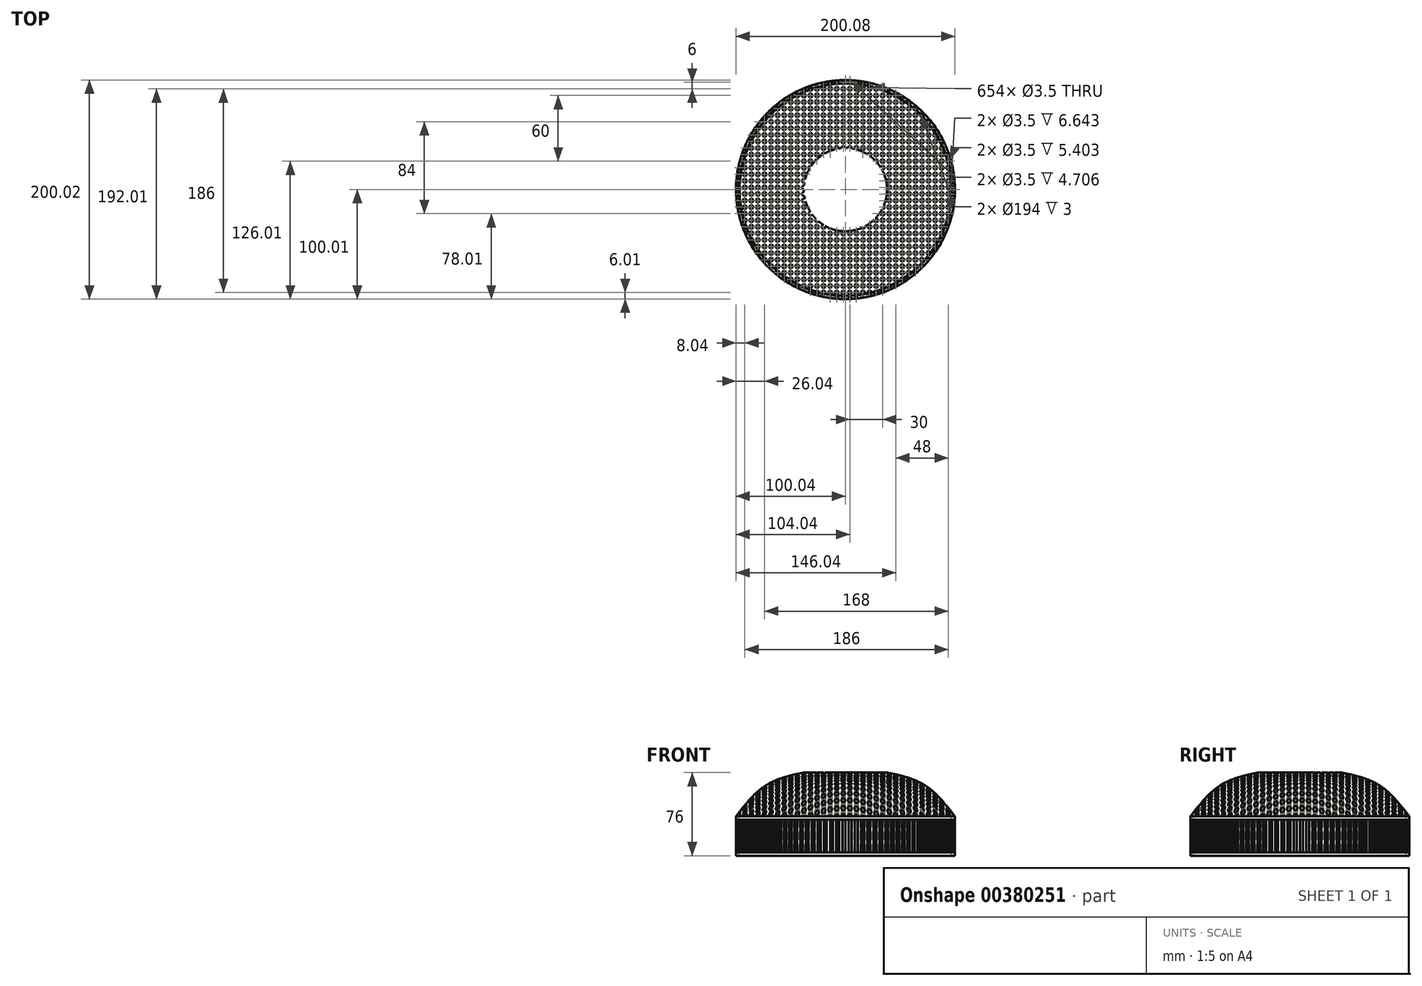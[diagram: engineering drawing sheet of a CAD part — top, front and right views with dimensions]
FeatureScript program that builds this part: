
annotation { "Feature Type Name" : "Feature", "Feature Type Description" : "" }
export const myFeature = defineFeature(function(context is Context, id is Id, definition is map)
    precondition{}
    {
        {
            var Q0;
            Q0=qCreatedBy(makeId("Top.planeOp"),FACE);
            var sketch = newSketch(context, id + "F0", { "sketchPlane" : qUnion([Q0])});
            skCircle(sketch, "E0", {"center": v(0, 0) * mm, "radius": 100 * mm});
            skSolve(sketch);
        }
        {
            var Q0;
            Q0=qCreatedBy(makeId("Top.planeOp"),FACE);
            cPlane(context, id + "F1", {"entities" : qUnion([Q0]), "cplaneType" : CPlaneType.OFFSET, "offset" : 30 * mm, "width" : 150 * mm, "height" : 150 * mm});
        }
        {
            var Q0;
            Q0=qCreatedBy(id+"F1.planeOp",FACE);
            var sketch = newSketch(context, id + "F2", { "sketchPlane" : qUnion([Q0])});
            skCircle(sketch, "E1", {"center": v(0, 0) * mm, "radius": 70 * mm});
            skSolve(sketch);
        }
        {
            var Q0;
            Q0=qCreatedBy(makeId("Top.planeOp"),FACE);
            cPlane(context, id + "F3", {"entities" : qUnion([Q0]), "cplaneType" : CPlaneType.OFFSET, "offset" : 40 * mm, "width" : 150 * mm, "height" : 150 * mm});
        }
        {
            var Q0;
            Q0=qCreatedBy(id+"F3.planeOp",FACE);
            var sketch = newSketch(context, id + "F4", { "sketchPlane" : qUnion([Q0])});
            skCircle(sketch, "E2", {"center": v(0, 0) * mm, "radius": 38 * mm});
            skSolve(sketch);
        }
        {
            var Q0;
            Q0 = qSketchRegion(id + "F0", true);
            var Q1;
            Q1 = qSketchRegion(id + "F2", true);
            var Q2;
            Q2 = qSketchRegion(id + "F4", true);
            loft(context, id + "F5", {"sheetProfilesArray" : [{ "sheetProfileEntities" : qUnion([Q0]) }, { "sheetProfileEntities" : qUnion([Q1]) }, { "sheetProfileEntities" : qUnion([Q2]) }]});
        }
        {
            var Q0;
            Q0=makeQuery(id+"F5.opLoft","CAP_FACE",FACE,{"disambiguationData":[OSD([makeQuery(id+"F0.imprint","IMPRINT",FACE,{"disambiguationData":[TD([[makeQuery(id+"F0.imprint","IMPRINT",EDGE,{"derivedFrom":sQuery(id+"F0.wireOp",EDGE,"E0")}),1.0]])]})])],"isStart":true});
            shell(context, id + "F6", {"entities" : qUnion([Q0]), "thickness" : 3 * mm});
        }
        {
            var Q0;
            Q0=makeQuery(id+"F5.opLoft","CAP_FACE",FACE,{"disambiguationData":[OSD([makeQuery(id+"F4.imprint","IMPRINT",FACE,{"disambiguationData":[TD([[makeQuery(id+"F4.imprint","IMPRINT",EDGE,{"derivedFrom":sQuery(id+"F4.wireOp",EDGE,"E2")}),1.0]])]})])],"isStart":true});
            extrude(context, id + "F7", {"entities" : qUnion([Q0]), "operationType" : NewBodyOperationType.REMOVE, "oppositeDirection" : true, "depth" : 25 * mm});
        }
        {
            var Q0;
            Q0=qCreatedBy(makeId("Top.planeOp"),FACE);
            var sketch = newSketch(context, id + "F8", { "sketchPlane" : qUnion([Q0])});
            skLineSegment(sketch, "E3", {"start": v(0, 0) * mm, "end": v(0, -100) * mm, "construction": true});
            skCircle(sketch, "E4", {"center": v(100, -100) * mm, "radius": 1.75 * mm});
            skLineSegment(sketch, "E5", {"start": v(0, 0) * mm, "end": v(100, 0) * mm, "construction": true});
            skLineSegment(sketch, "E6", {"start": v(100, 0) * mm, "end": v(100, -100) * mm, "construction": true});
            skCircle(sketch, "E7.0.1.0", {"center": v(100, -94) * mm, "radius": 1.75 * mm});
            skCircle(sketch, "E7.0.2.0", {"center": v(100, -88) * mm, "radius": 1.75 * mm});
            skCircle(sketch, "E7.0.3.0", {"center": v(100, -82) * mm, "radius": 1.75 * mm});
            skCircle(sketch, "E7.0.4.0", {"center": v(100, -76) * mm, "radius": 1.75 * mm});
            skCircle(sketch, "E7.0.5.0", {"center": v(100, -70) * mm, "radius": 1.75 * mm});
            skCircle(sketch, "E7.0.6.0", {"center": v(100, -64) * mm, "radius": 1.75 * mm});
            skCircle(sketch, "E7.0.7.0", {"center": v(100, -58) * mm, "radius": 1.75 * mm});
            skCircle(sketch, "E7.0.8.0", {"center": v(100, -52) * mm, "radius": 1.75 * mm});
            skCircle(sketch, "E7.0.9.0", {"center": v(100, -46) * mm, "radius": 1.75 * mm});
            skCircle(sketch, "E7.0.10.0", {"center": v(100, -40) * mm, "radius": 1.75 * mm});
            skCircle(sketch, "E7.0.11.0", {"center": v(100, -34) * mm, "radius": 1.75 * mm});
            skCircle(sketch, "E7.0.12.0", {"center": v(100, -28) * mm, "radius": 1.75 * mm});
            skCircle(sketch, "E7.0.13.0", {"center": v(100, -22) * mm, "radius": 1.75 * mm});
            skCircle(sketch, "E7.0.14.0", {"center": v(100, -16) * mm, "radius": 1.75 * mm});
            skCircle(sketch, "E7.0.15.0", {"center": v(100, -10) * mm, "radius": 1.75 * mm});
            skCircle(sketch, "E7.0.16.0", {"center": v(100, -4) * mm, "radius": 1.75 * mm});
            skCircle(sketch, "E7.0.17.0", {"center": v(100, 2) * mm, "radius": 1.75 * mm});
            skCircle(sketch, "E7.0.18.0", {"center": v(100, 8) * mm, "radius": 1.75 * mm});
            skCircle(sketch, "E7.1.0.0", {"center": v(94, -100) * mm, "radius": 1.75 * mm});
            skCircle(sketch, "E7.1.1.0", {"center": v(94, -94) * mm, "radius": 1.75 * mm});
            skCircle(sketch, "E7.1.2.0", {"center": v(94, -88) * mm, "radius": 1.75 * mm});
            skCircle(sketch, "E7.1.3.0", {"center": v(94, -82) * mm, "radius": 1.75 * mm});
            skCircle(sketch, "E7.1.4.0", {"center": v(94, -76) * mm, "radius": 1.75 * mm});
            skCircle(sketch, "E7.1.5.0", {"center": v(94, -70) * mm, "radius": 1.75 * mm});
            skCircle(sketch, "E7.1.6.0", {"center": v(94, -64) * mm, "radius": 1.75 * mm});
            skCircle(sketch, "E7.1.7.0", {"center": v(94, -58) * mm, "radius": 1.75 * mm});
            skCircle(sketch, "E7.1.8.0", {"center": v(94, -52) * mm, "radius": 1.75 * mm});
            skCircle(sketch, "E7.1.9.0", {"center": v(94, -46) * mm, "radius": 1.75 * mm});
            skCircle(sketch, "E7.1.10.0", {"center": v(94, -40) * mm, "radius": 1.75 * mm});
            skCircle(sketch, "E7.1.11.0", {"center": v(94, -34) * mm, "radius": 1.75 * mm});
            skCircle(sketch, "E7.1.12.0", {"center": v(94, -28) * mm, "radius": 1.75 * mm});
            skCircle(sketch, "E7.1.13.0", {"center": v(94, -22) * mm, "radius": 1.75 * mm});
            skCircle(sketch, "E7.1.14.0", {"center": v(94, -16) * mm, "radius": 1.75 * mm});
            skCircle(sketch, "E7.1.15.0", {"center": v(94, -10) * mm, "radius": 1.75 * mm});
            skCircle(sketch, "E7.1.16.0", {"center": v(94, -4) * mm, "radius": 1.75 * mm});
            skCircle(sketch, "E7.1.17.0", {"center": v(94, 2) * mm, "radius": 1.75 * mm});
            skCircle(sketch, "E7.1.18.0", {"center": v(94, 8) * mm, "radius": 1.75 * mm});
            skCircle(sketch, "E7.2.0.0", {"center": v(88, -100) * mm, "radius": 1.75 * mm});
            skCircle(sketch, "E7.2.1.0", {"center": v(88, -94) * mm, "radius": 1.75 * mm});
            skCircle(sketch, "E7.2.2.0", {"center": v(88, -88) * mm, "radius": 1.75 * mm});
            skCircle(sketch, "E7.2.3.0", {"center": v(88, -82) * mm, "radius": 1.75 * mm});
            skCircle(sketch, "E7.2.4.0", {"center": v(88, -76) * mm, "radius": 1.75 * mm});
            skCircle(sketch, "E7.2.5.0", {"center": v(88, -70) * mm, "radius": 1.75 * mm});
            skCircle(sketch, "E7.2.6.0", {"center": v(88, -64) * mm, "radius": 1.75 * mm});
            skCircle(sketch, "E7.2.7.0", {"center": v(88, -58) * mm, "radius": 1.75 * mm});
            skCircle(sketch, "E7.2.8.0", {"center": v(88, -52) * mm, "radius": 1.75 * mm});
            skCircle(sketch, "E7.2.9.0", {"center": v(88, -46) * mm, "radius": 1.75 * mm});
            skCircle(sketch, "E7.2.10.0", {"center": v(88, -40) * mm, "radius": 1.75 * mm});
            skCircle(sketch, "E7.2.11.0", {"center": v(88, -34) * mm, "radius": 1.75 * mm});
            skCircle(sketch, "E7.2.12.0", {"center": v(88, -28) * mm, "radius": 1.75 * mm});
            skCircle(sketch, "E7.2.13.0", {"center": v(88, -22) * mm, "radius": 1.75 * mm});
            skCircle(sketch, "E7.2.14.0", {"center": v(88, -16) * mm, "radius": 1.75 * mm});
            skCircle(sketch, "E7.2.15.0", {"center": v(88, -10) * mm, "radius": 1.75 * mm});
            skCircle(sketch, "E7.2.16.0", {"center": v(88, -4) * mm, "radius": 1.75 * mm});
            skCircle(sketch, "E7.2.17.0", {"center": v(88, 2) * mm, "radius": 1.75 * mm});
            skCircle(sketch, "E7.2.18.0", {"center": v(88, 8) * mm, "radius": 1.75 * mm});
            skCircle(sketch, "E7.3.0.0", {"center": v(82, -100) * mm, "radius": 1.75 * mm});
            skCircle(sketch, "E7.3.1.0", {"center": v(82, -94) * mm, "radius": 1.75 * mm});
            skCircle(sketch, "E7.3.2.0", {"center": v(82, -88) * mm, "radius": 1.75 * mm});
            skCircle(sketch, "E7.3.3.0", {"center": v(82, -82) * mm, "radius": 1.75 * mm});
            skCircle(sketch, "E7.3.4.0", {"center": v(82, -76) * mm, "radius": 1.75 * mm});
            skCircle(sketch, "E7.3.5.0", {"center": v(82, -70) * mm, "radius": 1.75 * mm});
            skCircle(sketch, "E7.3.6.0", {"center": v(82, -64) * mm, "radius": 1.75 * mm});
            skCircle(sketch, "E7.3.7.0", {"center": v(82, -58) * mm, "radius": 1.75 * mm});
            skCircle(sketch, "E7.3.8.0", {"center": v(82, -52) * mm, "radius": 1.75 * mm});
            skCircle(sketch, "E7.3.9.0", {"center": v(82, -46) * mm, "radius": 1.75 * mm});
            skCircle(sketch, "E7.3.10.0", {"center": v(82, -40) * mm, "radius": 1.75 * mm});
            skCircle(sketch, "E7.3.11.0", {"center": v(82, -34) * mm, "radius": 1.75 * mm});
            skCircle(sketch, "E7.3.12.0", {"center": v(82, -28) * mm, "radius": 1.75 * mm});
            skCircle(sketch, "E7.3.13.0", {"center": v(82, -22) * mm, "radius": 1.75 * mm});
            skCircle(sketch, "E7.3.14.0", {"center": v(82, -16) * mm, "radius": 1.75 * mm});
            skCircle(sketch, "E7.3.15.0", {"center": v(82, -10) * mm, "radius": 1.75 * mm});
            skCircle(sketch, "E7.3.16.0", {"center": v(82, -4) * mm, "radius": 1.75 * mm});
            skCircle(sketch, "E7.3.17.0", {"center": v(82, 2) * mm, "radius": 1.75 * mm});
            skCircle(sketch, "E7.3.18.0", {"center": v(82, 8) * mm, "radius": 1.75 * mm});
            skCircle(sketch, "E7.4.0.0", {"center": v(76, -100) * mm, "radius": 1.75 * mm});
            skCircle(sketch, "E7.4.1.0", {"center": v(76, -94) * mm, "radius": 1.75 * mm});
            skCircle(sketch, "E7.4.2.0", {"center": v(76, -88) * mm, "radius": 1.75 * mm});
            skCircle(sketch, "E7.4.3.0", {"center": v(76, -82) * mm, "radius": 1.75 * mm});
            skCircle(sketch, "E7.4.4.0", {"center": v(76, -76) * mm, "radius": 1.75 * mm});
            skCircle(sketch, "E7.4.5.0", {"center": v(76, -70) * mm, "radius": 1.75 * mm});
            skCircle(sketch, "E7.4.6.0", {"center": v(76, -64) * mm, "radius": 1.75 * mm});
            skCircle(sketch, "E7.4.7.0", {"center": v(76, -58) * mm, "radius": 1.75 * mm});
            skCircle(sketch, "E7.4.8.0", {"center": v(76, -52) * mm, "radius": 1.75 * mm});
            skCircle(sketch, "E7.4.9.0", {"center": v(76, -46) * mm, "radius": 1.75 * mm});
            skCircle(sketch, "E7.4.10.0", {"center": v(76, -40) * mm, "radius": 1.75 * mm});
            skCircle(sketch, "E7.4.11.0", {"center": v(76, -34) * mm, "radius": 1.75 * mm});
            skCircle(sketch, "E7.4.12.0", {"center": v(76, -28) * mm, "radius": 1.75 * mm});
            skCircle(sketch, "E7.4.13.0", {"center": v(76, -22) * mm, "radius": 1.75 * mm});
            skCircle(sketch, "E7.4.14.0", {"center": v(76, -16) * mm, "radius": 1.75 * mm});
            skCircle(sketch, "E7.4.15.0", {"center": v(76, -10) * mm, "radius": 1.75 * mm});
            skCircle(sketch, "E7.4.16.0", {"center": v(76, -4) * mm, "radius": 1.75 * mm});
            skCircle(sketch, "E7.4.17.0", {"center": v(76, 2) * mm, "radius": 1.75 * mm});
            skCircle(sketch, "E7.4.18.0", {"center": v(76, 8) * mm, "radius": 1.75 * mm});
            skCircle(sketch, "E7.5.0.0", {"center": v(70, -100) * mm, "radius": 1.75 * mm});
            skCircle(sketch, "E7.5.1.0", {"center": v(70, -94) * mm, "radius": 1.75 * mm});
            skCircle(sketch, "E7.5.2.0", {"center": v(70, -88) * mm, "radius": 1.75 * mm});
            skCircle(sketch, "E7.5.3.0", {"center": v(70, -82) * mm, "radius": 1.75 * mm});
            skCircle(sketch, "E7.5.4.0", {"center": v(70, -76) * mm, "radius": 1.75 * mm});
            skCircle(sketch, "E7.5.5.0", {"center": v(70, -70) * mm, "radius": 1.75 * mm});
            skCircle(sketch, "E7.5.6.0", {"center": v(70, -64) * mm, "radius": 1.75 * mm});
            skCircle(sketch, "E7.5.7.0", {"center": v(70, -58) * mm, "radius": 1.75 * mm});
            skCircle(sketch, "E7.5.8.0", {"center": v(70, -52) * mm, "radius": 1.75 * mm});
            skCircle(sketch, "E7.5.9.0", {"center": v(70, -46) * mm, "radius": 1.75 * mm});
            skCircle(sketch, "E7.5.10.0", {"center": v(70, -40) * mm, "radius": 1.75 * mm});
            skCircle(sketch, "E7.5.11.0", {"center": v(70, -34) * mm, "radius": 1.75 * mm});
            skCircle(sketch, "E7.5.12.0", {"center": v(70, -28) * mm, "radius": 1.75 * mm});
            skCircle(sketch, "E7.5.13.0", {"center": v(70, -22) * mm, "radius": 1.75 * mm});
            skCircle(sketch, "E7.5.14.0", {"center": v(70, -16) * mm, "radius": 1.75 * mm});
            skCircle(sketch, "E7.5.15.0", {"center": v(70, -10) * mm, "radius": 1.75 * mm});
            skCircle(sketch, "E7.5.16.0", {"center": v(70, -4) * mm, "radius": 1.75 * mm});
            skCircle(sketch, "E7.5.17.0", {"center": v(70, 2) * mm, "radius": 1.75 * mm});
            skCircle(sketch, "E7.5.18.0", {"center": v(70, 8) * mm, "radius": 1.75 * mm});
            skCircle(sketch, "E7.6.0.0", {"center": v(64, -100) * mm, "radius": 1.75 * mm});
            skCircle(sketch, "E7.6.1.0", {"center": v(64, -94) * mm, "radius": 1.75 * mm});
            skCircle(sketch, "E7.6.2.0", {"center": v(64, -88) * mm, "radius": 1.75 * mm});
            skCircle(sketch, "E7.6.3.0", {"center": v(64, -82) * mm, "radius": 1.75 * mm});
            skCircle(sketch, "E7.6.4.0", {"center": v(64, -76) * mm, "radius": 1.75 * mm});
            skCircle(sketch, "E7.6.5.0", {"center": v(64, -70) * mm, "radius": 1.75 * mm});
            skCircle(sketch, "E7.6.6.0", {"center": v(64, -64) * mm, "radius": 1.75 * mm});
            skCircle(sketch, "E7.6.7.0", {"center": v(64, -58) * mm, "radius": 1.75 * mm});
            skCircle(sketch, "E7.6.8.0", {"center": v(64, -52) * mm, "radius": 1.75 * mm});
            skCircle(sketch, "E7.6.9.0", {"center": v(64, -46) * mm, "radius": 1.75 * mm});
            skCircle(sketch, "E7.6.10.0", {"center": v(64, -40) * mm, "radius": 1.75 * mm});
            skCircle(sketch, "E7.6.11.0", {"center": v(64, -34) * mm, "radius": 1.75 * mm});
            skCircle(sketch, "E7.6.12.0", {"center": v(64, -28) * mm, "radius": 1.75 * mm});
            skCircle(sketch, "E7.6.13.0", {"center": v(64, -22) * mm, "radius": 1.75 * mm});
            skCircle(sketch, "E7.6.14.0", {"center": v(64, -16) * mm, "radius": 1.75 * mm});
            skCircle(sketch, "E7.6.15.0", {"center": v(64, -10) * mm, "radius": 1.75 * mm});
            skCircle(sketch, "E7.6.16.0", {"center": v(64, -4) * mm, "radius": 1.75 * mm});
            skCircle(sketch, "E7.6.17.0", {"center": v(64, 2) * mm, "radius": 1.75 * mm});
            skCircle(sketch, "E7.6.18.0", {"center": v(64, 8) * mm, "radius": 1.75 * mm});
            skCircle(sketch, "E7.7.0.0", {"center": v(58, -100) * mm, "radius": 1.75 * mm});
            skCircle(sketch, "E7.7.1.0", {"center": v(58, -94) * mm, "radius": 1.75 * mm});
            skCircle(sketch, "E7.7.2.0", {"center": v(58, -88) * mm, "radius": 1.75 * mm});
            skCircle(sketch, "E7.7.3.0", {"center": v(58, -82) * mm, "radius": 1.75 * mm});
            skCircle(sketch, "E7.7.4.0", {"center": v(58, -76) * mm, "radius": 1.75 * mm});
            skCircle(sketch, "E7.7.5.0", {"center": v(58, -70) * mm, "radius": 1.75 * mm});
            skCircle(sketch, "E7.7.6.0", {"center": v(58, -64) * mm, "radius": 1.75 * mm});
            skCircle(sketch, "E7.7.7.0", {"center": v(58, -58) * mm, "radius": 1.75 * mm});
            skCircle(sketch, "E7.7.8.0", {"center": v(58, -52) * mm, "radius": 1.75 * mm});
            skCircle(sketch, "E7.7.9.0", {"center": v(58, -46) * mm, "radius": 1.75 * mm});
            skCircle(sketch, "E7.7.10.0", {"center": v(58, -40) * mm, "radius": 1.75 * mm});
            skCircle(sketch, "E7.7.11.0", {"center": v(58, -34) * mm, "radius": 1.75 * mm});
            skCircle(sketch, "E7.7.12.0", {"center": v(58, -28) * mm, "radius": 1.75 * mm});
            skCircle(sketch, "E7.7.13.0", {"center": v(58, -22) * mm, "radius": 1.75 * mm});
            skCircle(sketch, "E7.7.14.0", {"center": v(58, -16) * mm, "radius": 1.75 * mm});
            skCircle(sketch, "E7.7.15.0", {"center": v(58, -10) * mm, "radius": 1.75 * mm});
            skCircle(sketch, "E7.7.16.0", {"center": v(58, -4) * mm, "radius": 1.75 * mm});
            skCircle(sketch, "E7.7.17.0", {"center": v(58, 2) * mm, "radius": 1.75 * mm});
            skCircle(sketch, "E7.7.18.0", {"center": v(58, 8) * mm, "radius": 1.75 * mm});
            skCircle(sketch, "E7.8.0.0", {"center": v(52, -100) * mm, "radius": 1.75 * mm});
            skCircle(sketch, "E7.8.1.0", {"center": v(52, -94) * mm, "radius": 1.75 * mm});
            skCircle(sketch, "E7.8.2.0", {"center": v(52, -88) * mm, "radius": 1.75 * mm});
            skCircle(sketch, "E7.8.3.0", {"center": v(52, -82) * mm, "radius": 1.75 * mm});
            skCircle(sketch, "E7.8.4.0", {"center": v(52, -76) * mm, "radius": 1.75 * mm});
            skCircle(sketch, "E7.8.5.0", {"center": v(52, -70) * mm, "radius": 1.75 * mm});
            skCircle(sketch, "E7.8.6.0", {"center": v(52, -64) * mm, "radius": 1.75 * mm});
            skCircle(sketch, "E7.8.7.0", {"center": v(52, -58) * mm, "radius": 1.75 * mm});
            skCircle(sketch, "E7.8.8.0", {"center": v(52, -52) * mm, "radius": 1.75 * mm});
            skCircle(sketch, "E7.8.9.0", {"center": v(52, -46) * mm, "radius": 1.75 * mm});
            skCircle(sketch, "E7.8.10.0", {"center": v(52, -40) * mm, "radius": 1.75 * mm});
            skCircle(sketch, "E7.8.11.0", {"center": v(52, -34) * mm, "radius": 1.75 * mm});
            skCircle(sketch, "E7.8.12.0", {"center": v(52, -28) * mm, "radius": 1.75 * mm});
            skCircle(sketch, "E7.8.13.0", {"center": v(52, -22) * mm, "radius": 1.75 * mm});
            skCircle(sketch, "E7.8.14.0", {"center": v(52, -16) * mm, "radius": 1.75 * mm});
            skCircle(sketch, "E7.8.15.0", {"center": v(52, -10) * mm, "radius": 1.75 * mm});
            skCircle(sketch, "E7.8.16.0", {"center": v(52, -4) * mm, "radius": 1.75 * mm});
            skCircle(sketch, "E7.8.17.0", {"center": v(52, 2) * mm, "radius": 1.75 * mm});
            skCircle(sketch, "E7.8.18.0", {"center": v(52, 8) * mm, "radius": 1.75 * mm});
            skCircle(sketch, "E7.9.0.0", {"center": v(46, -100) * mm, "radius": 1.75 * mm});
            skCircle(sketch, "E7.9.1.0", {"center": v(46, -94) * mm, "radius": 1.75 * mm});
            skCircle(sketch, "E7.9.2.0", {"center": v(46, -88) * mm, "radius": 1.75 * mm});
            skCircle(sketch, "E7.9.3.0", {"center": v(46, -82) * mm, "radius": 1.75 * mm});
            skCircle(sketch, "E7.9.4.0", {"center": v(46, -76) * mm, "radius": 1.75 * mm});
            skCircle(sketch, "E7.9.5.0", {"center": v(46, -70) * mm, "radius": 1.75 * mm});
            skCircle(sketch, "E7.9.6.0", {"center": v(46, -64) * mm, "radius": 1.75 * mm});
            skCircle(sketch, "E7.9.7.0", {"center": v(46, -58) * mm, "radius": 1.75 * mm});
            skCircle(sketch, "E7.9.8.0", {"center": v(46, -52) * mm, "radius": 1.75 * mm});
            skCircle(sketch, "E7.9.9.0", {"center": v(46, -46) * mm, "radius": 1.75 * mm});
            skCircle(sketch, "E7.9.10.0", {"center": v(46, -40) * mm, "radius": 1.75 * mm});
            skCircle(sketch, "E7.9.11.0", {"center": v(46, -34) * mm, "radius": 1.75 * mm});
            skCircle(sketch, "E7.9.12.0", {"center": v(46, -28) * mm, "radius": 1.75 * mm});
            skCircle(sketch, "E7.9.13.0", {"center": v(46, -22) * mm, "radius": 1.75 * mm});
            skCircle(sketch, "E7.9.14.0", {"center": v(46, -16) * mm, "radius": 1.75 * mm});
            skCircle(sketch, "E7.9.15.0", {"center": v(46, -10) * mm, "radius": 1.75 * mm});
            skCircle(sketch, "E7.9.16.0", {"center": v(46, -4) * mm, "radius": 1.75 * mm});
            skCircle(sketch, "E7.9.17.0", {"center": v(46, 2) * mm, "radius": 1.75 * mm});
            skCircle(sketch, "E7.9.18.0", {"center": v(46, 8) * mm, "radius": 1.75 * mm});
            skCircle(sketch, "E7.10.0.0", {"center": v(40, -100) * mm, "radius": 1.75 * mm});
            skCircle(sketch, "E7.10.1.0", {"center": v(40, -94) * mm, "radius": 1.75 * mm});
            skCircle(sketch, "E7.10.2.0", {"center": v(40, -88) * mm, "radius": 1.75 * mm});
            skCircle(sketch, "E7.10.3.0", {"center": v(40, -82) * mm, "radius": 1.75 * mm});
            skCircle(sketch, "E7.10.4.0", {"center": v(40, -76) * mm, "radius": 1.75 * mm});
            skCircle(sketch, "E7.10.5.0", {"center": v(40, -70) * mm, "radius": 1.75 * mm});
            skCircle(sketch, "E7.10.6.0", {"center": v(40, -64) * mm, "radius": 1.75 * mm});
            skCircle(sketch, "E7.10.7.0", {"center": v(40, -58) * mm, "radius": 1.75 * mm});
            skCircle(sketch, "E7.10.8.0", {"center": v(40, -52) * mm, "radius": 1.75 * mm});
            skCircle(sketch, "E7.10.9.0", {"center": v(40, -46) * mm, "radius": 1.75 * mm});
            skCircle(sketch, "E7.10.10.0", {"center": v(40, -40) * mm, "radius": 1.75 * mm});
            skCircle(sketch, "E7.10.11.0", {"center": v(40, -34) * mm, "radius": 1.75 * mm});
            skCircle(sketch, "E7.10.12.0", {"center": v(40, -28) * mm, "radius": 1.75 * mm});
            skCircle(sketch, "E7.10.13.0", {"center": v(40, -22) * mm, "radius": 1.75 * mm});
            skCircle(sketch, "E7.10.14.0", {"center": v(40, -16) * mm, "radius": 1.75 * mm});
            skCircle(sketch, "E7.10.15.0", {"center": v(40, -10) * mm, "radius": 1.75 * mm});
            skCircle(sketch, "E7.10.16.0", {"center": v(40, -4) * mm, "radius": 1.75 * mm});
            skCircle(sketch, "E7.10.17.0", {"center": v(40, 2) * mm, "radius": 1.75 * mm});
            skCircle(sketch, "E7.10.18.0", {"center": v(40, 8) * mm, "radius": 1.75 * mm});
            skCircle(sketch, "E7.11.0.0", {"center": v(34, -100) * mm, "radius": 1.75 * mm});
            skCircle(sketch, "E7.11.1.0", {"center": v(34, -94) * mm, "radius": 1.75 * mm});
            skCircle(sketch, "E7.11.2.0", {"center": v(34, -88) * mm, "radius": 1.75 * mm});
            skCircle(sketch, "E7.11.3.0", {"center": v(34, -82) * mm, "radius": 1.75 * mm});
            skCircle(sketch, "E7.11.4.0", {"center": v(34, -76) * mm, "radius": 1.75 * mm});
            skCircle(sketch, "E7.11.5.0", {"center": v(34, -70) * mm, "radius": 1.75 * mm});
            skCircle(sketch, "E7.11.6.0", {"center": v(34, -64) * mm, "radius": 1.75 * mm});
            skCircle(sketch, "E7.11.7.0", {"center": v(34, -58) * mm, "radius": 1.75 * mm});
            skCircle(sketch, "E7.11.8.0", {"center": v(34, -52) * mm, "radius": 1.75 * mm});
            skCircle(sketch, "E7.11.9.0", {"center": v(34, -46) * mm, "radius": 1.75 * mm});
            skCircle(sketch, "E7.11.10.0", {"center": v(34, -40) * mm, "radius": 1.75 * mm});
            skCircle(sketch, "E7.11.11.0", {"center": v(34, -34) * mm, "radius": 1.75 * mm});
            skCircle(sketch, "E7.11.12.0", {"center": v(34, -28) * mm, "radius": 1.75 * mm});
            skCircle(sketch, "E7.11.13.0", {"center": v(34, -22) * mm, "radius": 1.75 * mm});
            skCircle(sketch, "E7.11.14.0", {"center": v(34, -16) * mm, "radius": 1.75 * mm});
            skCircle(sketch, "E7.11.15.0", {"center": v(34, -10) * mm, "radius": 1.75 * mm});
            skCircle(sketch, "E7.11.16.0", {"center": v(34, -4) * mm, "radius": 1.75 * mm});
            skCircle(sketch, "E7.11.17.0", {"center": v(34, 2) * mm, "radius": 1.75 * mm});
            skCircle(sketch, "E7.11.18.0", {"center": v(34, 8) * mm, "radius": 1.75 * mm});
            skCircle(sketch, "E7.12.0.0", {"center": v(28, -100) * mm, "radius": 1.75 * mm});
            skCircle(sketch, "E7.12.1.0", {"center": v(28, -94) * mm, "radius": 1.75 * mm});
            skCircle(sketch, "E7.12.2.0", {"center": v(28, -88) * mm, "radius": 1.75 * mm});
            skCircle(sketch, "E7.12.3.0", {"center": v(28, -82) * mm, "radius": 1.75 * mm});
            skCircle(sketch, "E7.12.4.0", {"center": v(28, -76) * mm, "radius": 1.75 * mm});
            skCircle(sketch, "E7.12.5.0", {"center": v(28, -70) * mm, "radius": 1.75 * mm});
            skCircle(sketch, "E7.12.6.0", {"center": v(28, -64) * mm, "radius": 1.75 * mm});
            skCircle(sketch, "E7.12.7.0", {"center": v(28, -58) * mm, "radius": 1.75 * mm});
            skCircle(sketch, "E7.12.8.0", {"center": v(28, -52) * mm, "radius": 1.75 * mm});
            skCircle(sketch, "E7.12.9.0", {"center": v(28, -46) * mm, "radius": 1.75 * mm});
            skCircle(sketch, "E7.12.10.0", {"center": v(28, -40) * mm, "radius": 1.75 * mm});
            skCircle(sketch, "E7.12.11.0", {"center": v(28, -34) * mm, "radius": 1.75 * mm});
            skCircle(sketch, "E7.12.12.0", {"center": v(28, -28) * mm, "radius": 1.75 * mm});
            skCircle(sketch, "E7.12.13.0", {"center": v(28, -22) * mm, "radius": 1.75 * mm});
            skCircle(sketch, "E7.12.14.0", {"center": v(28, -16) * mm, "radius": 1.75 * mm});
            skCircle(sketch, "E7.12.15.0", {"center": v(28, -10) * mm, "radius": 1.75 * mm});
            skCircle(sketch, "E7.12.16.0", {"center": v(28, -4) * mm, "radius": 1.75 * mm});
            skCircle(sketch, "E7.12.17.0", {"center": v(28, 2) * mm, "radius": 1.75 * mm});
            skCircle(sketch, "E7.12.18.0", {"center": v(28, 8) * mm, "radius": 1.75 * mm});
            skCircle(sketch, "E7.13.0.0", {"center": v(22, -100) * mm, "radius": 1.75 * mm});
            skCircle(sketch, "E7.13.1.0", {"center": v(22, -94) * mm, "radius": 1.75 * mm});
            skCircle(sketch, "E7.13.2.0", {"center": v(22, -88) * mm, "radius": 1.75 * mm});
            skCircle(sketch, "E7.13.3.0", {"center": v(22, -82) * mm, "radius": 1.75 * mm});
            skCircle(sketch, "E7.13.4.0", {"center": v(22, -76) * mm, "radius": 1.75 * mm});
            skCircle(sketch, "E7.13.5.0", {"center": v(22, -70) * mm, "radius": 1.75 * mm});
            skCircle(sketch, "E7.13.6.0", {"center": v(22, -64) * mm, "radius": 1.75 * mm});
            skCircle(sketch, "E7.13.7.0", {"center": v(22, -58) * mm, "radius": 1.75 * mm});
            skCircle(sketch, "E7.13.8.0", {"center": v(22, -52) * mm, "radius": 1.75 * mm});
            skCircle(sketch, "E7.13.9.0", {"center": v(22, -46) * mm, "radius": 1.75 * mm});
            skCircle(sketch, "E7.13.10.0", {"center": v(22, -40) * mm, "radius": 1.75 * mm});
            skCircle(sketch, "E7.13.11.0", {"center": v(22, -34) * mm, "radius": 1.75 * mm});
            skCircle(sketch, "E7.13.12.0", {"center": v(22, -28) * mm, "radius": 1.75 * mm});
            skCircle(sketch, "E7.13.13.0", {"center": v(22, -22) * mm, "radius": 1.75 * mm});
            skCircle(sketch, "E7.13.14.0", {"center": v(22, -16) * mm, "radius": 1.75 * mm});
            skCircle(sketch, "E7.13.15.0", {"center": v(22, -10) * mm, "radius": 1.75 * mm});
            skCircle(sketch, "E7.13.16.0", {"center": v(22, -4) * mm, "radius": 1.75 * mm});
            skCircle(sketch, "E7.13.17.0", {"center": v(22, 2) * mm, "radius": 1.75 * mm});
            skCircle(sketch, "E7.13.18.0", {"center": v(22, 8) * mm, "radius": 1.75 * mm});
            skCircle(sketch, "E7.14.0.0", {"center": v(16, -100) * mm, "radius": 1.75 * mm});
            skCircle(sketch, "E7.14.1.0", {"center": v(16, -94) * mm, "radius": 1.75 * mm});
            skCircle(sketch, "E7.14.2.0", {"center": v(16, -88) * mm, "radius": 1.75 * mm});
            skCircle(sketch, "E7.14.3.0", {"center": v(16, -82) * mm, "radius": 1.75 * mm});
            skCircle(sketch, "E7.14.4.0", {"center": v(16, -76) * mm, "radius": 1.75 * mm});
            skCircle(sketch, "E7.14.5.0", {"center": v(16, -70) * mm, "radius": 1.75 * mm});
            skCircle(sketch, "E7.14.6.0", {"center": v(16, -64) * mm, "radius": 1.75 * mm});
            skCircle(sketch, "E7.14.7.0", {"center": v(16, -58) * mm, "radius": 1.75 * mm});
            skCircle(sketch, "E7.14.8.0", {"center": v(16, -52) * mm, "radius": 1.75 * mm});
            skCircle(sketch, "E7.14.9.0", {"center": v(16, -46) * mm, "radius": 1.75 * mm});
            skCircle(sketch, "E7.14.10.0", {"center": v(16, -40) * mm, "radius": 1.75 * mm});
            skCircle(sketch, "E7.14.11.0", {"center": v(16, -34) * mm, "radius": 1.75 * mm});
            skCircle(sketch, "E7.14.12.0", {"center": v(16, -28) * mm, "radius": 1.75 * mm});
            skCircle(sketch, "E7.14.13.0", {"center": v(16, -22) * mm, "radius": 1.75 * mm});
            skCircle(sketch, "E7.14.14.0", {"center": v(16, -16) * mm, "radius": 1.75 * mm});
            skCircle(sketch, "E7.14.15.0", {"center": v(16, -10) * mm, "radius": 1.75 * mm});
            skCircle(sketch, "E7.14.16.0", {"center": v(16, -4) * mm, "radius": 1.75 * mm});
            skCircle(sketch, "E7.14.17.0", {"center": v(16, 2) * mm, "radius": 1.75 * mm});
            skCircle(sketch, "E7.14.18.0", {"center": v(16, 8) * mm, "radius": 1.75 * mm});
            skCircle(sketch, "E7.15.0.0", {"center": v(10, -100) * mm, "radius": 1.75 * mm});
            skCircle(sketch, "E7.15.1.0", {"center": v(10, -94) * mm, "radius": 1.75 * mm});
            skCircle(sketch, "E7.15.2.0", {"center": v(10, -88) * mm, "radius": 1.75 * mm});
            skCircle(sketch, "E7.15.3.0", {"center": v(10, -82) * mm, "radius": 1.75 * mm});
            skCircle(sketch, "E7.15.4.0", {"center": v(10, -76) * mm, "radius": 1.75 * mm});
            skCircle(sketch, "E7.15.5.0", {"center": v(10, -70) * mm, "radius": 1.75 * mm});
            skCircle(sketch, "E7.15.6.0", {"center": v(10, -64) * mm, "radius": 1.75 * mm});
            skCircle(sketch, "E7.15.7.0", {"center": v(10, -58) * mm, "radius": 1.75 * mm});
            skCircle(sketch, "E7.15.8.0", {"center": v(10, -52) * mm, "radius": 1.75 * mm});
            skCircle(sketch, "E7.15.9.0", {"center": v(10, -46) * mm, "radius": 1.75 * mm});
            skCircle(sketch, "E7.15.10.0", {"center": v(10, -40) * mm, "radius": 1.75 * mm});
            skCircle(sketch, "E7.15.11.0", {"center": v(10, -34) * mm, "radius": 1.75 * mm});
            skCircle(sketch, "E7.15.12.0", {"center": v(10, -28) * mm, "radius": 1.75 * mm});
            skCircle(sketch, "E7.15.13.0", {"center": v(10, -22) * mm, "radius": 1.75 * mm});
            skCircle(sketch, "E7.15.14.0", {"center": v(10, -16) * mm, "radius": 1.75 * mm});
            skCircle(sketch, "E7.15.15.0", {"center": v(10, -10) * mm, "radius": 1.75 * mm});
            skCircle(sketch, "E7.15.16.0", {"center": v(10, -4) * mm, "radius": 1.75 * mm});
            skCircle(sketch, "E7.15.17.0", {"center": v(10, 2) * mm, "radius": 1.75 * mm});
            skCircle(sketch, "E7.15.18.0", {"center": v(10, 8) * mm, "radius": 1.75 * mm});
            skCircle(sketch, "E7.16.0.0", {"center": v(4, -100) * mm, "radius": 1.75 * mm});
            skCircle(sketch, "E7.16.1.0", {"center": v(4, -94) * mm, "radius": 1.75 * mm});
            skCircle(sketch, "E7.16.2.0", {"center": v(4, -88) * mm, "radius": 1.75 * mm});
            skCircle(sketch, "E7.16.3.0", {"center": v(4, -82) * mm, "radius": 1.75 * mm});
            skCircle(sketch, "E7.16.4.0", {"center": v(4, -76) * mm, "radius": 1.75 * mm});
            skCircle(sketch, "E7.16.5.0", {"center": v(4, -70) * mm, "radius": 1.75 * mm});
            skCircle(sketch, "E7.16.6.0", {"center": v(4, -64) * mm, "radius": 1.75 * mm});
            skCircle(sketch, "E7.16.7.0", {"center": v(4, -58) * mm, "radius": 1.75 * mm});
            skCircle(sketch, "E7.16.8.0", {"center": v(4, -52) * mm, "radius": 1.75 * mm});
            skCircle(sketch, "E7.16.9.0", {"center": v(4, -46) * mm, "radius": 1.75 * mm});
            skCircle(sketch, "E7.16.10.0", {"center": v(4, -40) * mm, "radius": 1.75 * mm});
            skCircle(sketch, "E7.16.11.0", {"center": v(4, -34) * mm, "radius": 1.75 * mm});
            skCircle(sketch, "E7.16.12.0", {"center": v(4, -28) * mm, "radius": 1.75 * mm});
            skCircle(sketch, "E7.16.13.0", {"center": v(4, -22) * mm, "radius": 1.75 * mm});
            skCircle(sketch, "E7.16.14.0", {"center": v(4, -16) * mm, "radius": 1.75 * mm});
            skCircle(sketch, "E7.16.15.0", {"center": v(4, -10) * mm, "radius": 1.75 * mm});
            skCircle(sketch, "E7.16.16.0", {"center": v(4, -4) * mm, "radius": 1.75 * mm});
            skCircle(sketch, "E7.16.17.0", {"center": v(4, 2) * mm, "radius": 1.75 * mm});
            skCircle(sketch, "E7.16.18.0", {"center": v(4, 8) * mm, "radius": 1.75 * mm});
            skCircle(sketch, "E7.17.0.0", {"center": v(-2, -100) * mm, "radius": 1.75 * mm});
            skCircle(sketch, "E7.17.1.0", {"center": v(-2, -94) * mm, "radius": 1.75 * mm});
            skCircle(sketch, "E7.17.2.0", {"center": v(-2, -88) * mm, "radius": 1.75 * mm});
            skCircle(sketch, "E7.17.3.0", {"center": v(-2, -82) * mm, "radius": 1.75 * mm});
            skCircle(sketch, "E7.17.4.0", {"center": v(-2, -76) * mm, "radius": 1.75 * mm});
            skCircle(sketch, "E7.17.5.0", {"center": v(-2, -70) * mm, "radius": 1.75 * mm});
            skCircle(sketch, "E7.17.6.0", {"center": v(-2, -64) * mm, "radius": 1.75 * mm});
            skCircle(sketch, "E7.17.7.0", {"center": v(-2, -58) * mm, "radius": 1.75 * mm});
            skCircle(sketch, "E7.17.8.0", {"center": v(-2, -52) * mm, "radius": 1.75 * mm});
            skCircle(sketch, "E7.17.9.0", {"center": v(-2, -46) * mm, "radius": 1.75 * mm});
            skCircle(sketch, "E7.17.10.0", {"center": v(-2, -40) * mm, "radius": 1.75 * mm});
            skCircle(sketch, "E7.17.11.0", {"center": v(-2, -34) * mm, "radius": 1.75 * mm});
            skCircle(sketch, "E7.17.12.0", {"center": v(-2, -28) * mm, "radius": 1.75 * mm});
            skCircle(sketch, "E7.17.13.0", {"center": v(-2, -22) * mm, "radius": 1.75 * mm});
            skCircle(sketch, "E7.17.14.0", {"center": v(-2, -16) * mm, "radius": 1.75 * mm});
            skCircle(sketch, "E7.17.15.0", {"center": v(-2, -10) * mm, "radius": 1.75 * mm});
            skCircle(sketch, "E7.17.16.0", {"center": v(-2, -4) * mm, "radius": 1.75 * mm});
            skCircle(sketch, "E7.17.17.0", {"center": v(-2, 2) * mm, "radius": 1.75 * mm});
            skCircle(sketch, "E7.17.18.0", {"center": v(-2, 8) * mm, "radius": 1.75 * mm});
            skCircle(sketch, "E7.18.0.0", {"center": v(-8, -100) * mm, "radius": 1.75 * mm});
            skCircle(sketch, "E7.18.1.0", {"center": v(-8, -94) * mm, "radius": 1.75 * mm});
            skCircle(sketch, "E7.18.2.0", {"center": v(-8, -88) * mm, "radius": 1.75 * mm});
            skCircle(sketch, "E7.18.3.0", {"center": v(-8, -82) * mm, "radius": 1.75 * mm});
            skCircle(sketch, "E7.18.4.0", {"center": v(-8, -76) * mm, "radius": 1.75 * mm});
            skCircle(sketch, "E7.18.5.0", {"center": v(-8, -70) * mm, "radius": 1.75 * mm});
            skCircle(sketch, "E7.18.6.0", {"center": v(-8, -64) * mm, "radius": 1.75 * mm});
            skCircle(sketch, "E7.18.7.0", {"center": v(-8, -58) * mm, "radius": 1.75 * mm});
            skCircle(sketch, "E7.18.8.0", {"center": v(-8, -52) * mm, "radius": 1.75 * mm});
            skCircle(sketch, "E7.18.9.0", {"center": v(-8, -46) * mm, "radius": 1.75 * mm});
            skCircle(sketch, "E7.18.10.0", {"center": v(-8, -40) * mm, "radius": 1.75 * mm});
            skCircle(sketch, "E7.18.11.0", {"center": v(-8, -34) * mm, "radius": 1.75 * mm});
            skCircle(sketch, "E7.18.12.0", {"center": v(-8, -28) * mm, "radius": 1.75 * mm});
            skCircle(sketch, "E7.18.13.0", {"center": v(-8, -22) * mm, "radius": 1.75 * mm});
            skCircle(sketch, "E7.18.14.0", {"center": v(-8, -16) * mm, "radius": 1.75 * mm});
            skCircle(sketch, "E7.18.15.0", {"center": v(-8, -10) * mm, "radius": 1.75 * mm});
            skCircle(sketch, "E7.18.16.0", {"center": v(-8, -4) * mm, "radius": 1.75 * mm});
            skCircle(sketch, "E7.18.17.0", {"center": v(-8, 2) * mm, "radius": 1.75 * mm});
            skCircle(sketch, "E7.18.18.0", {"center": v(-8, 8) * mm, "radius": 1.75 * mm});
            skLineSegment(sketch, "E7.direction1", {"start": v(100, -100) * mm, "end": v(94, -100) * mm, "construction": true});
            skLineSegment(sketch, "E7.direction2", {"start": v(100, -100) * mm, "end": v(100, -94) * mm, "construction": true});
            skCircle(sketch, "E8.0.19.0", {"center": v(-14, -100) * mm, "radius": 1.75 * mm});
            skCircle(sketch, "E8.0.19.1", {"center": v(-14, -94) * mm, "radius": 1.75 * mm});
            skCircle(sketch, "E8.0.19.2", {"center": v(-14, -88) * mm, "radius": 1.75 * mm});
            skCircle(sketch, "E8.0.19.3", {"center": v(-14, -82) * mm, "radius": 1.75 * mm});
            skCircle(sketch, "E8.0.19.4", {"center": v(-14, -76) * mm, "radius": 1.75 * mm});
            skCircle(sketch, "E8.0.19.5", {"center": v(-14, -70) * mm, "radius": 1.75 * mm});
            skCircle(sketch, "E8.0.19.6", {"center": v(-14, -64) * mm, "radius": 1.75 * mm});
            skCircle(sketch, "E8.0.19.7", {"center": v(-14, -58) * mm, "radius": 1.75 * mm});
            skCircle(sketch, "E8.0.19.8", {"center": v(-14, -52) * mm, "radius": 1.75 * mm});
            skCircle(sketch, "E8.0.19.9", {"center": v(-14, -46) * mm, "radius": 1.75 * mm});
            skCircle(sketch, "E8.0.19.10", {"center": v(-14, -40) * mm, "radius": 1.75 * mm});
            skCircle(sketch, "E8.0.19.11", {"center": v(-14, -34) * mm, "radius": 1.75 * mm});
            skCircle(sketch, "E8.0.19.12", {"center": v(-14, -28) * mm, "radius": 1.75 * mm});
            skCircle(sketch, "E8.0.19.13", {"center": v(-14, -22) * mm, "radius": 1.75 * mm});
            skCircle(sketch, "E8.0.19.14", {"center": v(-14, -16) * mm, "radius": 1.75 * mm});
            skCircle(sketch, "E8.0.19.15", {"center": v(-14, -10) * mm, "radius": 1.75 * mm});
            skCircle(sketch, "E8.0.19.16", {"center": v(-14, -4) * mm, "radius": 1.75 * mm});
            skCircle(sketch, "E8.0.19.17", {"center": v(-14, 2) * mm, "radius": 1.75 * mm});
            skCircle(sketch, "E8.0.19.18", {"center": v(-14, 8) * mm, "radius": 1.75 * mm});
            skCircle(sketch, "E8.0.20.0", {"center": v(-20, -100) * mm, "radius": 1.75 * mm});
            skCircle(sketch, "E8.0.20.1", {"center": v(-20, -94) * mm, "radius": 1.75 * mm});
            skCircle(sketch, "E8.0.20.2", {"center": v(-20, -88) * mm, "radius": 1.75 * mm});
            skCircle(sketch, "E8.0.20.3", {"center": v(-20, -82) * mm, "radius": 1.75 * mm});
            skCircle(sketch, "E8.0.20.4", {"center": v(-20, -76) * mm, "radius": 1.75 * mm});
            skCircle(sketch, "E8.0.20.5", {"center": v(-20, -70) * mm, "radius": 1.75 * mm});
            skCircle(sketch, "E8.0.20.6", {"center": v(-20, -64) * mm, "radius": 1.75 * mm});
            skCircle(sketch, "E8.0.20.7", {"center": v(-20, -58) * mm, "radius": 1.75 * mm});
            skCircle(sketch, "E8.0.20.8", {"center": v(-20, -52) * mm, "radius": 1.75 * mm});
            skCircle(sketch, "E8.0.20.9", {"center": v(-20, -46) * mm, "radius": 1.75 * mm});
            skCircle(sketch, "E8.0.20.10", {"center": v(-20, -40) * mm, "radius": 1.75 * mm});
            skCircle(sketch, "E8.0.20.11", {"center": v(-20, -34) * mm, "radius": 1.75 * mm});
            skCircle(sketch, "E8.0.20.12", {"center": v(-20, -28) * mm, "radius": 1.75 * mm});
            skCircle(sketch, "E8.0.20.13", {"center": v(-20, -22) * mm, "radius": 1.75 * mm});
            skCircle(sketch, "E8.0.20.14", {"center": v(-20, -16) * mm, "radius": 1.75 * mm});
            skCircle(sketch, "E8.0.20.15", {"center": v(-20, -10) * mm, "radius": 1.75 * mm});
            skCircle(sketch, "E8.0.20.16", {"center": v(-20, -4) * mm, "radius": 1.75 * mm});
            skCircle(sketch, "E8.0.20.17", {"center": v(-20, 2) * mm, "radius": 1.75 * mm});
            skCircle(sketch, "E8.0.20.18", {"center": v(-20, 8) * mm, "radius": 1.75 * mm});
            skCircle(sketch, "E8.0.21.0", {"center": v(-26, -100) * mm, "radius": 1.75 * mm});
            skCircle(sketch, "E8.0.21.1", {"center": v(-26, -94) * mm, "radius": 1.75 * mm});
            skCircle(sketch, "E8.0.21.2", {"center": v(-26, -88) * mm, "radius": 1.75 * mm});
            skCircle(sketch, "E8.0.21.3", {"center": v(-26, -82) * mm, "radius": 1.75 * mm});
            skCircle(sketch, "E8.0.21.4", {"center": v(-26, -76) * mm, "radius": 1.75 * mm});
            skCircle(sketch, "E8.0.21.5", {"center": v(-26, -70) * mm, "radius": 1.75 * mm});
            skCircle(sketch, "E8.0.21.6", {"center": v(-26, -64) * mm, "radius": 1.75 * mm});
            skCircle(sketch, "E8.0.21.7", {"center": v(-26, -58) * mm, "radius": 1.75 * mm});
            skCircle(sketch, "E8.0.21.8", {"center": v(-26, -52) * mm, "radius": 1.75 * mm});
            skCircle(sketch, "E8.0.21.9", {"center": v(-26, -46) * mm, "radius": 1.75 * mm});
            skCircle(sketch, "E8.0.21.10", {"center": v(-26, -40) * mm, "radius": 1.75 * mm});
            skCircle(sketch, "E8.0.21.11", {"center": v(-26, -34) * mm, "radius": 1.75 * mm});
            skCircle(sketch, "E8.0.21.12", {"center": v(-26, -28) * mm, "radius": 1.75 * mm});
            skCircle(sketch, "E8.0.21.13", {"center": v(-26, -22) * mm, "radius": 1.75 * mm});
            skCircle(sketch, "E8.0.21.14", {"center": v(-26, -16) * mm, "radius": 1.75 * mm});
            skCircle(sketch, "E8.0.21.15", {"center": v(-26, -10) * mm, "radius": 1.75 * mm});
            skCircle(sketch, "E8.0.21.16", {"center": v(-26, -4) * mm, "radius": 1.75 * mm});
            skCircle(sketch, "E8.0.21.17", {"center": v(-26, 2) * mm, "radius": 1.75 * mm});
            skCircle(sketch, "E8.0.21.18", {"center": v(-26, 8) * mm, "radius": 1.75 * mm});
            skCircle(sketch, "E8.0.22.0", {"center": v(-32, -100) * mm, "radius": 1.75 * mm});
            skCircle(sketch, "E8.0.22.1", {"center": v(-32, -94) * mm, "radius": 1.75 * mm});
            skCircle(sketch, "E8.0.22.2", {"center": v(-32, -88) * mm, "radius": 1.75 * mm});
            skCircle(sketch, "E8.0.22.3", {"center": v(-32, -82) * mm, "radius": 1.75 * mm});
            skCircle(sketch, "E8.0.22.4", {"center": v(-32, -76) * mm, "radius": 1.75 * mm});
            skCircle(sketch, "E8.0.22.5", {"center": v(-32, -70) * mm, "radius": 1.75 * mm});
            skCircle(sketch, "E8.0.22.6", {"center": v(-32, -64) * mm, "radius": 1.75 * mm});
            skCircle(sketch, "E8.0.22.7", {"center": v(-32, -58) * mm, "radius": 1.75 * mm});
            skCircle(sketch, "E8.0.22.8", {"center": v(-32, -52) * mm, "radius": 1.75 * mm});
            skCircle(sketch, "E8.0.22.9", {"center": v(-32, -46) * mm, "radius": 1.75 * mm});
            skCircle(sketch, "E8.0.22.10", {"center": v(-32, -40) * mm, "radius": 1.75 * mm});
            skCircle(sketch, "E8.0.22.11", {"center": v(-32, -34) * mm, "radius": 1.75 * mm});
            skCircle(sketch, "E8.0.22.12", {"center": v(-32, -28) * mm, "radius": 1.75 * mm});
            skCircle(sketch, "E8.0.22.13", {"center": v(-32, -22) * mm, "radius": 1.75 * mm});
            skCircle(sketch, "E8.0.22.14", {"center": v(-32, -16) * mm, "radius": 1.75 * mm});
            skCircle(sketch, "E8.0.22.15", {"center": v(-32, -10) * mm, "radius": 1.75 * mm});
            skCircle(sketch, "E8.0.22.16", {"center": v(-32, -4) * mm, "radius": 1.75 * mm});
            skCircle(sketch, "E8.0.22.17", {"center": v(-32, 2) * mm, "radius": 1.75 * mm});
            skCircle(sketch, "E8.0.22.18", {"center": v(-32, 8) * mm, "radius": 1.75 * mm});
            skCircle(sketch, "E9.0.0.19", {"center": v(100, 14) * mm, "radius": 1.75 * mm});
            skCircle(sketch, "E9.0.0.20", {"center": v(100, 20) * mm, "radius": 1.75 * mm});
            skCircle(sketch, "E9.0.0.21", {"center": v(100, 26) * mm, "radius": 1.75 * mm});
            skCircle(sketch, "E9.0.0.22", {"center": v(100, 32) * mm, "radius": 1.75 * mm});
            skCircle(sketch, "E9.0.1.19", {"center": v(94, 14) * mm, "radius": 1.75 * mm});
            skCircle(sketch, "E9.0.1.20", {"center": v(94, 20) * mm, "radius": 1.75 * mm});
            skCircle(sketch, "E9.0.1.21", {"center": v(94, 26) * mm, "radius": 1.75 * mm});
            skCircle(sketch, "E9.0.1.22", {"center": v(94, 32) * mm, "radius": 1.75 * mm});
            skCircle(sketch, "E9.0.2.19", {"center": v(88, 14) * mm, "radius": 1.75 * mm});
            skCircle(sketch, "E9.0.2.20", {"center": v(88, 20) * mm, "radius": 1.75 * mm});
            skCircle(sketch, "E9.0.2.21", {"center": v(88, 26) * mm, "radius": 1.75 * mm});
            skCircle(sketch, "E9.0.2.22", {"center": v(88, 32) * mm, "radius": 1.75 * mm});
            skCircle(sketch, "E9.0.3.19", {"center": v(82, 14) * mm, "radius": 1.75 * mm});
            skCircle(sketch, "E9.0.3.20", {"center": v(82, 20) * mm, "radius": 1.75 * mm});
            skCircle(sketch, "E9.0.3.21", {"center": v(82, 26) * mm, "radius": 1.75 * mm});
            skCircle(sketch, "E9.0.3.22", {"center": v(82, 32) * mm, "radius": 1.75 * mm});
            skCircle(sketch, "E9.0.4.19", {"center": v(76, 14) * mm, "radius": 1.75 * mm});
            skCircle(sketch, "E9.0.4.20", {"center": v(76, 20) * mm, "radius": 1.75 * mm});
            skCircle(sketch, "E9.0.4.21", {"center": v(76, 26) * mm, "radius": 1.75 * mm});
            skCircle(sketch, "E9.0.4.22", {"center": v(76, 32) * mm, "radius": 1.75 * mm});
            skCircle(sketch, "E9.0.5.19", {"center": v(70, 14) * mm, "radius": 1.75 * mm});
            skCircle(sketch, "E9.0.5.20", {"center": v(70, 20) * mm, "radius": 1.75 * mm});
            skCircle(sketch, "E9.0.5.21", {"center": v(70, 26) * mm, "radius": 1.75 * mm});
            skCircle(sketch, "E9.0.5.22", {"center": v(70, 32) * mm, "radius": 1.75 * mm});
            skCircle(sketch, "E9.0.6.19", {"center": v(64, 14) * mm, "radius": 1.75 * mm});
            skCircle(sketch, "E9.0.6.20", {"center": v(64, 20) * mm, "radius": 1.75 * mm});
            skCircle(sketch, "E9.0.6.21", {"center": v(64, 26) * mm, "radius": 1.75 * mm});
            skCircle(sketch, "E9.0.6.22", {"center": v(64, 32) * mm, "radius": 1.75 * mm});
            skCircle(sketch, "E9.0.7.19", {"center": v(58, 14) * mm, "radius": 1.75 * mm});
            skCircle(sketch, "E9.0.7.20", {"center": v(58, 20) * mm, "radius": 1.75 * mm});
            skCircle(sketch, "E9.0.7.21", {"center": v(58, 26) * mm, "radius": 1.75 * mm});
            skCircle(sketch, "E9.0.7.22", {"center": v(58, 32) * mm, "radius": 1.75 * mm});
            skCircle(sketch, "E9.0.8.19", {"center": v(52, 14) * mm, "radius": 1.75 * mm});
            skCircle(sketch, "E9.0.8.20", {"center": v(52, 20) * mm, "radius": 1.75 * mm});
            skCircle(sketch, "E9.0.8.21", {"center": v(52, 26) * mm, "radius": 1.75 * mm});
            skCircle(sketch, "E9.0.8.22", {"center": v(52, 32) * mm, "radius": 1.75 * mm});
            skCircle(sketch, "E9.0.9.19", {"center": v(46, 14) * mm, "radius": 1.75 * mm});
            skCircle(sketch, "E9.0.9.20", {"center": v(46, 20) * mm, "radius": 1.75 * mm});
            skCircle(sketch, "E9.0.9.21", {"center": v(46, 26) * mm, "radius": 1.75 * mm});
            skCircle(sketch, "E9.0.9.22", {"center": v(46, 32) * mm, "radius": 1.75 * mm});
            skCircle(sketch, "E9.0.10.19", {"center": v(40, 14) * mm, "radius": 1.75 * mm});
            skCircle(sketch, "E9.0.10.20", {"center": v(40, 20) * mm, "radius": 1.75 * mm});
            skCircle(sketch, "E9.0.10.21", {"center": v(40, 26) * mm, "radius": 1.75 * mm});
            skCircle(sketch, "E9.0.10.22", {"center": v(40, 32) * mm, "radius": 1.75 * mm});
            skCircle(sketch, "E9.0.11.19", {"center": v(34, 14) * mm, "radius": 1.75 * mm});
            skCircle(sketch, "E9.0.11.20", {"center": v(34, 20) * mm, "radius": 1.75 * mm});
            skCircle(sketch, "E9.0.11.21", {"center": v(34, 26) * mm, "radius": 1.75 * mm});
            skCircle(sketch, "E9.0.11.22", {"center": v(34, 32) * mm, "radius": 1.75 * mm});
            skCircle(sketch, "E9.0.12.19", {"center": v(28, 14) * mm, "radius": 1.75 * mm});
            skCircle(sketch, "E9.0.12.20", {"center": v(28, 20) * mm, "radius": 1.75 * mm});
            skCircle(sketch, "E9.0.12.21", {"center": v(28, 26) * mm, "radius": 1.75 * mm});
            skCircle(sketch, "E9.0.12.22", {"center": v(28, 32) * mm, "radius": 1.75 * mm});
            skCircle(sketch, "E9.0.13.19", {"center": v(22, 14) * mm, "radius": 1.75 * mm});
            skCircle(sketch, "E9.0.13.20", {"center": v(22, 20) * mm, "radius": 1.75 * mm});
            skCircle(sketch, "E9.0.13.21", {"center": v(22, 26) * mm, "radius": 1.75 * mm});
            skCircle(sketch, "E9.0.13.22", {"center": v(22, 32) * mm, "radius": 1.75 * mm});
            skCircle(sketch, "E9.0.14.19", {"center": v(16, 14) * mm, "radius": 1.75 * mm});
            skCircle(sketch, "E9.0.14.20", {"center": v(16, 20) * mm, "radius": 1.75 * mm});
            skCircle(sketch, "E9.0.14.21", {"center": v(16, 26) * mm, "radius": 1.75 * mm});
            skCircle(sketch, "E9.0.14.22", {"center": v(16, 32) * mm, "radius": 1.75 * mm});
            skCircle(sketch, "E9.0.15.19", {"center": v(10, 14) * mm, "radius": 1.75 * mm});
            skCircle(sketch, "E9.0.15.20", {"center": v(10, 20) * mm, "radius": 1.75 * mm});
            skCircle(sketch, "E9.0.15.21", {"center": v(10, 26) * mm, "radius": 1.75 * mm});
            skCircle(sketch, "E9.0.15.22", {"center": v(10, 32) * mm, "radius": 1.75 * mm});
            skCircle(sketch, "E9.0.16.19", {"center": v(4, 14) * mm, "radius": 1.75 * mm});
            skCircle(sketch, "E9.0.16.20", {"center": v(4, 20) * mm, "radius": 1.75 * mm});
            skCircle(sketch, "E9.0.16.21", {"center": v(4, 26) * mm, "radius": 1.75 * mm});
            skCircle(sketch, "E9.0.16.22", {"center": v(4, 32) * mm, "radius": 1.75 * mm});
            skCircle(sketch, "E9.0.17.19", {"center": v(-2, 14) * mm, "radius": 1.75 * mm});
            skCircle(sketch, "E9.0.17.20", {"center": v(-2, 20) * mm, "radius": 1.75 * mm});
            skCircle(sketch, "E9.0.17.21", {"center": v(-2, 26) * mm, "radius": 1.75 * mm});
            skCircle(sketch, "E9.0.17.22", {"center": v(-2, 32) * mm, "radius": 1.75 * mm});
            skCircle(sketch, "E9.0.18.19", {"center": v(-8, 14) * mm, "radius": 1.75 * mm});
            skCircle(sketch, "E9.0.18.20", {"center": v(-8, 20) * mm, "radius": 1.75 * mm});
            skCircle(sketch, "E9.0.18.21", {"center": v(-8, 26) * mm, "radius": 1.75 * mm});
            skCircle(sketch, "E9.0.18.22", {"center": v(-8, 32) * mm, "radius": 1.75 * mm});
            skCircle(sketch, "E9.0.19.19", {"center": v(-14, 14) * mm, "radius": 1.75 * mm});
            skCircle(sketch, "E9.0.19.20", {"center": v(-14, 20) * mm, "radius": 1.75 * mm});
            skCircle(sketch, "E9.0.19.21", {"center": v(-14, 26) * mm, "radius": 1.75 * mm});
            skCircle(sketch, "E9.0.19.22", {"center": v(-14, 32) * mm, "radius": 1.75 * mm});
            skCircle(sketch, "E9.0.20.19", {"center": v(-20, 14) * mm, "radius": 1.75 * mm});
            skCircle(sketch, "E9.0.20.20", {"center": v(-20, 20) * mm, "radius": 1.75 * mm});
            skCircle(sketch, "E9.0.20.21", {"center": v(-20, 26) * mm, "radius": 1.75 * mm});
            skCircle(sketch, "E9.0.20.22", {"center": v(-20, 32) * mm, "radius": 1.75 * mm});
            skCircle(sketch, "E9.0.21.19", {"center": v(-26, 14) * mm, "radius": 1.75 * mm});
            skCircle(sketch, "E9.0.21.20", {"center": v(-26, 20) * mm, "radius": 1.75 * mm});
            skCircle(sketch, "E9.0.21.21", {"center": v(-26, 26) * mm, "radius": 1.75 * mm});
            skCircle(sketch, "E9.0.21.22", {"center": v(-26, 32) * mm, "radius": 1.75 * mm});
            skCircle(sketch, "E9.0.22.19", {"center": v(-32, 14) * mm, "radius": 1.75 * mm});
            skCircle(sketch, "E9.0.22.20", {"center": v(-32, 20) * mm, "radius": 1.75 * mm});
            skCircle(sketch, "E9.0.22.21", {"center": v(-32, 26) * mm, "radius": 1.75 * mm});
            skCircle(sketch, "E9.0.22.22", {"center": v(-32, 32) * mm, "radius": 1.75 * mm});
            skCircle(sketch, "E10.0.0.23", {"center": v(100, 38) * mm, "radius": 1.75 * mm});
            skCircle(sketch, "E10.0.0.24", {"center": v(100, 44) * mm, "radius": 1.75 * mm});
            skCircle(sketch, "E10.0.0.25", {"center": v(100, 50) * mm, "radius": 1.75 * mm});
            skCircle(sketch, "E10.0.0.26", {"center": v(100, 56) * mm, "radius": 1.75 * mm});
            skCircle(sketch, "E10.0.0.27", {"center": v(100, 62) * mm, "radius": 1.75 * mm});
            skCircle(sketch, "E10.0.0.28", {"center": v(100, 68) * mm, "radius": 1.75 * mm});
            skCircle(sketch, "E10.0.0.29", {"center": v(100, 74) * mm, "radius": 1.75 * mm});
            skCircle(sketch, "E10.0.1.23", {"center": v(94, 38) * mm, "radius": 1.75 * mm});
            skCircle(sketch, "E10.0.1.24", {"center": v(94, 44) * mm, "radius": 1.75 * mm});
            skCircle(sketch, "E10.0.1.25", {"center": v(94, 50) * mm, "radius": 1.75 * mm});
            skCircle(sketch, "E10.0.1.26", {"center": v(94, 56) * mm, "radius": 1.75 * mm});
            skCircle(sketch, "E10.0.1.27", {"center": v(94, 62) * mm, "radius": 1.75 * mm});
            skCircle(sketch, "E10.0.1.28", {"center": v(94, 68) * mm, "radius": 1.75 * mm});
            skCircle(sketch, "E10.0.1.29", {"center": v(94, 74) * mm, "radius": 1.75 * mm});
            skCircle(sketch, "E10.0.2.23", {"center": v(88, 38) * mm, "radius": 1.75 * mm});
            skCircle(sketch, "E10.0.2.24", {"center": v(88, 44) * mm, "radius": 1.75 * mm});
            skCircle(sketch, "E10.0.2.25", {"center": v(88, 50) * mm, "radius": 1.75 * mm});
            skCircle(sketch, "E10.0.2.26", {"center": v(88, 56) * mm, "radius": 1.75 * mm});
            skCircle(sketch, "E10.0.2.27", {"center": v(88, 62) * mm, "radius": 1.75 * mm});
            skCircle(sketch, "E10.0.2.28", {"center": v(88, 68) * mm, "radius": 1.75 * mm});
            skCircle(sketch, "E10.0.2.29", {"center": v(88, 74) * mm, "radius": 1.75 * mm});
            skCircle(sketch, "E10.0.3.23", {"center": v(82, 38) * mm, "radius": 1.75 * mm});
            skCircle(sketch, "E10.0.3.24", {"center": v(82, 44) * mm, "radius": 1.75 * mm});
            skCircle(sketch, "E10.0.3.25", {"center": v(82, 50) * mm, "radius": 1.75 * mm});
            skCircle(sketch, "E10.0.3.26", {"center": v(82, 56) * mm, "radius": 1.75 * mm});
            skCircle(sketch, "E10.0.3.27", {"center": v(82, 62) * mm, "radius": 1.75 * mm});
            skCircle(sketch, "E10.0.3.28", {"center": v(82, 68) * mm, "radius": 1.75 * mm});
            skCircle(sketch, "E10.0.3.29", {"center": v(82, 74) * mm, "radius": 1.75 * mm});
            skCircle(sketch, "E10.0.4.23", {"center": v(76, 38) * mm, "radius": 1.75 * mm});
            skCircle(sketch, "E10.0.4.24", {"center": v(76, 44) * mm, "radius": 1.75 * mm});
            skCircle(sketch, "E10.0.4.25", {"center": v(76, 50) * mm, "radius": 1.75 * mm});
            skCircle(sketch, "E10.0.4.26", {"center": v(76, 56) * mm, "radius": 1.75 * mm});
            skCircle(sketch, "E10.0.4.27", {"center": v(76, 62) * mm, "radius": 1.75 * mm});
            skCircle(sketch, "E10.0.4.28", {"center": v(76, 68) * mm, "radius": 1.75 * mm});
            skCircle(sketch, "E10.0.4.29", {"center": v(76, 74) * mm, "radius": 1.75 * mm});
            skCircle(sketch, "E10.0.5.23", {"center": v(70, 38) * mm, "radius": 1.75 * mm});
            skCircle(sketch, "E10.0.5.24", {"center": v(70, 44) * mm, "radius": 1.75 * mm});
            skCircle(sketch, "E10.0.5.25", {"center": v(70, 50) * mm, "radius": 1.75 * mm});
            skCircle(sketch, "E10.0.5.26", {"center": v(70, 56) * mm, "radius": 1.75 * mm});
            skCircle(sketch, "E10.0.5.27", {"center": v(70, 62) * mm, "radius": 1.75 * mm});
            skCircle(sketch, "E10.0.5.28", {"center": v(70, 68) * mm, "radius": 1.75 * mm});
            skCircle(sketch, "E10.0.5.29", {"center": v(70, 74) * mm, "radius": 1.75 * mm});
            skCircle(sketch, "E10.0.6.23", {"center": v(64, 38) * mm, "radius": 1.75 * mm});
            skCircle(sketch, "E10.0.6.24", {"center": v(64, 44) * mm, "radius": 1.75 * mm});
            skCircle(sketch, "E10.0.6.25", {"center": v(64, 50) * mm, "radius": 1.75 * mm});
            skCircle(sketch, "E10.0.6.26", {"center": v(64, 56) * mm, "radius": 1.75 * mm});
            skCircle(sketch, "E10.0.6.27", {"center": v(64, 62) * mm, "radius": 1.75 * mm});
            skCircle(sketch, "E10.0.6.28", {"center": v(64, 68) * mm, "radius": 1.75 * mm});
            skCircle(sketch, "E10.0.6.29", {"center": v(64, 74) * mm, "radius": 1.75 * mm});
            skCircle(sketch, "E10.0.7.23", {"center": v(58, 38) * mm, "radius": 1.75 * mm});
            skCircle(sketch, "E10.0.7.24", {"center": v(58, 44) * mm, "radius": 1.75 * mm});
            skCircle(sketch, "E10.0.7.25", {"center": v(58, 50) * mm, "radius": 1.75 * mm});
            skCircle(sketch, "E10.0.7.26", {"center": v(58, 56) * mm, "radius": 1.75 * mm});
            skCircle(sketch, "E10.0.7.27", {"center": v(58, 62) * mm, "radius": 1.75 * mm});
            skCircle(sketch, "E10.0.7.28", {"center": v(58, 68) * mm, "radius": 1.75 * mm});
            skCircle(sketch, "E10.0.7.29", {"center": v(58, 74) * mm, "radius": 1.75 * mm});
            skCircle(sketch, "E10.0.8.23", {"center": v(52, 38) * mm, "radius": 1.75 * mm});
            skCircle(sketch, "E10.0.8.24", {"center": v(52, 44) * mm, "radius": 1.75 * mm});
            skCircle(sketch, "E10.0.8.25", {"center": v(52, 50) * mm, "radius": 1.75 * mm});
            skCircle(sketch, "E10.0.8.26", {"center": v(52, 56) * mm, "radius": 1.75 * mm});
            skCircle(sketch, "E10.0.8.27", {"center": v(52, 62) * mm, "radius": 1.75 * mm});
            skCircle(sketch, "E10.0.8.28", {"center": v(52, 68) * mm, "radius": 1.75 * mm});
            skCircle(sketch, "E10.0.8.29", {"center": v(52, 74) * mm, "radius": 1.75 * mm});
            skCircle(sketch, "E10.0.9.23", {"center": v(46, 38) * mm, "radius": 1.75 * mm});
            skCircle(sketch, "E10.0.9.24", {"center": v(46, 44) * mm, "radius": 1.75 * mm});
            skCircle(sketch, "E10.0.9.25", {"center": v(46, 50) * mm, "radius": 1.75 * mm});
            skCircle(sketch, "E10.0.9.26", {"center": v(46, 56) * mm, "radius": 1.75 * mm});
            skCircle(sketch, "E10.0.9.27", {"center": v(46, 62) * mm, "radius": 1.75 * mm});
            skCircle(sketch, "E10.0.9.28", {"center": v(46, 68) * mm, "radius": 1.75 * mm});
            skCircle(sketch, "E10.0.9.29", {"center": v(46, 74) * mm, "radius": 1.75 * mm});
            skCircle(sketch, "E10.0.10.23", {"center": v(40, 38) * mm, "radius": 1.75 * mm});
            skCircle(sketch, "E10.0.10.24", {"center": v(40, 44) * mm, "radius": 1.75 * mm});
            skCircle(sketch, "E10.0.10.25", {"center": v(40, 50) * mm, "radius": 1.75 * mm});
            skCircle(sketch, "E10.0.10.26", {"center": v(40, 56) * mm, "radius": 1.75 * mm});
            skCircle(sketch, "E10.0.10.27", {"center": v(40, 62) * mm, "radius": 1.75 * mm});
            skCircle(sketch, "E10.0.10.28", {"center": v(40, 68) * mm, "radius": 1.75 * mm});
            skCircle(sketch, "E10.0.10.29", {"center": v(40, 74) * mm, "radius": 1.75 * mm});
            skCircle(sketch, "E10.0.11.23", {"center": v(34, 38) * mm, "radius": 1.75 * mm});
            skCircle(sketch, "E10.0.11.24", {"center": v(34, 44) * mm, "radius": 1.75 * mm});
            skCircle(sketch, "E10.0.11.25", {"center": v(34, 50) * mm, "radius": 1.75 * mm});
            skCircle(sketch, "E10.0.11.26", {"center": v(34, 56) * mm, "radius": 1.75 * mm});
            skCircle(sketch, "E10.0.11.27", {"center": v(34, 62) * mm, "radius": 1.75 * mm});
            skCircle(sketch, "E10.0.11.28", {"center": v(34, 68) * mm, "radius": 1.75 * mm});
            skCircle(sketch, "E10.0.11.29", {"center": v(34, 74) * mm, "radius": 1.75 * mm});
            skCircle(sketch, "E10.0.12.23", {"center": v(28, 38) * mm, "radius": 1.75 * mm});
            skCircle(sketch, "E10.0.12.24", {"center": v(28, 44) * mm, "radius": 1.75 * mm});
            skCircle(sketch, "E10.0.12.25", {"center": v(28, 50) * mm, "radius": 1.75 * mm});
            skCircle(sketch, "E10.0.12.26", {"center": v(28, 56) * mm, "radius": 1.75 * mm});
            skCircle(sketch, "E10.0.12.27", {"center": v(28, 62) * mm, "radius": 1.75 * mm});
            skCircle(sketch, "E10.0.12.28", {"center": v(28, 68) * mm, "radius": 1.75 * mm});
            skCircle(sketch, "E10.0.12.29", {"center": v(28, 74) * mm, "radius": 1.75 * mm});
            skCircle(sketch, "E10.0.13.23", {"center": v(22, 38) * mm, "radius": 1.75 * mm});
            skCircle(sketch, "E10.0.13.24", {"center": v(22, 44) * mm, "radius": 1.75 * mm});
            skCircle(sketch, "E10.0.13.25", {"center": v(22, 50) * mm, "radius": 1.75 * mm});
            skCircle(sketch, "E10.0.13.26", {"center": v(22, 56) * mm, "radius": 1.75 * mm});
            skCircle(sketch, "E10.0.13.27", {"center": v(22, 62) * mm, "radius": 1.75 * mm});
            skCircle(sketch, "E10.0.13.28", {"center": v(22, 68) * mm, "radius": 1.75 * mm});
            skCircle(sketch, "E10.0.13.29", {"center": v(22, 74) * mm, "radius": 1.75 * mm});
            skCircle(sketch, "E10.0.14.23", {"center": v(16, 38) * mm, "radius": 1.75 * mm});
            skCircle(sketch, "E10.0.14.24", {"center": v(16, 44) * mm, "radius": 1.75 * mm});
            skCircle(sketch, "E10.0.14.25", {"center": v(16, 50) * mm, "radius": 1.75 * mm});
            skCircle(sketch, "E10.0.14.26", {"center": v(16, 56) * mm, "radius": 1.75 * mm});
            skCircle(sketch, "E10.0.14.27", {"center": v(16, 62) * mm, "radius": 1.75 * mm});
            skCircle(sketch, "E10.0.14.28", {"center": v(16, 68) * mm, "radius": 1.75 * mm});
            skCircle(sketch, "E10.0.14.29", {"center": v(16, 74) * mm, "radius": 1.75 * mm});
            skCircle(sketch, "E10.0.15.23", {"center": v(10, 38) * mm, "radius": 1.75 * mm});
            skCircle(sketch, "E10.0.15.24", {"center": v(10, 44) * mm, "radius": 1.75 * mm});
            skCircle(sketch, "E10.0.15.25", {"center": v(10, 50) * mm, "radius": 1.75 * mm});
            skCircle(sketch, "E10.0.15.26", {"center": v(10, 56) * mm, "radius": 1.75 * mm});
            skCircle(sketch, "E10.0.15.27", {"center": v(10, 62) * mm, "radius": 1.75 * mm});
            skCircle(sketch, "E10.0.15.28", {"center": v(10, 68) * mm, "radius": 1.75 * mm});
            skCircle(sketch, "E10.0.15.29", {"center": v(10, 74) * mm, "radius": 1.75 * mm});
            skCircle(sketch, "E10.0.16.23", {"center": v(4, 38) * mm, "radius": 1.75 * mm});
            skCircle(sketch, "E10.0.16.24", {"center": v(4, 44) * mm, "radius": 1.75 * mm});
            skCircle(sketch, "E10.0.16.25", {"center": v(4, 50) * mm, "radius": 1.75 * mm});
            skCircle(sketch, "E10.0.16.26", {"center": v(4, 56) * mm, "radius": 1.75 * mm});
            skCircle(sketch, "E10.0.16.27", {"center": v(4, 62) * mm, "radius": 1.75 * mm});
            skCircle(sketch, "E10.0.16.28", {"center": v(4, 68) * mm, "radius": 1.75 * mm});
            skCircle(sketch, "E10.0.16.29", {"center": v(4, 74) * mm, "radius": 1.75 * mm});
            skCircle(sketch, "E10.0.17.23", {"center": v(-2, 38) * mm, "radius": 1.75 * mm});
            skCircle(sketch, "E10.0.17.24", {"center": v(-2, 44) * mm, "radius": 1.75 * mm});
            skCircle(sketch, "E10.0.17.25", {"center": v(-2, 50) * mm, "radius": 1.75 * mm});
            skCircle(sketch, "E10.0.17.26", {"center": v(-2, 56) * mm, "radius": 1.75 * mm});
            skCircle(sketch, "E10.0.17.27", {"center": v(-2, 62) * mm, "radius": 1.75 * mm});
            skCircle(sketch, "E10.0.17.28", {"center": v(-2, 68) * mm, "radius": 1.75 * mm});
            skCircle(sketch, "E10.0.17.29", {"center": v(-2, 74) * mm, "radius": 1.75 * mm});
            skCircle(sketch, "E10.0.18.23", {"center": v(-8, 38) * mm, "radius": 1.75 * mm});
            skCircle(sketch, "E10.0.18.24", {"center": v(-8, 44) * mm, "radius": 1.75 * mm});
            skCircle(sketch, "E10.0.18.25", {"center": v(-8, 50) * mm, "radius": 1.75 * mm});
            skCircle(sketch, "E10.0.18.26", {"center": v(-8, 56) * mm, "radius": 1.75 * mm});
            skCircle(sketch, "E10.0.18.27", {"center": v(-8, 62) * mm, "radius": 1.75 * mm});
            skCircle(sketch, "E10.0.18.28", {"center": v(-8, 68) * mm, "radius": 1.75 * mm});
            skCircle(sketch, "E10.0.18.29", {"center": v(-8, 74) * mm, "radius": 1.75 * mm});
            skCircle(sketch, "E10.0.19.23", {"center": v(-14, 38) * mm, "radius": 1.75 * mm});
            skCircle(sketch, "E10.0.19.24", {"center": v(-14, 44) * mm, "radius": 1.75 * mm});
            skCircle(sketch, "E10.0.19.25", {"center": v(-14, 50) * mm, "radius": 1.75 * mm});
            skCircle(sketch, "E10.0.19.26", {"center": v(-14, 56) * mm, "radius": 1.75 * mm});
            skCircle(sketch, "E10.0.19.27", {"center": v(-14, 62) * mm, "radius": 1.75 * mm});
            skCircle(sketch, "E10.0.19.28", {"center": v(-14, 68) * mm, "radius": 1.75 * mm});
            skCircle(sketch, "E10.0.19.29", {"center": v(-14, 74) * mm, "radius": 1.75 * mm});
            skCircle(sketch, "E10.0.20.23", {"center": v(-20, 38) * mm, "radius": 1.75 * mm});
            skCircle(sketch, "E10.0.20.24", {"center": v(-20, 44) * mm, "radius": 1.75 * mm});
            skCircle(sketch, "E10.0.20.25", {"center": v(-20, 50) * mm, "radius": 1.75 * mm});
            skCircle(sketch, "E10.0.20.26", {"center": v(-20, 56) * mm, "radius": 1.75 * mm});
            skCircle(sketch, "E10.0.20.27", {"center": v(-20, 62) * mm, "radius": 1.75 * mm});
            skCircle(sketch, "E10.0.20.28", {"center": v(-20, 68) * mm, "radius": 1.75 * mm});
            skCircle(sketch, "E10.0.20.29", {"center": v(-20, 74) * mm, "radius": 1.75 * mm});
            skCircle(sketch, "E10.0.21.23", {"center": v(-26, 38) * mm, "radius": 1.75 * mm});
            skCircle(sketch, "E10.0.21.24", {"center": v(-26, 44) * mm, "radius": 1.75 * mm});
            skCircle(sketch, "E10.0.21.25", {"center": v(-26, 50) * mm, "radius": 1.75 * mm});
            skCircle(sketch, "E10.0.21.26", {"center": v(-26, 56) * mm, "radius": 1.75 * mm});
            skCircle(sketch, "E10.0.21.27", {"center": v(-26, 62) * mm, "radius": 1.75 * mm});
            skCircle(sketch, "E10.0.21.28", {"center": v(-26, 68) * mm, "radius": 1.75 * mm});
            skCircle(sketch, "E10.0.21.29", {"center": v(-26, 74) * mm, "radius": 1.75 * mm});
            skCircle(sketch, "E10.0.22.23", {"center": v(-32, 38) * mm, "radius": 1.75 * mm});
            skCircle(sketch, "E10.0.22.24", {"center": v(-32, 44) * mm, "radius": 1.75 * mm});
            skCircle(sketch, "E10.0.22.25", {"center": v(-32, 50) * mm, "radius": 1.75 * mm});
            skCircle(sketch, "E10.0.22.26", {"center": v(-32, 56) * mm, "radius": 1.75 * mm});
            skCircle(sketch, "E10.0.22.27", {"center": v(-32, 62) * mm, "radius": 1.75 * mm});
            skCircle(sketch, "E10.0.22.28", {"center": v(-32, 68) * mm, "radius": 1.75 * mm});
            skCircle(sketch, "E10.0.22.29", {"center": v(-32, 74) * mm, "radius": 1.75 * mm});
            skCircle(sketch, "E11.0.23.0", {"center": v(-38, -100) * mm, "radius": 1.75 * mm});
            skCircle(sketch, "E11.0.23.1", {"center": v(-38, -94) * mm, "radius": 1.75 * mm});
            skCircle(sketch, "E11.0.23.2", {"center": v(-38, -88) * mm, "radius": 1.75 * mm});
            skCircle(sketch, "E11.0.23.3", {"center": v(-38, -82) * mm, "radius": 1.75 * mm});
            skCircle(sketch, "E11.0.23.4", {"center": v(-38, -76) * mm, "radius": 1.75 * mm});
            skCircle(sketch, "E11.0.23.5", {"center": v(-38, -70) * mm, "radius": 1.75 * mm});
            skCircle(sketch, "E11.0.23.6", {"center": v(-38, -64) * mm, "radius": 1.75 * mm});
            skCircle(sketch, "E11.0.23.7", {"center": v(-38, -58) * mm, "radius": 1.75 * mm});
            skCircle(sketch, "E11.0.23.8", {"center": v(-38, -52) * mm, "radius": 1.75 * mm});
            skCircle(sketch, "E11.0.23.9", {"center": v(-38, -46) * mm, "radius": 1.75 * mm});
            skCircle(sketch, "E11.0.23.10", {"center": v(-38, -40) * mm, "radius": 1.75 * mm});
            skCircle(sketch, "E11.0.23.11", {"center": v(-38, -34) * mm, "radius": 1.75 * mm});
            skCircle(sketch, "E11.0.23.12", {"center": v(-38, -28) * mm, "radius": 1.75 * mm});
            skCircle(sketch, "E11.0.23.13", {"center": v(-38, -22) * mm, "radius": 1.75 * mm});
            skCircle(sketch, "E11.0.23.14", {"center": v(-38, -16) * mm, "radius": 1.75 * mm});
            skCircle(sketch, "E11.0.23.15", {"center": v(-38, -10) * mm, "radius": 1.75 * mm});
            skCircle(sketch, "E11.0.23.16", {"center": v(-38, -4) * mm, "radius": 1.75 * mm});
            skCircle(sketch, "E11.0.23.17", {"center": v(-38, 2) * mm, "radius": 1.75 * mm});
            skCircle(sketch, "E11.0.23.18", {"center": v(-38, 8) * mm, "radius": 1.75 * mm});
            skCircle(sketch, "E11.0.23.19", {"center": v(-38, 14) * mm, "radius": 1.75 * mm});
            skCircle(sketch, "E11.0.23.20", {"center": v(-38, 20) * mm, "radius": 1.75 * mm});
            skCircle(sketch, "E11.0.23.21", {"center": v(-38, 26) * mm, "radius": 1.75 * mm});
            skCircle(sketch, "E11.0.23.22", {"center": v(-38, 32) * mm, "radius": 1.75 * mm});
            skCircle(sketch, "E11.0.23.23", {"center": v(-38, 38) * mm, "radius": 1.75 * mm});
            skCircle(sketch, "E11.0.23.24", {"center": v(-38, 44) * mm, "radius": 1.75 * mm});
            skCircle(sketch, "E11.0.23.25", {"center": v(-38, 50) * mm, "radius": 1.75 * mm});
            skCircle(sketch, "E11.0.23.26", {"center": v(-38, 56) * mm, "radius": 1.75 * mm});
            skCircle(sketch, "E11.0.23.27", {"center": v(-38, 62) * mm, "radius": 1.75 * mm});
            skCircle(sketch, "E11.0.23.28", {"center": v(-38, 68) * mm, "radius": 1.75 * mm});
            skCircle(sketch, "E11.0.23.29", {"center": v(-38, 74) * mm, "radius": 1.75 * mm});
            skCircle(sketch, "E11.0.24.0", {"center": v(-44, -100) * mm, "radius": 1.75 * mm});
            skCircle(sketch, "E11.0.24.1", {"center": v(-44, -94) * mm, "radius": 1.75 * mm});
            skCircle(sketch, "E11.0.24.2", {"center": v(-44, -88) * mm, "radius": 1.75 * mm});
            skCircle(sketch, "E11.0.24.3", {"center": v(-44, -82) * mm, "radius": 1.75 * mm});
            skCircle(sketch, "E11.0.24.4", {"center": v(-44, -76) * mm, "radius": 1.75 * mm});
            skCircle(sketch, "E11.0.24.5", {"center": v(-44, -70) * mm, "radius": 1.75 * mm});
            skCircle(sketch, "E11.0.24.6", {"center": v(-44, -64) * mm, "radius": 1.75 * mm});
            skCircle(sketch, "E11.0.24.7", {"center": v(-44, -58) * mm, "radius": 1.75 * mm});
            skCircle(sketch, "E11.0.24.8", {"center": v(-44, -52) * mm, "radius": 1.75 * mm});
            skCircle(sketch, "E11.0.24.9", {"center": v(-44, -46) * mm, "radius": 1.75 * mm});
            skCircle(sketch, "E11.0.24.10", {"center": v(-44, -40) * mm, "radius": 1.75 * mm});
            skCircle(sketch, "E11.0.24.11", {"center": v(-44, -34) * mm, "radius": 1.75 * mm});
            skCircle(sketch, "E11.0.24.12", {"center": v(-44, -28) * mm, "radius": 1.75 * mm});
            skCircle(sketch, "E11.0.24.13", {"center": v(-44, -22) * mm, "radius": 1.75 * mm});
            skCircle(sketch, "E11.0.24.14", {"center": v(-44, -16) * mm, "radius": 1.75 * mm});
            skCircle(sketch, "E11.0.24.15", {"center": v(-44, -10) * mm, "radius": 1.75 * mm});
            skCircle(sketch, "E11.0.24.16", {"center": v(-44, -4) * mm, "radius": 1.75 * mm});
            skCircle(sketch, "E11.0.24.17", {"center": v(-44, 2) * mm, "radius": 1.75 * mm});
            skCircle(sketch, "E11.0.24.18", {"center": v(-44, 8) * mm, "radius": 1.75 * mm});
            skCircle(sketch, "E11.0.24.19", {"center": v(-44, 14) * mm, "radius": 1.75 * mm});
            skCircle(sketch, "E11.0.24.20", {"center": v(-44, 20) * mm, "radius": 1.75 * mm});
            skCircle(sketch, "E11.0.24.21", {"center": v(-44, 26) * mm, "radius": 1.75 * mm});
            skCircle(sketch, "E11.0.24.22", {"center": v(-44, 32) * mm, "radius": 1.75 * mm});
            skCircle(sketch, "E11.0.24.23", {"center": v(-44, 38) * mm, "radius": 1.75 * mm});
            skCircle(sketch, "E11.0.24.24", {"center": v(-44, 44) * mm, "radius": 1.75 * mm});
            skCircle(sketch, "E11.0.24.25", {"center": v(-44, 50) * mm, "radius": 1.75 * mm});
            skCircle(sketch, "E11.0.24.26", {"center": v(-44, 56) * mm, "radius": 1.75 * mm});
            skCircle(sketch, "E11.0.24.27", {"center": v(-44, 62) * mm, "radius": 1.75 * mm});
            skCircle(sketch, "E11.0.24.28", {"center": v(-44, 68) * mm, "radius": 1.75 * mm});
            skCircle(sketch, "E11.0.24.29", {"center": v(-44, 74) * mm, "radius": 1.75 * mm});
            skCircle(sketch, "E11.0.25.0", {"center": v(-50, -100) * mm, "radius": 1.75 * mm});
            skCircle(sketch, "E11.0.25.1", {"center": v(-50, -94) * mm, "radius": 1.75 * mm});
            skCircle(sketch, "E11.0.25.2", {"center": v(-50, -88) * mm, "radius": 1.75 * mm});
            skCircle(sketch, "E11.0.25.3", {"center": v(-50, -82) * mm, "radius": 1.75 * mm});
            skCircle(sketch, "E11.0.25.4", {"center": v(-50, -76) * mm, "radius": 1.75 * mm});
            skCircle(sketch, "E11.0.25.5", {"center": v(-50, -70) * mm, "radius": 1.75 * mm});
            skCircle(sketch, "E11.0.25.6", {"center": v(-50, -64) * mm, "radius": 1.75 * mm});
            skCircle(sketch, "E11.0.25.7", {"center": v(-50, -58) * mm, "radius": 1.75 * mm});
            skCircle(sketch, "E11.0.25.8", {"center": v(-50, -52) * mm, "radius": 1.75 * mm});
            skCircle(sketch, "E11.0.25.9", {"center": v(-50, -46) * mm, "radius": 1.75 * mm});
            skCircle(sketch, "E11.0.25.10", {"center": v(-50, -40) * mm, "radius": 1.75 * mm});
            skCircle(sketch, "E11.0.25.11", {"center": v(-50, -34) * mm, "radius": 1.75 * mm});
            skCircle(sketch, "E11.0.25.12", {"center": v(-50, -28) * mm, "radius": 1.75 * mm});
            skCircle(sketch, "E11.0.25.13", {"center": v(-50, -22) * mm, "radius": 1.75 * mm});
            skCircle(sketch, "E11.0.25.14", {"center": v(-50, -16) * mm, "radius": 1.75 * mm});
            skCircle(sketch, "E11.0.25.15", {"center": v(-50, -10) * mm, "radius": 1.75 * mm});
            skCircle(sketch, "E11.0.25.16", {"center": v(-50, -4) * mm, "radius": 1.75 * mm});
            skCircle(sketch, "E11.0.25.17", {"center": v(-50, 2) * mm, "radius": 1.75 * mm});
            skCircle(sketch, "E11.0.25.18", {"center": v(-50, 8) * mm, "radius": 1.75 * mm});
            skCircle(sketch, "E11.0.25.19", {"center": v(-50, 14) * mm, "radius": 1.75 * mm});
            skCircle(sketch, "E11.0.25.20", {"center": v(-50, 20) * mm, "radius": 1.75 * mm});
            skCircle(sketch, "E11.0.25.21", {"center": v(-50, 26) * mm, "radius": 1.75 * mm});
            skCircle(sketch, "E11.0.25.22", {"center": v(-50, 32) * mm, "radius": 1.75 * mm});
            skCircle(sketch, "E11.0.25.23", {"center": v(-50, 38) * mm, "radius": 1.75 * mm});
            skCircle(sketch, "E11.0.25.24", {"center": v(-50, 44) * mm, "radius": 1.75 * mm});
            skCircle(sketch, "E11.0.25.25", {"center": v(-50, 50) * mm, "radius": 1.75 * mm});
            skCircle(sketch, "E11.0.25.26", {"center": v(-50, 56) * mm, "radius": 1.75 * mm});
            skCircle(sketch, "E11.0.25.27", {"center": v(-50, 62) * mm, "radius": 1.75 * mm});
            skCircle(sketch, "E11.0.25.28", {"center": v(-50, 68) * mm, "radius": 1.75 * mm});
            skCircle(sketch, "E11.0.25.29", {"center": v(-50, 74) * mm, "radius": 1.75 * mm});
            skCircle(sketch, "E11.0.26.0", {"center": v(-56, -100) * mm, "radius": 1.75 * mm});
            skCircle(sketch, "E11.0.26.1", {"center": v(-56, -94) * mm, "radius": 1.75 * mm});
            skCircle(sketch, "E11.0.26.2", {"center": v(-56, -88) * mm, "radius": 1.75 * mm});
            skCircle(sketch, "E11.0.26.3", {"center": v(-56, -82) * mm, "radius": 1.75 * mm});
            skCircle(sketch, "E11.0.26.4", {"center": v(-56, -76) * mm, "radius": 1.75 * mm});
            skCircle(sketch, "E11.0.26.5", {"center": v(-56, -70) * mm, "radius": 1.75 * mm});
            skCircle(sketch, "E11.0.26.6", {"center": v(-56, -64) * mm, "radius": 1.75 * mm});
            skCircle(sketch, "E11.0.26.7", {"center": v(-56, -58) * mm, "radius": 1.75 * mm});
            skCircle(sketch, "E11.0.26.8", {"center": v(-56, -52) * mm, "radius": 1.75 * mm});
            skCircle(sketch, "E11.0.26.9", {"center": v(-56, -46) * mm, "radius": 1.75 * mm});
            skCircle(sketch, "E11.0.26.10", {"center": v(-56, -40) * mm, "radius": 1.75 * mm});
            skCircle(sketch, "E11.0.26.11", {"center": v(-56, -34) * mm, "radius": 1.75 * mm});
            skCircle(sketch, "E11.0.26.12", {"center": v(-56, -28) * mm, "radius": 1.75 * mm});
            skCircle(sketch, "E11.0.26.13", {"center": v(-56, -22) * mm, "radius": 1.75 * mm});
            skCircle(sketch, "E11.0.26.14", {"center": v(-56, -16) * mm, "radius": 1.75 * mm});
            skCircle(sketch, "E11.0.26.15", {"center": v(-56, -10) * mm, "radius": 1.75 * mm});
            skCircle(sketch, "E11.0.26.16", {"center": v(-56, -4) * mm, "radius": 1.75 * mm});
            skCircle(sketch, "E11.0.26.17", {"center": v(-56, 2) * mm, "radius": 1.75 * mm});
            skCircle(sketch, "E11.0.26.18", {"center": v(-56, 8) * mm, "radius": 1.75 * mm});
            skCircle(sketch, "E11.0.26.19", {"center": v(-56, 14) * mm, "radius": 1.75 * mm});
            skCircle(sketch, "E11.0.26.20", {"center": v(-56, 20) * mm, "radius": 1.75 * mm});
            skCircle(sketch, "E11.0.26.21", {"center": v(-56, 26) * mm, "radius": 1.75 * mm});
            skCircle(sketch, "E11.0.26.22", {"center": v(-56, 32) * mm, "radius": 1.75 * mm});
            skCircle(sketch, "E11.0.26.23", {"center": v(-56, 38) * mm, "radius": 1.75 * mm});
            skCircle(sketch, "E11.0.26.24", {"center": v(-56, 44) * mm, "radius": 1.75 * mm});
            skCircle(sketch, "E11.0.26.25", {"center": v(-56, 50) * mm, "radius": 1.75 * mm});
            skCircle(sketch, "E11.0.26.26", {"center": v(-56, 56) * mm, "radius": 1.75 * mm});
            skCircle(sketch, "E11.0.26.27", {"center": v(-56, 62) * mm, "radius": 1.75 * mm});
            skCircle(sketch, "E11.0.26.28", {"center": v(-56, 68) * mm, "radius": 1.75 * mm});
            skCircle(sketch, "E11.0.26.29", {"center": v(-56, 74) * mm, "radius": 1.75 * mm});
            skCircle(sketch, "E11.0.27.0", {"center": v(-62, -100) * mm, "radius": 1.75 * mm});
            skCircle(sketch, "E11.0.27.1", {"center": v(-62, -94) * mm, "radius": 1.75 * mm});
            skCircle(sketch, "E11.0.27.2", {"center": v(-62, -88) * mm, "radius": 1.75 * mm});
            skCircle(sketch, "E11.0.27.3", {"center": v(-62, -82) * mm, "radius": 1.75 * mm});
            skCircle(sketch, "E11.0.27.4", {"center": v(-62, -76) * mm, "radius": 1.75 * mm});
            skCircle(sketch, "E11.0.27.5", {"center": v(-62, -70) * mm, "radius": 1.75 * mm});
            skCircle(sketch, "E11.0.27.6", {"center": v(-62, -64) * mm, "radius": 1.75 * mm});
            skCircle(sketch, "E11.0.27.7", {"center": v(-62, -58) * mm, "radius": 1.75 * mm});
            skCircle(sketch, "E11.0.27.8", {"center": v(-62, -52) * mm, "radius": 1.75 * mm});
            skCircle(sketch, "E11.0.27.9", {"center": v(-62, -46) * mm, "radius": 1.75 * mm});
            skCircle(sketch, "E11.0.27.10", {"center": v(-62, -40) * mm, "radius": 1.75 * mm});
            skCircle(sketch, "E11.0.27.11", {"center": v(-62, -34) * mm, "radius": 1.75 * mm});
            skCircle(sketch, "E11.0.27.12", {"center": v(-62, -28) * mm, "radius": 1.75 * mm});
            skCircle(sketch, "E11.0.27.13", {"center": v(-62, -22) * mm, "radius": 1.75 * mm});
            skCircle(sketch, "E11.0.27.14", {"center": v(-62, -16) * mm, "radius": 1.75 * mm});
            skCircle(sketch, "E11.0.27.15", {"center": v(-62, -10) * mm, "radius": 1.75 * mm});
            skCircle(sketch, "E11.0.27.16", {"center": v(-62, -4) * mm, "radius": 1.75 * mm});
            skCircle(sketch, "E11.0.27.17", {"center": v(-62, 2) * mm, "radius": 1.75 * mm});
            skCircle(sketch, "E11.0.27.18", {"center": v(-62, 8) * mm, "radius": 1.75 * mm});
            skCircle(sketch, "E11.0.27.19", {"center": v(-62, 14) * mm, "radius": 1.75 * mm});
            skCircle(sketch, "E11.0.27.20", {"center": v(-62, 20) * mm, "radius": 1.75 * mm});
            skCircle(sketch, "E11.0.27.21", {"center": v(-62, 26) * mm, "radius": 1.75 * mm});
            skCircle(sketch, "E11.0.27.22", {"center": v(-62, 32) * mm, "radius": 1.75 * mm});
            skCircle(sketch, "E11.0.27.23", {"center": v(-62, 38) * mm, "radius": 1.75 * mm});
            skCircle(sketch, "E11.0.27.24", {"center": v(-62, 44) * mm, "radius": 1.75 * mm});
            skCircle(sketch, "E11.0.27.25", {"center": v(-62, 50) * mm, "radius": 1.75 * mm});
            skCircle(sketch, "E11.0.27.26", {"center": v(-62, 56) * mm, "radius": 1.75 * mm});
            skCircle(sketch, "E11.0.27.27", {"center": v(-62, 62) * mm, "radius": 1.75 * mm});
            skCircle(sketch, "E11.0.27.28", {"center": v(-62, 68) * mm, "radius": 1.75 * mm});
            skCircle(sketch, "E11.0.27.29", {"center": v(-62, 74) * mm, "radius": 1.75 * mm});
            skCircle(sketch, "E11.0.28.0", {"center": v(-68, -100) * mm, "radius": 1.75 * mm});
            skCircle(sketch, "E11.0.28.1", {"center": v(-68, -94) * mm, "radius": 1.75 * mm});
            skCircle(sketch, "E11.0.28.2", {"center": v(-68, -88) * mm, "radius": 1.75 * mm});
            skCircle(sketch, "E11.0.28.3", {"center": v(-68, -82) * mm, "radius": 1.75 * mm});
            skCircle(sketch, "E11.0.28.4", {"center": v(-68, -76) * mm, "radius": 1.75 * mm});
            skCircle(sketch, "E11.0.28.5", {"center": v(-68, -70) * mm, "radius": 1.75 * mm});
            skCircle(sketch, "E11.0.28.6", {"center": v(-68, -64) * mm, "radius": 1.75 * mm});
            skCircle(sketch, "E11.0.28.7", {"center": v(-68, -58) * mm, "radius": 1.75 * mm});
            skCircle(sketch, "E11.0.28.8", {"center": v(-68, -52) * mm, "radius": 1.75 * mm});
            skCircle(sketch, "E11.0.28.9", {"center": v(-68, -46) * mm, "radius": 1.75 * mm});
            skCircle(sketch, "E11.0.28.10", {"center": v(-68, -40) * mm, "radius": 1.75 * mm});
            skCircle(sketch, "E11.0.28.11", {"center": v(-68, -34) * mm, "radius": 1.75 * mm});
            skCircle(sketch, "E11.0.28.12", {"center": v(-68, -28) * mm, "radius": 1.75 * mm});
            skCircle(sketch, "E11.0.28.13", {"center": v(-68, -22) * mm, "radius": 1.75 * mm});
            skCircle(sketch, "E11.0.28.14", {"center": v(-68, -16) * mm, "radius": 1.75 * mm});
            skCircle(sketch, "E11.0.28.15", {"center": v(-68, -10) * mm, "radius": 1.75 * mm});
            skCircle(sketch, "E11.0.28.16", {"center": v(-68, -4) * mm, "radius": 1.75 * mm});
            skCircle(sketch, "E11.0.28.17", {"center": v(-68, 2) * mm, "radius": 1.75 * mm});
            skCircle(sketch, "E11.0.28.18", {"center": v(-68, 8) * mm, "radius": 1.75 * mm});
            skCircle(sketch, "E11.0.28.19", {"center": v(-68, 14) * mm, "radius": 1.75 * mm});
            skCircle(sketch, "E11.0.28.20", {"center": v(-68, 20) * mm, "radius": 1.75 * mm});
            skCircle(sketch, "E11.0.28.21", {"center": v(-68, 26) * mm, "radius": 1.75 * mm});
            skCircle(sketch, "E11.0.28.22", {"center": v(-68, 32) * mm, "radius": 1.75 * mm});
            skCircle(sketch, "E11.0.28.23", {"center": v(-68, 38) * mm, "radius": 1.75 * mm});
            skCircle(sketch, "E11.0.28.24", {"center": v(-68, 44) * mm, "radius": 1.75 * mm});
            skCircle(sketch, "E11.0.28.25", {"center": v(-68, 50) * mm, "radius": 1.75 * mm});
            skCircle(sketch, "E11.0.28.26", {"center": v(-68, 56) * mm, "radius": 1.75 * mm});
            skCircle(sketch, "E11.0.28.27", {"center": v(-68, 62) * mm, "radius": 1.75 * mm});
            skCircle(sketch, "E11.0.28.28", {"center": v(-68, 68) * mm, "radius": 1.75 * mm});
            skCircle(sketch, "E11.0.28.29", {"center": v(-68, 74) * mm, "radius": 1.75 * mm});
            skCircle(sketch, "E11.0.29.0", {"center": v(-74, -100) * mm, "radius": 1.75 * mm});
            skCircle(sketch, "E11.0.29.1", {"center": v(-74, -94) * mm, "radius": 1.75 * mm});
            skCircle(sketch, "E11.0.29.2", {"center": v(-74, -88) * mm, "radius": 1.75 * mm});
            skCircle(sketch, "E11.0.29.3", {"center": v(-74, -82) * mm, "radius": 1.75 * mm});
            skCircle(sketch, "E11.0.29.4", {"center": v(-74, -76) * mm, "radius": 1.75 * mm});
            skCircle(sketch, "E11.0.29.5", {"center": v(-74, -70) * mm, "radius": 1.75 * mm});
            skCircle(sketch, "E11.0.29.6", {"center": v(-74, -64) * mm, "radius": 1.75 * mm});
            skCircle(sketch, "E11.0.29.7", {"center": v(-74, -58) * mm, "radius": 1.75 * mm});
            skCircle(sketch, "E11.0.29.8", {"center": v(-74, -52) * mm, "radius": 1.75 * mm});
            skCircle(sketch, "E11.0.29.9", {"center": v(-74, -46) * mm, "radius": 1.75 * mm});
            skCircle(sketch, "E11.0.29.10", {"center": v(-74, -40) * mm, "radius": 1.75 * mm});
            skCircle(sketch, "E11.0.29.11", {"center": v(-74, -34) * mm, "radius": 1.75 * mm});
            skCircle(sketch, "E11.0.29.12", {"center": v(-74, -28) * mm, "radius": 1.75 * mm});
            skCircle(sketch, "E11.0.29.13", {"center": v(-74, -22) * mm, "radius": 1.75 * mm});
            skCircle(sketch, "E11.0.29.14", {"center": v(-74, -16) * mm, "radius": 1.75 * mm});
            skCircle(sketch, "E11.0.29.15", {"center": v(-74, -10) * mm, "radius": 1.75 * mm});
            skCircle(sketch, "E11.0.29.16", {"center": v(-74, -4) * mm, "radius": 1.75 * mm});
            skCircle(sketch, "E11.0.29.17", {"center": v(-74, 2) * mm, "radius": 1.75 * mm});
            skCircle(sketch, "E11.0.29.18", {"center": v(-74, 8) * mm, "radius": 1.75 * mm});
            skCircle(sketch, "E11.0.29.19", {"center": v(-74, 14) * mm, "radius": 1.75 * mm});
            skCircle(sketch, "E11.0.29.20", {"center": v(-74, 20) * mm, "radius": 1.75 * mm});
            skCircle(sketch, "E11.0.29.21", {"center": v(-74, 26) * mm, "radius": 1.75 * mm});
            skCircle(sketch, "E11.0.29.22", {"center": v(-74, 32) * mm, "radius": 1.75 * mm});
            skCircle(sketch, "E11.0.29.23", {"center": v(-74, 38) * mm, "radius": 1.75 * mm});
            skCircle(sketch, "E11.0.29.24", {"center": v(-74, 44) * mm, "radius": 1.75 * mm});
            skCircle(sketch, "E11.0.29.25", {"center": v(-74, 50) * mm, "radius": 1.75 * mm});
            skCircle(sketch, "E11.0.29.26", {"center": v(-74, 56) * mm, "radius": 1.75 * mm});
            skCircle(sketch, "E11.0.29.27", {"center": v(-74, 62) * mm, "radius": 1.75 * mm});
            skCircle(sketch, "E11.0.29.28", {"center": v(-74, 68) * mm, "radius": 1.75 * mm});
            skCircle(sketch, "E11.0.29.29", {"center": v(-74, 74) * mm, "radius": 1.75 * mm});
            skCircle(sketch, "E12.0.30.0", {"center": v(-80, -100) * mm, "radius": 1.75 * mm});
            skCircle(sketch, "E12.0.30.1", {"center": v(-80, -94) * mm, "radius": 1.75 * mm});
            skCircle(sketch, "E12.0.30.2", {"center": v(-80, -88) * mm, "radius": 1.75 * mm});
            skCircle(sketch, "E12.0.30.3", {"center": v(-80, -82) * mm, "radius": 1.75 * mm});
            skCircle(sketch, "E12.0.30.4", {"center": v(-80, -76) * mm, "radius": 1.75 * mm});
            skCircle(sketch, "E12.0.30.5", {"center": v(-80, -70) * mm, "radius": 1.75 * mm});
            skCircle(sketch, "E12.0.30.6", {"center": v(-80, -64) * mm, "radius": 1.75 * mm});
            skCircle(sketch, "E12.0.30.7", {"center": v(-80, -58) * mm, "radius": 1.75 * mm});
            skCircle(sketch, "E12.0.30.8", {"center": v(-80, -52) * mm, "radius": 1.75 * mm});
            skCircle(sketch, "E12.0.30.9", {"center": v(-80, -46) * mm, "radius": 1.75 * mm});
            skCircle(sketch, "E12.0.30.10", {"center": v(-80, -40) * mm, "radius": 1.75 * mm});
            skCircle(sketch, "E12.0.30.11", {"center": v(-80, -34) * mm, "radius": 1.75 * mm});
            skCircle(sketch, "E12.0.30.12", {"center": v(-80, -28) * mm, "radius": 1.75 * mm});
            skCircle(sketch, "E12.0.30.13", {"center": v(-80, -22) * mm, "radius": 1.75 * mm});
            skCircle(sketch, "E12.0.30.14", {"center": v(-80, -16) * mm, "radius": 1.75 * mm});
            skCircle(sketch, "E12.0.30.15", {"center": v(-80, -10) * mm, "radius": 1.75 * mm});
            skCircle(sketch, "E12.0.30.16", {"center": v(-80, -4) * mm, "radius": 1.75 * mm});
            skCircle(sketch, "E12.0.30.17", {"center": v(-80, 2) * mm, "radius": 1.75 * mm});
            skCircle(sketch, "E12.0.30.18", {"center": v(-80, 8) * mm, "radius": 1.75 * mm});
            skCircle(sketch, "E12.0.30.19", {"center": v(-80, 14) * mm, "radius": 1.75 * mm});
            skCircle(sketch, "E12.0.30.20", {"center": v(-80, 20) * mm, "radius": 1.75 * mm});
            skCircle(sketch, "E12.0.30.21", {"center": v(-80, 26) * mm, "radius": 1.75 * mm});
            skCircle(sketch, "E12.0.30.22", {"center": v(-80, 32) * mm, "radius": 1.75 * mm});
            skCircle(sketch, "E12.0.30.23", {"center": v(-80, 38) * mm, "radius": 1.75 * mm});
            skCircle(sketch, "E12.0.30.24", {"center": v(-80, 44) * mm, "radius": 1.75 * mm});
            skCircle(sketch, "E12.0.30.25", {"center": v(-80, 50) * mm, "radius": 1.75 * mm});
            skCircle(sketch, "E12.0.30.26", {"center": v(-80, 56) * mm, "radius": 1.75 * mm});
            skCircle(sketch, "E12.0.30.27", {"center": v(-80, 62) * mm, "radius": 1.75 * mm});
            skCircle(sketch, "E12.0.30.28", {"center": v(-80, 68) * mm, "radius": 1.75 * mm});
            skCircle(sketch, "E12.0.30.29", {"center": v(-80, 74) * mm, "radius": 1.75 * mm});
            skCircle(sketch, "E12.0.31.0", {"center": v(-86, -100) * mm, "radius": 1.75 * mm});
            skCircle(sketch, "E12.0.31.1", {"center": v(-86, -94) * mm, "radius": 1.75 * mm});
            skCircle(sketch, "E12.0.31.2", {"center": v(-86, -88) * mm, "radius": 1.75 * mm});
            skCircle(sketch, "E12.0.31.3", {"center": v(-86, -82) * mm, "radius": 1.75 * mm});
            skCircle(sketch, "E12.0.31.4", {"center": v(-86, -76) * mm, "radius": 1.75 * mm});
            skCircle(sketch, "E12.0.31.5", {"center": v(-86, -70) * mm, "radius": 1.75 * mm});
            skCircle(sketch, "E12.0.31.6", {"center": v(-86, -64) * mm, "radius": 1.75 * mm});
            skCircle(sketch, "E12.0.31.7", {"center": v(-86, -58) * mm, "radius": 1.75 * mm});
            skCircle(sketch, "E12.0.31.8", {"center": v(-86, -52) * mm, "radius": 1.75 * mm});
            skCircle(sketch, "E12.0.31.9", {"center": v(-86, -46) * mm, "radius": 1.75 * mm});
            skCircle(sketch, "E12.0.31.10", {"center": v(-86, -40) * mm, "radius": 1.75 * mm});
            skCircle(sketch, "E12.0.31.11", {"center": v(-86, -34) * mm, "radius": 1.75 * mm});
            skCircle(sketch, "E12.0.31.12", {"center": v(-86, -28) * mm, "radius": 1.75 * mm});
            skCircle(sketch, "E12.0.31.13", {"center": v(-86, -22) * mm, "radius": 1.75 * mm});
            skCircle(sketch, "E12.0.31.14", {"center": v(-86, -16) * mm, "radius": 1.75 * mm});
            skCircle(sketch, "E12.0.31.15", {"center": v(-86, -10) * mm, "radius": 1.75 * mm});
            skCircle(sketch, "E12.0.31.16", {"center": v(-86, -4) * mm, "radius": 1.75 * mm});
            skCircle(sketch, "E12.0.31.17", {"center": v(-86, 2) * mm, "radius": 1.75 * mm});
            skCircle(sketch, "E12.0.31.18", {"center": v(-86, 8) * mm, "radius": 1.75 * mm});
            skCircle(sketch, "E12.0.31.19", {"center": v(-86, 14) * mm, "radius": 1.75 * mm});
            skCircle(sketch, "E12.0.31.20", {"center": v(-86, 20) * mm, "radius": 1.75 * mm});
            skCircle(sketch, "E12.0.31.21", {"center": v(-86, 26) * mm, "radius": 1.75 * mm});
            skCircle(sketch, "E12.0.31.22", {"center": v(-86, 32) * mm, "radius": 1.75 * mm});
            skCircle(sketch, "E12.0.31.23", {"center": v(-86, 38) * mm, "radius": 1.75 * mm});
            skCircle(sketch, "E12.0.31.24", {"center": v(-86, 44) * mm, "radius": 1.75 * mm});
            skCircle(sketch, "E12.0.31.25", {"center": v(-86, 50) * mm, "radius": 1.75 * mm});
            skCircle(sketch, "E12.0.31.26", {"center": v(-86, 56) * mm, "radius": 1.75 * mm});
            skCircle(sketch, "E12.0.31.27", {"center": v(-86, 62) * mm, "radius": 1.75 * mm});
            skCircle(sketch, "E12.0.31.28", {"center": v(-86, 68) * mm, "radius": 1.75 * mm});
            skCircle(sketch, "E12.0.31.29", {"center": v(-86, 74) * mm, "radius": 1.75 * mm});
            skCircle(sketch, "E12.0.32.0", {"center": v(-92, -100) * mm, "radius": 1.75 * mm});
            skCircle(sketch, "E12.0.32.1", {"center": v(-92, -94) * mm, "radius": 1.75 * mm});
            skCircle(sketch, "E12.0.32.2", {"center": v(-92, -88) * mm, "radius": 1.75 * mm});
            skCircle(sketch, "E12.0.32.3", {"center": v(-92, -82) * mm, "radius": 1.75 * mm});
            skCircle(sketch, "E12.0.32.4", {"center": v(-92, -76) * mm, "radius": 1.75 * mm});
            skCircle(sketch, "E12.0.32.5", {"center": v(-92, -70) * mm, "radius": 1.75 * mm});
            skCircle(sketch, "E12.0.32.6", {"center": v(-92, -64) * mm, "radius": 1.75 * mm});
            skCircle(sketch, "E12.0.32.7", {"center": v(-92, -58) * mm, "radius": 1.75 * mm});
            skCircle(sketch, "E12.0.32.8", {"center": v(-92, -52) * mm, "radius": 1.75 * mm});
            skCircle(sketch, "E12.0.32.9", {"center": v(-92, -46) * mm, "radius": 1.75 * mm});
            skCircle(sketch, "E12.0.32.10", {"center": v(-92, -40) * mm, "radius": 1.75 * mm});
            skCircle(sketch, "E12.0.32.11", {"center": v(-92, -34) * mm, "radius": 1.75 * mm});
            skCircle(sketch, "E12.0.32.12", {"center": v(-92, -28) * mm, "radius": 1.75 * mm});
            skCircle(sketch, "E12.0.32.13", {"center": v(-92, -22) * mm, "radius": 1.75 * mm});
            skCircle(sketch, "E12.0.32.14", {"center": v(-92, -16) * mm, "radius": 1.75 * mm});
            skCircle(sketch, "E12.0.32.15", {"center": v(-92, -10) * mm, "radius": 1.75 * mm});
            skCircle(sketch, "E12.0.32.16", {"center": v(-92, -4) * mm, "radius": 1.75 * mm});
            skCircle(sketch, "E12.0.32.17", {"center": v(-92, 2) * mm, "radius": 1.75 * mm});
            skCircle(sketch, "E12.0.32.18", {"center": v(-92, 8) * mm, "radius": 1.75 * mm});
            skCircle(sketch, "E12.0.32.19", {"center": v(-92, 14) * mm, "radius": 1.75 * mm});
            skCircle(sketch, "E12.0.32.20", {"center": v(-92, 20) * mm, "radius": 1.75 * mm});
            skCircle(sketch, "E12.0.32.21", {"center": v(-92, 26) * mm, "radius": 1.75 * mm});
            skCircle(sketch, "E12.0.32.22", {"center": v(-92, 32) * mm, "radius": 1.75 * mm});
            skCircle(sketch, "E12.0.32.23", {"center": v(-92, 38) * mm, "radius": 1.75 * mm});
            skCircle(sketch, "E12.0.32.24", {"center": v(-92, 44) * mm, "radius": 1.75 * mm});
            skCircle(sketch, "E12.0.32.25", {"center": v(-92, 50) * mm, "radius": 1.75 * mm});
            skCircle(sketch, "E12.0.32.26", {"center": v(-92, 56) * mm, "radius": 1.75 * mm});
            skCircle(sketch, "E12.0.32.27", {"center": v(-92, 62) * mm, "radius": 1.75 * mm});
            skCircle(sketch, "E12.0.32.28", {"center": v(-92, 68) * mm, "radius": 1.75 * mm});
            skCircle(sketch, "E12.0.32.29", {"center": v(-92, 74) * mm, "radius": 1.75 * mm});
            skCircle(sketch, "E12.0.33.0", {"center": v(-98, -100) * mm, "radius": 1.75 * mm});
            skCircle(sketch, "E12.0.33.1", {"center": v(-98, -94) * mm, "radius": 1.75 * mm});
            skCircle(sketch, "E12.0.33.2", {"center": v(-98, -88) * mm, "radius": 1.75 * mm});
            skCircle(sketch, "E12.0.33.3", {"center": v(-98, -82) * mm, "radius": 1.75 * mm});
            skCircle(sketch, "E12.0.33.4", {"center": v(-98, -76) * mm, "radius": 1.75 * mm});
            skCircle(sketch, "E12.0.33.5", {"center": v(-98, -70) * mm, "radius": 1.75 * mm});
            skCircle(sketch, "E12.0.33.6", {"center": v(-98, -64) * mm, "radius": 1.75 * mm});
            skCircle(sketch, "E12.0.33.7", {"center": v(-98, -58) * mm, "radius": 1.75 * mm});
            skCircle(sketch, "E12.0.33.8", {"center": v(-98, -52) * mm, "radius": 1.75 * mm});
            skCircle(sketch, "E12.0.33.9", {"center": v(-98, -46) * mm, "radius": 1.75 * mm});
            skCircle(sketch, "E12.0.33.10", {"center": v(-98, -40) * mm, "radius": 1.75 * mm});
            skCircle(sketch, "E12.0.33.11", {"center": v(-98, -34) * mm, "radius": 1.75 * mm});
            skCircle(sketch, "E12.0.33.12", {"center": v(-98, -28) * mm, "radius": 1.75 * mm});
            skCircle(sketch, "E12.0.33.13", {"center": v(-98, -22) * mm, "radius": 1.75 * mm});
            skCircle(sketch, "E12.0.33.14", {"center": v(-98, -16) * mm, "radius": 1.75 * mm});
            skCircle(sketch, "E12.0.33.15", {"center": v(-98, -10) * mm, "radius": 1.75 * mm});
            skCircle(sketch, "E12.0.33.16", {"center": v(-98, -4) * mm, "radius": 1.75 * mm});
            skCircle(sketch, "E12.0.33.17", {"center": v(-98, 2) * mm, "radius": 1.75 * mm});
            skCircle(sketch, "E12.0.33.18", {"center": v(-98, 8) * mm, "radius": 1.75 * mm});
            skCircle(sketch, "E12.0.33.19", {"center": v(-98, 14) * mm, "radius": 1.75 * mm});
            skCircle(sketch, "E12.0.33.20", {"center": v(-98, 20) * mm, "radius": 1.75 * mm});
            skCircle(sketch, "E12.0.33.21", {"center": v(-98, 26) * mm, "radius": 1.75 * mm});
            skCircle(sketch, "E12.0.33.22", {"center": v(-98, 32) * mm, "radius": 1.75 * mm});
            skCircle(sketch, "E12.0.33.23", {"center": v(-98, 38) * mm, "radius": 1.75 * mm});
            skCircle(sketch, "E12.0.33.24", {"center": v(-98, 44) * mm, "radius": 1.75 * mm});
            skCircle(sketch, "E12.0.33.25", {"center": v(-98, 50) * mm, "radius": 1.75 * mm});
            skCircle(sketch, "E12.0.33.26", {"center": v(-98, 56) * mm, "radius": 1.75 * mm});
            skCircle(sketch, "E12.0.33.27", {"center": v(-98, 62) * mm, "radius": 1.75 * mm});
            skCircle(sketch, "E12.0.33.28", {"center": v(-98, 68) * mm, "radius": 1.75 * mm});
            skCircle(sketch, "E12.0.33.29", {"center": v(-98, 74) * mm, "radius": 1.75 * mm});
            skCircle(sketch, "E13.0.0.30", {"center": v(100, 80) * mm, "radius": 1.75 * mm});
            skCircle(sketch, "E13.0.0.31", {"center": v(100, 86) * mm, "radius": 1.75 * mm});
            skCircle(sketch, "E13.0.0.32", {"center": v(100, 92) * mm, "radius": 1.75 * mm});
            skCircle(sketch, "E13.0.0.33", {"center": v(100, 98) * mm, "radius": 1.75 * mm});
            skCircle(sketch, "E13.0.1.30", {"center": v(94, 80) * mm, "radius": 1.75 * mm});
            skCircle(sketch, "E13.0.1.31", {"center": v(94, 86) * mm, "radius": 1.75 * mm});
            skCircle(sketch, "E13.0.1.32", {"center": v(94, 92) * mm, "radius": 1.75 * mm});
            skCircle(sketch, "E13.0.1.33", {"center": v(94, 98) * mm, "radius": 1.75 * mm});
            skCircle(sketch, "E13.0.2.30", {"center": v(88, 80) * mm, "radius": 1.75 * mm});
            skCircle(sketch, "E13.0.2.31", {"center": v(88, 86) * mm, "radius": 1.75 * mm});
            skCircle(sketch, "E13.0.2.32", {"center": v(88, 92) * mm, "radius": 1.75 * mm});
            skCircle(sketch, "E13.0.2.33", {"center": v(88, 98) * mm, "radius": 1.75 * mm});
            skCircle(sketch, "E13.0.3.30", {"center": v(82, 80) * mm, "radius": 1.75 * mm});
            skCircle(sketch, "E13.0.3.31", {"center": v(82, 86) * mm, "radius": 1.75 * mm});
            skCircle(sketch, "E13.0.3.32", {"center": v(82, 92) * mm, "radius": 1.75 * mm});
            skCircle(sketch, "E13.0.3.33", {"center": v(82, 98) * mm, "radius": 1.75 * mm});
            skCircle(sketch, "E13.0.4.30", {"center": v(76, 80) * mm, "radius": 1.75 * mm});
            skCircle(sketch, "E13.0.4.31", {"center": v(76, 86) * mm, "radius": 1.75 * mm});
            skCircle(sketch, "E13.0.4.32", {"center": v(76, 92) * mm, "radius": 1.75 * mm});
            skCircle(sketch, "E13.0.4.33", {"center": v(76, 98) * mm, "radius": 1.75 * mm});
            skCircle(sketch, "E13.0.5.30", {"center": v(70, 80) * mm, "radius": 1.75 * mm});
            skCircle(sketch, "E13.0.5.31", {"center": v(70, 86) * mm, "radius": 1.75 * mm});
            skCircle(sketch, "E13.0.5.32", {"center": v(70, 92) * mm, "radius": 1.75 * mm});
            skCircle(sketch, "E13.0.5.33", {"center": v(70, 98) * mm, "radius": 1.75 * mm});
            skCircle(sketch, "E13.0.6.30", {"center": v(64, 80) * mm, "radius": 1.75 * mm});
            skCircle(sketch, "E13.0.6.31", {"center": v(64, 86) * mm, "radius": 1.75 * mm});
            skCircle(sketch, "E13.0.6.32", {"center": v(64, 92) * mm, "radius": 1.75 * mm});
            skCircle(sketch, "E13.0.6.33", {"center": v(64, 98) * mm, "radius": 1.75 * mm});
            skCircle(sketch, "E13.0.7.30", {"center": v(58, 80) * mm, "radius": 1.75 * mm});
            skCircle(sketch, "E13.0.7.31", {"center": v(58, 86) * mm, "radius": 1.75 * mm});
            skCircle(sketch, "E13.0.7.32", {"center": v(58, 92) * mm, "radius": 1.75 * mm});
            skCircle(sketch, "E13.0.7.33", {"center": v(58, 98) * mm, "radius": 1.75 * mm});
            skCircle(sketch, "E13.0.8.30", {"center": v(52, 80) * mm, "radius": 1.75 * mm});
            skCircle(sketch, "E13.0.8.31", {"center": v(52, 86) * mm, "radius": 1.75 * mm});
            skCircle(sketch, "E13.0.8.32", {"center": v(52, 92) * mm, "radius": 1.75 * mm});
            skCircle(sketch, "E13.0.8.33", {"center": v(52, 98) * mm, "radius": 1.75 * mm});
            skCircle(sketch, "E13.0.9.30", {"center": v(46, 80) * mm, "radius": 1.75 * mm});
            skCircle(sketch, "E13.0.9.31", {"center": v(46, 86) * mm, "radius": 1.75 * mm});
            skCircle(sketch, "E13.0.9.32", {"center": v(46, 92) * mm, "radius": 1.75 * mm});
            skCircle(sketch, "E13.0.9.33", {"center": v(46, 98) * mm, "radius": 1.75 * mm});
            skCircle(sketch, "E13.0.10.30", {"center": v(40, 80) * mm, "radius": 1.75 * mm});
            skCircle(sketch, "E13.0.10.31", {"center": v(40, 86) * mm, "radius": 1.75 * mm});
            skCircle(sketch, "E13.0.10.32", {"center": v(40, 92) * mm, "radius": 1.75 * mm});
            skCircle(sketch, "E13.0.10.33", {"center": v(40, 98) * mm, "radius": 1.75 * mm});
            skCircle(sketch, "E13.0.11.30", {"center": v(34, 80) * mm, "radius": 1.75 * mm});
            skCircle(sketch, "E13.0.11.31", {"center": v(34, 86) * mm, "radius": 1.75 * mm});
            skCircle(sketch, "E13.0.11.32", {"center": v(34, 92) * mm, "radius": 1.75 * mm});
            skCircle(sketch, "E13.0.11.33", {"center": v(34, 98) * mm, "radius": 1.75 * mm});
            skCircle(sketch, "E13.0.12.30", {"center": v(28, 80) * mm, "radius": 1.75 * mm});
            skCircle(sketch, "E13.0.12.31", {"center": v(28, 86) * mm, "radius": 1.75 * mm});
            skCircle(sketch, "E13.0.12.32", {"center": v(28, 92) * mm, "radius": 1.75 * mm});
            skCircle(sketch, "E13.0.12.33", {"center": v(28, 98) * mm, "radius": 1.75 * mm});
            skCircle(sketch, "E13.0.13.30", {"center": v(22, 80) * mm, "radius": 1.75 * mm});
            skCircle(sketch, "E13.0.13.31", {"center": v(22, 86) * mm, "radius": 1.75 * mm});
            skCircle(sketch, "E13.0.13.32", {"center": v(22, 92) * mm, "radius": 1.75 * mm});
            skCircle(sketch, "E13.0.13.33", {"center": v(22, 98) * mm, "radius": 1.75 * mm});
            skCircle(sketch, "E13.0.14.30", {"center": v(16, 80) * mm, "radius": 1.75 * mm});
            skCircle(sketch, "E13.0.14.31", {"center": v(16, 86) * mm, "radius": 1.75 * mm});
            skCircle(sketch, "E13.0.14.32", {"center": v(16, 92) * mm, "radius": 1.75 * mm});
            skCircle(sketch, "E13.0.14.33", {"center": v(16, 98) * mm, "radius": 1.75 * mm});
            skCircle(sketch, "E13.0.15.30", {"center": v(10, 80) * mm, "radius": 1.75 * mm});
            skCircle(sketch, "E13.0.15.31", {"center": v(10, 86) * mm, "radius": 1.75 * mm});
            skCircle(sketch, "E13.0.15.32", {"center": v(10, 92) * mm, "radius": 1.75 * mm});
            skCircle(sketch, "E13.0.15.33", {"center": v(10, 98) * mm, "radius": 1.75 * mm});
            skCircle(sketch, "E13.0.16.30", {"center": v(4, 80) * mm, "radius": 1.75 * mm});
            skCircle(sketch, "E13.0.16.31", {"center": v(4, 86) * mm, "radius": 1.75 * mm});
            skCircle(sketch, "E13.0.16.32", {"center": v(4, 92) * mm, "radius": 1.75 * mm});
            skCircle(sketch, "E13.0.16.33", {"center": v(4, 98) * mm, "radius": 1.75 * mm});
            skCircle(sketch, "E13.0.17.30", {"center": v(-2, 80) * mm, "radius": 1.75 * mm});
            skCircle(sketch, "E13.0.17.31", {"center": v(-2, 86) * mm, "radius": 1.75 * mm});
            skCircle(sketch, "E13.0.17.32", {"center": v(-2, 92) * mm, "radius": 1.75 * mm});
            skCircle(sketch, "E13.0.17.33", {"center": v(-2, 98) * mm, "radius": 1.75 * mm});
            skCircle(sketch, "E13.0.18.30", {"center": v(-8, 80) * mm, "radius": 1.75 * mm});
            skCircle(sketch, "E13.0.18.31", {"center": v(-8, 86) * mm, "radius": 1.75 * mm});
            skCircle(sketch, "E13.0.18.32", {"center": v(-8, 92) * mm, "radius": 1.75 * mm});
            skCircle(sketch, "E13.0.18.33", {"center": v(-8, 98) * mm, "radius": 1.75 * mm});
            skCircle(sketch, "E13.0.19.30", {"center": v(-14, 80) * mm, "radius": 1.75 * mm});
            skCircle(sketch, "E13.0.19.31", {"center": v(-14, 86) * mm, "radius": 1.75 * mm});
            skCircle(sketch, "E13.0.19.32", {"center": v(-14, 92) * mm, "radius": 1.75 * mm});
            skCircle(sketch, "E13.0.19.33", {"center": v(-14, 98) * mm, "radius": 1.75 * mm});
            skCircle(sketch, "E13.0.20.30", {"center": v(-20, 80) * mm, "radius": 1.75 * mm});
            skCircle(sketch, "E13.0.20.31", {"center": v(-20, 86) * mm, "radius": 1.75 * mm});
            skCircle(sketch, "E13.0.20.32", {"center": v(-20, 92) * mm, "radius": 1.75 * mm});
            skCircle(sketch, "E13.0.20.33", {"center": v(-20, 98) * mm, "radius": 1.75 * mm});
            skCircle(sketch, "E13.0.21.30", {"center": v(-26, 80) * mm, "radius": 1.75 * mm});
            skCircle(sketch, "E13.0.21.31", {"center": v(-26, 86) * mm, "radius": 1.75 * mm});
            skCircle(sketch, "E13.0.21.32", {"center": v(-26, 92) * mm, "radius": 1.75 * mm});
            skCircle(sketch, "E13.0.21.33", {"center": v(-26, 98) * mm, "radius": 1.75 * mm});
            skCircle(sketch, "E13.0.22.30", {"center": v(-32, 80) * mm, "radius": 1.75 * mm});
            skCircle(sketch, "E13.0.22.31", {"center": v(-32, 86) * mm, "radius": 1.75 * mm});
            skCircle(sketch, "E13.0.22.32", {"center": v(-32, 92) * mm, "radius": 1.75 * mm});
            skCircle(sketch, "E13.0.22.33", {"center": v(-32, 98) * mm, "radius": 1.75 * mm});
            skCircle(sketch, "E13.0.23.30", {"center": v(-38, 80) * mm, "radius": 1.75 * mm});
            skCircle(sketch, "E13.0.23.31", {"center": v(-38, 86) * mm, "radius": 1.75 * mm});
            skCircle(sketch, "E13.0.23.32", {"center": v(-38, 92) * mm, "radius": 1.75 * mm});
            skCircle(sketch, "E13.0.23.33", {"center": v(-38, 98) * mm, "radius": 1.75 * mm});
            skCircle(sketch, "E13.0.24.30", {"center": v(-44, 80) * mm, "radius": 1.75 * mm});
            skCircle(sketch, "E13.0.24.31", {"center": v(-44, 86) * mm, "radius": 1.75 * mm});
            skCircle(sketch, "E13.0.24.32", {"center": v(-44, 92) * mm, "radius": 1.75 * mm});
            skCircle(sketch, "E13.0.24.33", {"center": v(-44, 98) * mm, "radius": 1.75 * mm});
            skCircle(sketch, "E13.0.25.30", {"center": v(-50, 80) * mm, "radius": 1.75 * mm});
            skCircle(sketch, "E13.0.25.31", {"center": v(-50, 86) * mm, "radius": 1.75 * mm});
            skCircle(sketch, "E13.0.25.32", {"center": v(-50, 92) * mm, "radius": 1.75 * mm});
            skCircle(sketch, "E13.0.25.33", {"center": v(-50, 98) * mm, "radius": 1.75 * mm});
            skCircle(sketch, "E13.0.26.30", {"center": v(-56, 80) * mm, "radius": 1.75 * mm});
            skCircle(sketch, "E13.0.26.31", {"center": v(-56, 86) * mm, "radius": 1.75 * mm});
            skCircle(sketch, "E13.0.26.32", {"center": v(-56, 92) * mm, "radius": 1.75 * mm});
            skCircle(sketch, "E13.0.26.33", {"center": v(-56, 98) * mm, "radius": 1.75 * mm});
            skCircle(sketch, "E13.0.27.30", {"center": v(-62, 80) * mm, "radius": 1.75 * mm});
            skCircle(sketch, "E13.0.27.31", {"center": v(-62, 86) * mm, "radius": 1.75 * mm});
            skCircle(sketch, "E13.0.27.32", {"center": v(-62, 92) * mm, "radius": 1.75 * mm});
            skCircle(sketch, "E13.0.27.33", {"center": v(-62, 98) * mm, "radius": 1.75 * mm});
            skCircle(sketch, "E13.0.28.30", {"center": v(-68, 80) * mm, "radius": 1.75 * mm});
            skCircle(sketch, "E13.0.28.31", {"center": v(-68, 86) * mm, "radius": 1.75 * mm});
            skCircle(sketch, "E13.0.28.32", {"center": v(-68, 92) * mm, "radius": 1.75 * mm});
            skCircle(sketch, "E13.0.28.33", {"center": v(-68, 98) * mm, "radius": 1.75 * mm});
            skCircle(sketch, "E13.0.29.30", {"center": v(-74, 80) * mm, "radius": 1.75 * mm});
            skCircle(sketch, "E13.0.29.31", {"center": v(-74, 86) * mm, "radius": 1.75 * mm});
            skCircle(sketch, "E13.0.29.32", {"center": v(-74, 92) * mm, "radius": 1.75 * mm});
            skCircle(sketch, "E13.0.29.33", {"center": v(-74, 98) * mm, "radius": 1.75 * mm});
            skCircle(sketch, "E13.0.30.30", {"center": v(-80, 80) * mm, "radius": 1.75 * mm});
            skCircle(sketch, "E13.0.30.31", {"center": v(-80, 86) * mm, "radius": 1.75 * mm});
            skCircle(sketch, "E13.0.30.32", {"center": v(-80, 92) * mm, "radius": 1.75 * mm});
            skCircle(sketch, "E13.0.30.33", {"center": v(-80, 98) * mm, "radius": 1.75 * mm});
            skCircle(sketch, "E13.0.31.30", {"center": v(-86, 80) * mm, "radius": 1.75 * mm});
            skCircle(sketch, "E13.0.31.31", {"center": v(-86, 86) * mm, "radius": 1.75 * mm});
            skCircle(sketch, "E13.0.31.32", {"center": v(-86, 92) * mm, "radius": 1.75 * mm});
            skCircle(sketch, "E13.0.31.33", {"center": v(-86, 98) * mm, "radius": 1.75 * mm});
            skCircle(sketch, "E13.0.32.30", {"center": v(-92, 80) * mm, "radius": 1.75 * mm});
            skCircle(sketch, "E13.0.32.31", {"center": v(-92, 86) * mm, "radius": 1.75 * mm});
            skCircle(sketch, "E13.0.32.32", {"center": v(-92, 92) * mm, "radius": 1.75 * mm});
            skCircle(sketch, "E13.0.32.33", {"center": v(-92, 98) * mm, "radius": 1.75 * mm});
            skCircle(sketch, "E13.0.33.30", {"center": v(-98, 80) * mm, "radius": 1.75 * mm});
            skCircle(sketch, "E13.0.33.31", {"center": v(-98, 86) * mm, "radius": 1.75 * mm});
            skCircle(sketch, "E13.0.33.32", {"center": v(-98, 92) * mm, "radius": 1.75 * mm});
            skCircle(sketch, "E13.0.33.33", {"center": v(-98, 98) * mm, "radius": 1.75 * mm});
            skSolve(sketch);
        }
        {
            var Q0;
            Q0 = qSketchRegion(id + "F8", true);
            var Q1;
            Q1 = qSketchRegion(id + "F8", true);
            extrude(context, id + "F9", {"entities" : qUnion([Q0, Q1]), "operationType" : NewBodyOperationType.REMOVE, "endBound" : BoundingType.THROUGH_ALL, "depth" : 25 * mm});
        }
        {
            var Q0;
            Q0=qCreatedBy(makeId("Top.planeOp"),FACE);
            var sketch = newSketch(context, id + "F10", { "sketchPlane" : qUnion([Q0])});
            skCircle(sketch, "E14", {"center": v(0, 0) * mm, "radius": 100 * mm});
            skCircle(sketch, "E15", {"center": v(0, 0) * mm, "radius": 97 * mm});
            skSolve(sketch);
        }
        {
            var Q0;
            Q0 = qSketchRegion(id + "F10", true);
            extrude(context, id + "F11", {"entities" : qUnion([Q0]), "operationType" : NewBodyOperationType.ADD, "oppositeDirection" : true, "depth" : 3 * mm});
        }
        {
            var Q0;
            Q0=qCreatedBy(id+"F3.planeOp",FACE);
            cPlane(context, id + "F12", {"entities" : qUnion([Q0]), "cplaneType" : CPlaneType.OFFSET, "offset" : 43 * mm, "oppositeDirection" : true, "width" : 150 * mm, "height" : 150 * mm});
        }
        {
            var Q0;
            Q0=qCreatedBy(id+"F12.planeOp",FACE);
            var sketch = newSketch(context, id + "F13", { "sketchPlane" : qUnion([Q0])});
            skLineSegment(sketch, "E16", {"start": v(0, 0) * mm, "end": v(0, 100) * mm, "construction": true});
            skLineSegment(sketch, "E17.bottom", {"start": v(0, 100) * mm, "end": v(-3, 100) * mm});
            skLineSegment(sketch, "E17.top", {"start": v(0, 97) * mm, "end": v(-3, 97) * mm});
            skLineSegment(sketch, "E17.left", {"start": v(0, 100) * mm, "end": v(0, 97) * mm});
            skLineSegment(sketch, "E17.right", {"start": v(-3, 100) * mm, "end": v(-3, 97) * mm});
            skLineSegment(sketch, "E18.1.0", {"start": v(-5.7, 99.84) * mm, "end": v(-5.54, 96.84) * mm});
            skLineSegment(sketch, "E18.1.1", {"start": v(-5.7, 99.84) * mm, "end": v(-8.7, 99.67) * mm});
            skLineSegment(sketch, "E18.1.2", {"start": v(-5.54, 96.84) * mm, "end": v(-8.53, 96.67) * mm});
            skLineSegment(sketch, "E18.1.3", {"start": v(-8.7, 99.67) * mm, "end": v(-8.53, 96.67) * mm});
            skLineSegment(sketch, "E18.2.0", {"start": v(-11.4, 99.35) * mm, "end": v(-11.06, 96.37) * mm});
            skLineSegment(sketch, "E18.2.1", {"start": v(-11.4, 99.35) * mm, "end": v(-14.38, 99) * mm});
            skLineSegment(sketch, "E18.2.2", {"start": v(-11.06, 96.37) * mm, "end": v(-14.04, 96.03) * mm});
            skLineSegment(sketch, "E18.2.3", {"start": v(-14.38, 99) * mm, "end": v(-14.04, 96.03) * mm});
            skLineSegment(sketch, "E18.3.0", {"start": v(-17.05, 98.54) * mm, "end": v(-16.54, 95.58) * mm});
            skLineSegment(sketch, "E18.3.1", {"start": v(-17.05, 98.54) * mm, "end": v(-20, 98.02) * mm});
            skLineSegment(sketch, "E18.3.2", {"start": v(-16.54, 95.58) * mm, "end": v(-19.5, 95.07) * mm});
            skLineSegment(sketch, "E18.3.3", {"start": v(-20, 98.02) * mm, "end": v(-19.5, 95.07) * mm});
            skLineSegment(sketch, "E18.4.0", {"start": v(-22.65, 97.4) * mm, "end": v(-21.97, 94.48) * mm});
            skLineSegment(sketch, "E18.4.1", {"start": v(-22.65, 97.4) * mm, "end": v(-25.57, 96.72) * mm});
            skLineSegment(sketch, "E18.4.2", {"start": v(-21.97, 94.48) * mm, "end": v(-24.9, 93.8) * mm});
            skLineSegment(sketch, "E18.4.3", {"start": v(-25.57, 96.72) * mm, "end": v(-24.9, 93.8) * mm});
            skLineSegment(sketch, "E18.5.0", {"start": v(-28.17, 95.95) * mm, "end": v(-27.33, 93.07) * mm});
            skLineSegment(sketch, "E18.5.1", {"start": v(-28.17, 95.95) * mm, "end": v(-31.05, 95.1) * mm});
            skLineSegment(sketch, "E18.5.2", {"start": v(-27.33, 93.07) * mm, "end": v(-30.2, 92.23) * mm});
            skLineSegment(sketch, "E18.5.3", {"start": v(-31.05, 95.1) * mm, "end": v(-30.2, 92.23) * mm});
            skLineSegment(sketch, "E18.6.0", {"start": v(-33.6, 94.18) * mm, "end": v(-32.6, 91.36) * mm});
            skLineSegment(sketch, "E18.6.1", {"start": v(-33.6, 94.18) * mm, "end": v(-36.43, 93.18) * mm});
            skLineSegment(sketch, "E18.6.2", {"start": v(-32.6, 91.36) * mm, "end": v(-35.42, 90.35) * mm});
            skLineSegment(sketch, "E18.6.3", {"start": v(-36.43, 93.18) * mm, "end": v(-35.42, 90.35) * mm});
            skLineSegment(sketch, "E18.7.0", {"start": v(-38.93, 92.11) * mm, "end": v(-37.76, 89.35) * mm});
            skLineSegment(sketch, "E18.7.1", {"start": v(-38.93, 92.11) * mm, "end": v(-41.7, 90.94) * mm});
            skLineSegment(sketch, "E18.7.2", {"start": v(-37.76, 89.35) * mm, "end": v(-40.52, 88.18) * mm});
            skLineSegment(sketch, "E18.7.3", {"start": v(-41.7, 90.94) * mm, "end": v(-40.52, 88.18) * mm});
            skLineSegment(sketch, "E18.8.0", {"start": v(-44.12, 89.74) * mm, "end": v(-42.8, 87.05) * mm});
            skLineSegment(sketch, "E18.8.1", {"start": v(-44.12, 89.74) * mm, "end": v(-46.81, 88.42) * mm});
            skLineSegment(sketch, "E18.8.2", {"start": v(-42.8, 87.05) * mm, "end": v(-45.5, 85.72) * mm});
            skLineSegment(sketch, "E18.8.3", {"start": v(-46.81, 88.42) * mm, "end": v(-45.5, 85.72) * mm});
            skLineSegment(sketch, "E18.9.0", {"start": v(-49.17, 87.07) * mm, "end": v(-47.7, 84.46) * mm});
            skLineSegment(sketch, "E18.9.1", {"start": v(-49.17, 87.07) * mm, "end": v(-51.79, 85.6) * mm});
            skLineSegment(sketch, "E18.9.2", {"start": v(-47.7, 84.46) * mm, "end": v(-50.31, 82.99) * mm});
            skLineSegment(sketch, "E18.9.3", {"start": v(-51.79, 85.6) * mm, "end": v(-50.31, 82.99) * mm});
            skLineSegment(sketch, "E18.10.0", {"start": v(-54.06, 84.13) * mm, "end": v(-52.44, 81.6) * mm});
            skLineSegment(sketch, "E18.10.1", {"start": v(-54.06, 84.13) * mm, "end": v(-56.59, 82.5) * mm});
            skLineSegment(sketch, "E18.10.2", {"start": v(-52.44, 81.6) * mm, "end": v(-54.97, 79.98) * mm});
            skLineSegment(sketch, "E18.10.3", {"start": v(-56.59, 82.5) * mm, "end": v(-54.97, 79.98) * mm});
            skLineSegment(sketch, "E18.11.0", {"start": v(-58.78, 80.9) * mm, "end": v(-57.02, 78.47) * mm});
            skLineSegment(sketch, "E18.11.1", {"start": v(-58.78, 80.9) * mm, "end": v(-61.2, 79.14) * mm});
            skLineSegment(sketch, "E18.11.2", {"start": v(-57.02, 78.47) * mm, "end": v(-59.44, 76.71) * mm});
            skLineSegment(sketch, "E18.11.3", {"start": v(-61.2, 79.14) * mm, "end": v(-59.44, 76.71) * mm});
            skLineSegment(sketch, "E18.12.0", {"start": v(-63.3, 77.41) * mm, "end": v(-61.4, 75.1) * mm});
            skLineSegment(sketch, "E18.12.1", {"start": v(-63.3, 77.41) * mm, "end": v(-65.62, 75.52) * mm});
            skLineSegment(sketch, "E18.12.2", {"start": v(-61.4, 75.1) * mm, "end": v(-63.72, 73.2) * mm});
            skLineSegment(sketch, "E18.12.3", {"start": v(-65.62, 75.52) * mm, "end": v(-63.72, 73.2) * mm});
            skLineSegment(sketch, "E18.13.0", {"start": v(-67.62, 73.67) * mm, "end": v(-65.59, 71.46) * mm});
            skLineSegment(sketch, "E18.13.1", {"start": v(-67.62, 73.67) * mm, "end": v(-69.83, 71.65) * mm});
            skLineSegment(sketch, "E18.13.2", {"start": v(-65.59, 71.46) * mm, "end": v(-67.8, 69.44) * mm});
            skLineSegment(sketch, "E18.13.3", {"start": v(-69.83, 71.65) * mm, "end": v(-67.8, 69.44) * mm});
            skLineSegment(sketch, "E18.14.0", {"start": v(-71.71, 69.7) * mm, "end": v(-69.56, 67.6) * mm});
            skLineSegment(sketch, "E18.14.1", {"start": v(-71.71, 69.7) * mm, "end": v(-73.8, 67.54) * mm});
            skLineSegment(sketch, "E18.14.2", {"start": v(-69.56, 67.6) * mm, "end": v(-71.65, 65.45) * mm});
            skLineSegment(sketch, "E18.14.3", {"start": v(-73.8, 67.54) * mm, "end": v(-71.65, 65.45) * mm});
            skLineSegment(sketch, "E18.15.0", {"start": v(-75.57, 65.49) * mm, "end": v(-73.3, 63.52) * mm});
            skLineSegment(sketch, "E18.15.1", {"start": v(-75.57, 65.49) * mm, "end": v(-77.54, 63.22) * mm});
            skLineSegment(sketch, "E18.15.2", {"start": v(-73.3, 63.52) * mm, "end": v(-75.27, 61.25) * mm});
            skLineSegment(sketch, "E18.15.3", {"start": v(-77.54, 63.22) * mm, "end": v(-75.27, 61.25) * mm});
            skLineSegment(sketch, "E18.16.0", {"start": v(-79.2, 61.06) * mm, "end": v(-76.81, 59.23) * mm});
            skLineSegment(sketch, "E18.16.1", {"start": v(-79.2, 61.06) * mm, "end": v(-81.02, 58.69) * mm});
            skLineSegment(sketch, "E18.16.2", {"start": v(-76.81, 59.23) * mm, "end": v(-78.65, 56.86) * mm});
            skLineSegment(sketch, "E18.16.3", {"start": v(-81.02, 58.69) * mm, "end": v(-78.65, 56.86) * mm});
            skLineSegment(sketch, "E18.17.0", {"start": v(-82.55, 56.44) * mm, "end": v(-80.07, 54.75) * mm});
            skLineSegment(sketch, "E18.17.1", {"start": v(-82.55, 56.44) * mm, "end": v(-84.24, 53.97) * mm});
            skLineSegment(sketch, "E18.17.2", {"start": v(-80.07, 54.75) * mm, "end": v(-81.76, 52.27) * mm});
            skLineSegment(sketch, "E18.17.3", {"start": v(-84.24, 53.97) * mm, "end": v(-81.76, 52.27) * mm});
            skLineSegment(sketch, "E18.18.0", {"start": v(-85.63, 51.64) * mm, "end": v(-83.07, 50.1) * mm});
            skLineSegment(sketch, "E18.18.1", {"start": v(-85.63, 51.64) * mm, "end": v(-87.18, 49.07) * mm});
            skLineSegment(sketch, "E18.18.2", {"start": v(-83.07, 50.1) * mm, "end": v(-84.62, 47.52) * mm});
            skLineSegment(sketch, "E18.18.3", {"start": v(-87.18, 49.07) * mm, "end": v(-84.62, 47.52) * mm});
            skLineSegment(sketch, "E18.19.0", {"start": v(-88.44, 46.67) * mm, "end": v(-85.79, 45.27) * mm});
            skLineSegment(sketch, "E18.19.1", {"start": v(-88.44, 46.67) * mm, "end": v(-89.84, 44.01) * mm});
            skLineSegment(sketch, "E18.19.2", {"start": v(-85.79, 45.27) * mm, "end": v(-87.19, 42.61) * mm});
            skLineSegment(sketch, "E18.19.3", {"start": v(-89.84, 44.01) * mm, "end": v(-87.19, 42.61) * mm});
            skLineSegment(sketch, "E18.20.0", {"start": v(-90.96, 41.54) * mm, "end": v(-88.23, 40.3) * mm});
            skLineSegment(sketch, "E18.20.1", {"start": v(-90.96, 41.54) * mm, "end": v(-92.2, 38.81) * mm});
            skLineSegment(sketch, "E18.20.2", {"start": v(-88.23, 40.3) * mm, "end": v(-89.48, 37.57) * mm});
            skLineSegment(sketch, "E18.20.3", {"start": v(-92.2, 38.81) * mm, "end": v(-89.48, 37.57) * mm});
            skLineSegment(sketch, "E18.21.0", {"start": v(-93.19, 36.28) * mm, "end": v(-90.4, 35.2) * mm});
            skLineSegment(sketch, "E18.21.1", {"start": v(-93.19, 36.28) * mm, "end": v(-94.27, 33.49) * mm});
            skLineSegment(sketch, "E18.21.2", {"start": v(-90.4, 35.2) * mm, "end": v(-91.48, 32.4) * mm});
            skLineSegment(sketch, "E18.21.3", {"start": v(-94.27, 33.49) * mm, "end": v(-91.48, 32.4) * mm});
            skLineSegment(sketch, "E18.22.0", {"start": v(-95.1, 30.9) * mm, "end": v(-92.25, 29.97) * mm});
            skLineSegment(sketch, "E18.22.1", {"start": v(-95.1, 30.9) * mm, "end": v(-96.03, 28.05) * mm});
            skLineSegment(sketch, "E18.22.2", {"start": v(-92.25, 29.97) * mm, "end": v(-93.18, 27.12) * mm});
            skLineSegment(sketch, "E18.22.3", {"start": v(-96.03, 28.05) * mm, "end": v(-93.18, 27.12) * mm});
            skLineSegment(sketch, "E18.23.0", {"start": v(-96.71, 25.42) * mm, "end": v(-93.81, 24.66) * mm});
            skLineSegment(sketch, "E18.23.1", {"start": v(-96.71, 25.42) * mm, "end": v(-97.48, 22.52) * mm});
            skLineSegment(sketch, "E18.23.2", {"start": v(-93.81, 24.66) * mm, "end": v(-94.58, 21.76) * mm});
            skLineSegment(sketch, "E18.23.3", {"start": v(-97.48, 22.52) * mm, "end": v(-94.58, 21.76) * mm});
            skLineSegment(sketch, "E18.24.0", {"start": v(-98, 19.86) * mm, "end": v(-95.07, 19.26) * mm});
            skLineSegment(sketch, "E18.24.1", {"start": v(-98, 19.86) * mm, "end": v(-98.6, 16.92) * mm});
            skLineSegment(sketch, "E18.24.2", {"start": v(-95.07, 19.26) * mm, "end": v(-95.66, 16.32) * mm});
            skLineSegment(sketch, "E18.24.3", {"start": v(-98.6, 16.92) * mm, "end": v(-95.66, 16.32) * mm});
            skLineSegment(sketch, "E18.25.0", {"start": v(-98.98, 14.23) * mm, "end": v(-96.01, 13.8) * mm});
            skLineSegment(sketch, "E18.25.1", {"start": v(-98.98, 14.23) * mm, "end": v(-99.4, 11.26) * mm});
            skLineSegment(sketch, "E18.25.2", {"start": v(-96.01, 13.8) * mm, "end": v(-96.44, 10.84) * mm});
            skLineSegment(sketch, "E18.25.3", {"start": v(-99.4, 11.26) * mm, "end": v(-96.44, 10.84) * mm});
            skLineSegment(sketch, "E18.26.0", {"start": v(-99.63, 8.56) * mm, "end": v(-96.64, 8.3) * mm});
            skLineSegment(sketch, "E18.26.1", {"start": v(-99.63, 8.56) * mm, "end": v(-99.89, 5.57) * mm});
            skLineSegment(sketch, "E18.26.2", {"start": v(-96.64, 8.3) * mm, "end": v(-96.9, 5.31) * mm});
            skLineSegment(sketch, "E18.26.3", {"start": v(-99.89, 5.57) * mm, "end": v(-96.9, 5.31) * mm});
            skLineSegment(sketch, "E18.27.0", {"start": v(-99.96, 2.86) * mm, "end": v(-96.96, 2.77) * mm});
            skLineSegment(sketch, "E18.27.1", {"start": v(-99.96, 2.86) * mm, "end": v(-100.04, -0.14) * mm});
            skLineSegment(sketch, "E18.27.2", {"start": v(-96.96, 2.77) * mm, "end": v(-97.05, -0.23) * mm});
            skLineSegment(sketch, "E18.27.3", {"start": v(-100.04, -0.14) * mm, "end": v(-97.05, -0.23) * mm});
            skLineSegment(sketch, "E18.28.0", {"start": v(-99.96, -2.86) * mm, "end": v(-96.96, -2.77) * mm});
            skLineSegment(sketch, "E18.28.1", {"start": v(-99.96, -2.86) * mm, "end": v(-99.87, -5.85) * mm});
            skLineSegment(sketch, "E18.28.2", {"start": v(-96.96, -2.77) * mm, "end": v(-96.87, -5.77) * mm});
            skLineSegment(sketch, "E18.28.3", {"start": v(-99.87, -5.85) * mm, "end": v(-96.87, -5.77) * mm});
            skLineSegment(sketch, "E18.29.0", {"start": v(-99.63, -8.56) * mm, "end": v(-96.64, -8.3) * mm});
            skLineSegment(sketch, "E18.29.1", {"start": v(-99.63, -8.56) * mm, "end": v(-99.38, -11.55) * mm});
            skLineSegment(sketch, "E18.29.2", {"start": v(-96.64, -8.3) * mm, "end": v(-96.39, -11.29) * mm});
            skLineSegment(sketch, "E18.29.3", {"start": v(-99.38, -11.55) * mm, "end": v(-96.39, -11.29) * mm});
            skLineSegment(sketch, "E18.30.0", {"start": v(-98.98, -14.23) * mm, "end": v(-96.01, -13.8) * mm});
            skLineSegment(sketch, "E18.30.1", {"start": v(-98.98, -14.23) * mm, "end": v(-98.56, -17.2) * mm});
            skLineSegment(sketch, "E18.30.2", {"start": v(-96.01, -13.8) * mm, "end": v(-95.59, -16.77) * mm});
            skLineSegment(sketch, "E18.30.3", {"start": v(-98.56, -17.2) * mm, "end": v(-95.59, -16.77) * mm});
            skLineSegment(sketch, "E18.31.0", {"start": v(-98, -19.86) * mm, "end": v(-95.07, -19.26) * mm});
            skLineSegment(sketch, "E18.31.1", {"start": v(-98, -19.86) * mm, "end": v(-97.41, -22.8) * mm});
            skLineSegment(sketch, "E18.31.2", {"start": v(-95.07, -19.26) * mm, "end": v(-94.47, -22.2) * mm});
            skLineSegment(sketch, "E18.31.3", {"start": v(-97.41, -22.8) * mm, "end": v(-94.47, -22.2) * mm});
            skLineSegment(sketch, "E18.32.0", {"start": v(-96.71, -25.42) * mm, "end": v(-93.81, -24.66) * mm});
            skLineSegment(sketch, "E18.32.1", {"start": v(-96.71, -25.42) * mm, "end": v(-95.95, -28.32) * mm});
            skLineSegment(sketch, "E18.32.2", {"start": v(-93.81, -24.66) * mm, "end": v(-93.05, -27.56) * mm});
            skLineSegment(sketch, "E18.32.3", {"start": v(-95.95, -28.32) * mm, "end": v(-93.05, -27.56) * mm});
            skLineSegment(sketch, "E18.33.0", {"start": v(-95.1, -30.9) * mm, "end": v(-92.25, -29.97) * mm});
            skLineSegment(sketch, "E18.33.1", {"start": v(-95.1, -30.9) * mm, "end": v(-94.18, -33.75) * mm});
            skLineSegment(sketch, "E18.33.2", {"start": v(-92.25, -29.97) * mm, "end": v(-91.33, -32.83) * mm});
            skLineSegment(sketch, "E18.33.3", {"start": v(-94.18, -33.75) * mm, "end": v(-91.33, -32.83) * mm});
            skLineSegment(sketch, "E18.34.0", {"start": v(-93.19, -36.28) * mm, "end": v(-90.4, -35.2) * mm});
            skLineSegment(sketch, "E18.34.1", {"start": v(-93.19, -36.28) * mm, "end": v(-92.1, -39.08) * mm});
            skLineSegment(sketch, "E18.34.2", {"start": v(-90.4, -35.2) * mm, "end": v(-89.3, -37.99) * mm});
            skLineSegment(sketch, "E18.34.3", {"start": v(-92.1, -39.08) * mm, "end": v(-89.3, -37.99) * mm});
            skLineSegment(sketch, "E18.35.0", {"start": v(-90.96, -41.54) * mm, "end": v(-88.23, -40.3) * mm});
            skLineSegment(sketch, "E18.35.1", {"start": v(-90.96, -41.54) * mm, "end": v(-89.72, -44.27) * mm});
            skLineSegment(sketch, "E18.35.2", {"start": v(-88.23, -40.3) * mm, "end": v(-86.99, -43.02) * mm});
            skLineSegment(sketch, "E18.35.3", {"start": v(-89.72, -44.27) * mm, "end": v(-86.99, -43.02) * mm});
            skLineSegment(sketch, "E18.36.0", {"start": v(-88.44, -46.67) * mm, "end": v(-85.79, -45.27) * mm});
            skLineSegment(sketch, "E18.36.1", {"start": v(-88.44, -46.67) * mm, "end": v(-87.04, -49.32) * mm});
            skLineSegment(sketch, "E18.36.2", {"start": v(-85.79, -45.27) * mm, "end": v(-84.39, -47.92) * mm});
            skLineSegment(sketch, "E18.36.3", {"start": v(-87.04, -49.32) * mm, "end": v(-84.39, -47.92) * mm});
            skLineSegment(sketch, "E18.37.0", {"start": v(-85.63, -51.64) * mm, "end": v(-83.07, -50.1) * mm});
            skLineSegment(sketch, "E18.37.1", {"start": v(-85.63, -51.64) * mm, "end": v(-84.09, -54.2) * mm});
            skLineSegment(sketch, "E18.37.2", {"start": v(-83.07, -50.1) * mm, "end": v(-81.52, -52.66) * mm});
            skLineSegment(sketch, "E18.37.3", {"start": v(-84.09, -54.2) * mm, "end": v(-81.52, -52.66) * mm});
            skLineSegment(sketch, "E18.38.0", {"start": v(-82.55, -56.44) * mm, "end": v(-80.07, -54.75) * mm});
            skLineSegment(sketch, "E18.38.1", {"start": v(-82.55, -56.44) * mm, "end": v(-80.85, -58.92) * mm});
            skLineSegment(sketch, "E18.38.2", {"start": v(-80.07, -54.75) * mm, "end": v(-78.38, -57.23) * mm});
            skLineSegment(sketch, "E18.38.3", {"start": v(-80.85, -58.92) * mm, "end": v(-78.38, -57.23) * mm});
            skLineSegment(sketch, "E18.39.0", {"start": v(-79.2, -61.06) * mm, "end": v(-76.81, -59.23) * mm});
            skLineSegment(sketch, "E18.39.1", {"start": v(-79.2, -61.06) * mm, "end": v(-77.36, -63.44) * mm});
            skLineSegment(sketch, "E18.39.2", {"start": v(-76.81, -59.23) * mm, "end": v(-74.98, -61.6) * mm});
            skLineSegment(sketch, "E18.39.3", {"start": v(-77.36, -63.44) * mm, "end": v(-74.98, -61.6) * mm});
            skLineSegment(sketch, "E18.40.0", {"start": v(-75.57, -65.49) * mm, "end": v(-73.3, -63.52) * mm});
            skLineSegment(sketch, "E18.40.1", {"start": v(-75.57, -65.49) * mm, "end": v(-73.61, -67.75) * mm});
            skLineSegment(sketch, "E18.40.2", {"start": v(-73.3, -63.52) * mm, "end": v(-71.34, -65.79) * mm});
            skLineSegment(sketch, "E18.40.3", {"start": v(-73.61, -67.75) * mm, "end": v(-71.34, -65.79) * mm});
            skLineSegment(sketch, "E18.41.0", {"start": v(-71.71, -69.7) * mm, "end": v(-69.56, -67.6) * mm});
            skLineSegment(sketch, "E18.41.1", {"start": v(-71.71, -69.7) * mm, "end": v(-69.62, -71.85) * mm});
            skLineSegment(sketch, "E18.41.2", {"start": v(-69.56, -67.6) * mm, "end": v(-67.47, -69.75) * mm});
            skLineSegment(sketch, "E18.41.3", {"start": v(-69.62, -71.85) * mm, "end": v(-67.47, -69.75) * mm});
            skLineSegment(sketch, "E18.42.0", {"start": v(-67.62, -73.67) * mm, "end": v(-65.59, -71.46) * mm});
            skLineSegment(sketch, "E18.42.1", {"start": v(-67.62, -73.67) * mm, "end": v(-65.4, -75.7) * mm});
            skLineSegment(sketch, "E18.42.2", {"start": v(-65.59, -71.46) * mm, "end": v(-63.38, -73.5) * mm});
            skLineSegment(sketch, "E18.42.3", {"start": v(-65.4, -75.7) * mm, "end": v(-63.38, -73.5) * mm});
            skLineSegment(sketch, "E18.43.0", {"start": v(-63.3, -77.41) * mm, "end": v(-61.4, -75.1) * mm});
            skLineSegment(sketch, "E18.43.1", {"start": v(-63.3, -77.41) * mm, "end": v(-60.98, -79.31) * mm});
            skLineSegment(sketch, "E18.43.2", {"start": v(-61.4, -75.1) * mm, "end": v(-59.08, -77) * mm});
            skLineSegment(sketch, "E18.43.3", {"start": v(-60.98, -79.31) * mm, "end": v(-59.08, -77) * mm});
            skLineSegment(sketch, "E18.44.0", {"start": v(-58.78, -80.9) * mm, "end": v(-57.02, -78.47) * mm});
            skLineSegment(sketch, "E18.44.1", {"start": v(-58.78, -80.9) * mm, "end": v(-56.35, -82.67) * mm});
            skLineSegment(sketch, "E18.44.2", {"start": v(-57.02, -78.47) * mm, "end": v(-54.59, -80.24) * mm});
            skLineSegment(sketch, "E18.44.3", {"start": v(-56.35, -82.67) * mm, "end": v(-54.59, -80.24) * mm});
            skLineSegment(sketch, "E18.45.0", {"start": v(-54.06, -84.13) * mm, "end": v(-52.44, -81.6) * mm});
            skLineSegment(sketch, "E18.45.1", {"start": v(-54.06, -84.13) * mm, "end": v(-51.54, -85.75) * mm});
            skLineSegment(sketch, "E18.45.2", {"start": v(-52.44, -81.6) * mm, "end": v(-49.92, -83.22) * mm});
            skLineSegment(sketch, "E18.45.3", {"start": v(-51.54, -85.75) * mm, "end": v(-49.92, -83.22) * mm});
            skLineSegment(sketch, "E18.46.0", {"start": v(-49.17, -87.07) * mm, "end": v(-47.7, -84.46) * mm});
            skLineSegment(sketch, "E18.46.1", {"start": v(-49.17, -87.07) * mm, "end": v(-46.56, -88.55) * mm});
            skLineSegment(sketch, "E18.46.2", {"start": v(-47.7, -84.46) * mm, "end": v(-45.09, -85.94) * mm});
            skLineSegment(sketch, "E18.46.3", {"start": v(-46.56, -88.55) * mm, "end": v(-45.09, -85.94) * mm});
            skLineSegment(sketch, "E18.47.0", {"start": v(-44.12, -89.74) * mm, "end": v(-42.8, -87.05) * mm});
            skLineSegment(sketch, "E18.47.1", {"start": v(-44.12, -89.74) * mm, "end": v(-41.43, -91.06) * mm});
            skLineSegment(sketch, "E18.47.2", {"start": v(-42.8, -87.05) * mm, "end": v(-40.1, -88.37) * mm});
            skLineSegment(sketch, "E18.47.3", {"start": v(-41.43, -91.06) * mm, "end": v(-40.1, -88.37) * mm});
            skLineSegment(sketch, "E18.48.0", {"start": v(-38.93, -92.11) * mm, "end": v(-37.76, -89.35) * mm});
            skLineSegment(sketch, "E18.48.1", {"start": v(-38.93, -92.11) * mm, "end": v(-36.16, -93.28) * mm});
            skLineSegment(sketch, "E18.48.2", {"start": v(-37.76, -89.35) * mm, "end": v(-35, -90.52) * mm});
            skLineSegment(sketch, "E18.48.3", {"start": v(-36.16, -93.28) * mm, "end": v(-35, -90.52) * mm});
            skLineSegment(sketch, "E18.49.0", {"start": v(-33.6, -94.18) * mm, "end": v(-32.6, -91.36) * mm});
            skLineSegment(sketch, "E18.49.1", {"start": v(-33.6, -94.18) * mm, "end": v(-30.78, -95.2) * mm});
            skLineSegment(sketch, "E18.49.2", {"start": v(-32.6, -91.36) * mm, "end": v(-29.77, -92.37) * mm});
            skLineSegment(sketch, "E18.49.3", {"start": v(-30.78, -95.2) * mm, "end": v(-29.77, -92.37) * mm});
            skLineSegment(sketch, "E18.50.0", {"start": v(-28.17, -95.95) * mm, "end": v(-27.33, -93.07) * mm});
            skLineSegment(sketch, "E18.50.1", {"start": v(-28.17, -95.95) * mm, "end": v(-25.3, -96.8) * mm});
            skLineSegment(sketch, "E18.50.2", {"start": v(-27.33, -93.07) * mm, "end": v(-24.45, -93.92) * mm});
            skLineSegment(sketch, "E18.50.3", {"start": v(-25.3, -96.8) * mm, "end": v(-24.45, -93.92) * mm});
            skLineSegment(sketch, "E18.51.0", {"start": v(-22.65, -97.4) * mm, "end": v(-21.97, -94.48) * mm});
            skLineSegment(sketch, "E18.51.1", {"start": v(-22.65, -97.4) * mm, "end": v(-19.73, -98.08) * mm});
            skLineSegment(sketch, "E18.51.2", {"start": v(-21.97, -94.48) * mm, "end": v(-19.05, -95.16) * mm});
            skLineSegment(sketch, "E18.51.3", {"start": v(-19.73, -98.08) * mm, "end": v(-19.05, -95.16) * mm});
            skLineSegment(sketch, "E18.52.0", {"start": v(-17.05, -98.54) * mm, "end": v(-16.54, -95.58) * mm});
            skLineSegment(sketch, "E18.52.1", {"start": v(-17.05, -98.54) * mm, "end": v(-14.1, -99.05) * mm});
            skLineSegment(sketch, "E18.52.2", {"start": v(-16.54, -95.58) * mm, "end": v(-13.58, -96.1) * mm});
            skLineSegment(sketch, "E18.52.3", {"start": v(-14.1, -99.05) * mm, "end": v(-13.58, -96.1) * mm});
            skLineSegment(sketch, "E18.53.0", {"start": v(-11.4, -99.35) * mm, "end": v(-11.06, -96.37) * mm});
            skLineSegment(sketch, "E18.53.1", {"start": v(-11.4, -99.35) * mm, "end": v(-8.42, -99.7) * mm});
            skLineSegment(sketch, "E18.53.2", {"start": v(-11.06, -96.37) * mm, "end": v(-8.08, -96.7) * mm});
            skLineSegment(sketch, "E18.53.3", {"start": v(-8.42, -99.7) * mm, "end": v(-8.08, -96.7) * mm});
            skLineSegment(sketch, "E18.54.0", {"start": v(-5.7, -99.84) * mm, "end": v(-5.54, -96.84) * mm});
            skLineSegment(sketch, "E18.54.1", {"start": v(-5.7, -99.84) * mm, "end": v(-2.71, -100) * mm});
            skLineSegment(sketch, "E18.54.2", {"start": v(-5.54, -96.84) * mm, "end": v(-2.54, -97.01) * mm});
            skLineSegment(sketch, "E18.54.3", {"start": v(-2.71, -100) * mm, "end": v(-2.54, -97.01) * mm});
            skLineSegment(sketch, "E18.55.0", {"start": v(0, -100) * mm, "end": v(0, -97) * mm});
            skLineSegment(sketch, "E18.55.1", {"start": v(0, -100) * mm, "end": v(3, -100) * mm});
            skLineSegment(sketch, "E18.55.2", {"start": v(0, -97) * mm, "end": v(3, -97) * mm});
            skLineSegment(sketch, "E18.55.3", {"start": v(3, -100) * mm, "end": v(3, -97) * mm});
            skLineSegment(sketch, "E18.56.0", {"start": v(5.7, -99.84) * mm, "end": v(5.54, -96.84) * mm});
            skLineSegment(sketch, "E18.56.1", {"start": v(5.7, -99.84) * mm, "end": v(8.7, -99.67) * mm});
            skLineSegment(sketch, "E18.56.2", {"start": v(5.54, -96.84) * mm, "end": v(8.53, -96.67) * mm});
            skLineSegment(sketch, "E18.56.3", {"start": v(8.7, -99.67) * mm, "end": v(8.53, -96.67) * mm});
            skLineSegment(sketch, "E18.57.0", {"start": v(11.4, -99.35) * mm, "end": v(11.06, -96.37) * mm});
            skLineSegment(sketch, "E18.57.1", {"start": v(11.4, -99.35) * mm, "end": v(14.38, -99) * mm});
            skLineSegment(sketch, "E18.57.2", {"start": v(11.06, -96.37) * mm, "end": v(14.04, -96.03) * mm});
            skLineSegment(sketch, "E18.57.3", {"start": v(14.38, -99) * mm, "end": v(14.04, -96.03) * mm});
            skLineSegment(sketch, "E18.58.0", {"start": v(17.05, -98.54) * mm, "end": v(16.54, -95.58) * mm});
            skLineSegment(sketch, "E18.58.1", {"start": v(17.05, -98.54) * mm, "end": v(20, -98.02) * mm});
            skLineSegment(sketch, "E18.58.2", {"start": v(16.54, -95.58) * mm, "end": v(19.5, -95.07) * mm});
            skLineSegment(sketch, "E18.58.3", {"start": v(20, -98.02) * mm, "end": v(19.5, -95.07) * mm});
            skLineSegment(sketch, "E18.59.0", {"start": v(22.65, -97.4) * mm, "end": v(21.97, -94.48) * mm});
            skLineSegment(sketch, "E18.59.1", {"start": v(22.65, -97.4) * mm, "end": v(25.57, -96.72) * mm});
            skLineSegment(sketch, "E18.59.2", {"start": v(21.97, -94.48) * mm, "end": v(24.9, -93.8) * mm});
            skLineSegment(sketch, "E18.59.3", {"start": v(25.57, -96.72) * mm, "end": v(24.9, -93.8) * mm});
            skLineSegment(sketch, "E18.60.0", {"start": v(28.17, -95.95) * mm, "end": v(27.33, -93.07) * mm});
            skLineSegment(sketch, "E18.60.1", {"start": v(28.17, -95.95) * mm, "end": v(31.05, -95.1) * mm});
            skLineSegment(sketch, "E18.60.2", {"start": v(27.33, -93.07) * mm, "end": v(30.2, -92.23) * mm});
            skLineSegment(sketch, "E18.60.3", {"start": v(31.05, -95.1) * mm, "end": v(30.2, -92.23) * mm});
            skLineSegment(sketch, "E18.61.0", {"start": v(33.6, -94.18) * mm, "end": v(32.6, -91.36) * mm});
            skLineSegment(sketch, "E18.61.1", {"start": v(33.6, -94.18) * mm, "end": v(36.43, -93.18) * mm});
            skLineSegment(sketch, "E18.61.2", {"start": v(32.6, -91.36) * mm, "end": v(35.42, -90.35) * mm});
            skLineSegment(sketch, "E18.61.3", {"start": v(36.43, -93.18) * mm, "end": v(35.42, -90.35) * mm});
            skLineSegment(sketch, "E18.62.0", {"start": v(38.93, -92.11) * mm, "end": v(37.76, -89.35) * mm});
            skLineSegment(sketch, "E18.62.1", {"start": v(38.93, -92.11) * mm, "end": v(41.7, -90.94) * mm});
            skLineSegment(sketch, "E18.62.2", {"start": v(37.76, -89.35) * mm, "end": v(40.52, -88.18) * mm});
            skLineSegment(sketch, "E18.62.3", {"start": v(41.7, -90.94) * mm, "end": v(40.52, -88.18) * mm});
            skLineSegment(sketch, "E18.63.0", {"start": v(44.12, -89.74) * mm, "end": v(42.8, -87.05) * mm});
            skLineSegment(sketch, "E18.63.1", {"start": v(44.12, -89.74) * mm, "end": v(46.81, -88.42) * mm});
            skLineSegment(sketch, "E18.63.2", {"start": v(42.8, -87.05) * mm, "end": v(45.5, -85.72) * mm});
            skLineSegment(sketch, "E18.63.3", {"start": v(46.81, -88.42) * mm, "end": v(45.5, -85.72) * mm});
            skLineSegment(sketch, "E18.64.0", {"start": v(49.17, -87.07) * mm, "end": v(47.7, -84.46) * mm});
            skLineSegment(sketch, "E18.64.1", {"start": v(49.17, -87.07) * mm, "end": v(51.79, -85.6) * mm});
            skLineSegment(sketch, "E18.64.2", {"start": v(47.7, -84.46) * mm, "end": v(50.31, -82.99) * mm});
            skLineSegment(sketch, "E18.64.3", {"start": v(51.79, -85.6) * mm, "end": v(50.31, -82.99) * mm});
            skLineSegment(sketch, "E18.65.0", {"start": v(54.06, -84.13) * mm, "end": v(52.44, -81.6) * mm});
            skLineSegment(sketch, "E18.65.1", {"start": v(54.06, -84.13) * mm, "end": v(56.59, -82.5) * mm});
            skLineSegment(sketch, "E18.65.2", {"start": v(52.44, -81.6) * mm, "end": v(54.97, -79.98) * mm});
            skLineSegment(sketch, "E18.65.3", {"start": v(56.59, -82.5) * mm, "end": v(54.97, -79.98) * mm});
            skLineSegment(sketch, "E18.66.0", {"start": v(58.78, -80.9) * mm, "end": v(57.02, -78.47) * mm});
            skLineSegment(sketch, "E18.66.1", {"start": v(58.78, -80.9) * mm, "end": v(61.2, -79.14) * mm});
            skLineSegment(sketch, "E18.66.2", {"start": v(57.02, -78.47) * mm, "end": v(59.44, -76.71) * mm});
            skLineSegment(sketch, "E18.66.3", {"start": v(61.2, -79.14) * mm, "end": v(59.44, -76.71) * mm});
            skLineSegment(sketch, "E18.67.0", {"start": v(63.3, -77.41) * mm, "end": v(61.4, -75.1) * mm});
            skLineSegment(sketch, "E18.67.1", {"start": v(63.3, -77.41) * mm, "end": v(65.62, -75.52) * mm});
            skLineSegment(sketch, "E18.67.2", {"start": v(61.4, -75.1) * mm, "end": v(63.72, -73.2) * mm});
            skLineSegment(sketch, "E18.67.3", {"start": v(65.62, -75.52) * mm, "end": v(63.72, -73.2) * mm});
            skLineSegment(sketch, "E18.68.0", {"start": v(67.62, -73.67) * mm, "end": v(65.59, -71.46) * mm});
            skLineSegment(sketch, "E18.68.1", {"start": v(67.62, -73.67) * mm, "end": v(69.83, -71.65) * mm});
            skLineSegment(sketch, "E18.68.2", {"start": v(65.59, -71.46) * mm, "end": v(67.8, -69.44) * mm});
            skLineSegment(sketch, "E18.68.3", {"start": v(69.83, -71.65) * mm, "end": v(67.8, -69.44) * mm});
            skLineSegment(sketch, "E18.69.0", {"start": v(71.71, -69.7) * mm, "end": v(69.56, -67.6) * mm});
            skLineSegment(sketch, "E18.69.1", {"start": v(71.71, -69.7) * mm, "end": v(73.8, -67.54) * mm});
            skLineSegment(sketch, "E18.69.2", {"start": v(69.56, -67.6) * mm, "end": v(71.65, -65.45) * mm});
            skLineSegment(sketch, "E18.69.3", {"start": v(73.8, -67.54) * mm, "end": v(71.65, -65.45) * mm});
            skLineSegment(sketch, "E18.70.0", {"start": v(75.57, -65.49) * mm, "end": v(73.3, -63.52) * mm});
            skLineSegment(sketch, "E18.70.1", {"start": v(75.57, -65.49) * mm, "end": v(77.54, -63.22) * mm});
            skLineSegment(sketch, "E18.70.2", {"start": v(73.3, -63.52) * mm, "end": v(75.27, -61.25) * mm});
            skLineSegment(sketch, "E18.70.3", {"start": v(77.54, -63.22) * mm, "end": v(75.27, -61.25) * mm});
            skLineSegment(sketch, "E18.71.0", {"start": v(79.2, -61.06) * mm, "end": v(76.81, -59.23) * mm});
            skLineSegment(sketch, "E18.71.1", {"start": v(79.2, -61.06) * mm, "end": v(81.02, -58.69) * mm});
            skLineSegment(sketch, "E18.71.2", {"start": v(76.81, -59.23) * mm, "end": v(78.65, -56.86) * mm});
            skLineSegment(sketch, "E18.71.3", {"start": v(81.02, -58.69) * mm, "end": v(78.65, -56.86) * mm});
            skLineSegment(sketch, "E18.72.0", {"start": v(82.55, -56.44) * mm, "end": v(80.07, -54.75) * mm});
            skLineSegment(sketch, "E18.72.1", {"start": v(82.55, -56.44) * mm, "end": v(84.24, -53.97) * mm});
            skLineSegment(sketch, "E18.72.2", {"start": v(80.07, -54.75) * mm, "end": v(81.76, -52.27) * mm});
            skLineSegment(sketch, "E18.72.3", {"start": v(84.24, -53.97) * mm, "end": v(81.76, -52.27) * mm});
            skLineSegment(sketch, "E18.73.0", {"start": v(85.63, -51.64) * mm, "end": v(83.07, -50.1) * mm});
            skLineSegment(sketch, "E18.73.1", {"start": v(85.63, -51.64) * mm, "end": v(87.18, -49.07) * mm});
            skLineSegment(sketch, "E18.73.2", {"start": v(83.07, -50.1) * mm, "end": v(84.62, -47.52) * mm});
            skLineSegment(sketch, "E18.73.3", {"start": v(87.18, -49.07) * mm, "end": v(84.62, -47.52) * mm});
            skLineSegment(sketch, "E18.74.0", {"start": v(88.44, -46.67) * mm, "end": v(85.79, -45.27) * mm});
            skLineSegment(sketch, "E18.74.1", {"start": v(88.44, -46.67) * mm, "end": v(89.84, -44.01) * mm});
            skLineSegment(sketch, "E18.74.2", {"start": v(85.79, -45.27) * mm, "end": v(87.19, -42.61) * mm});
            skLineSegment(sketch, "E18.74.3", {"start": v(89.84, -44.01) * mm, "end": v(87.19, -42.61) * mm});
            skLineSegment(sketch, "E18.75.0", {"start": v(90.96, -41.54) * mm, "end": v(88.23, -40.3) * mm});
            skLineSegment(sketch, "E18.75.1", {"start": v(90.96, -41.54) * mm, "end": v(92.2, -38.81) * mm});
            skLineSegment(sketch, "E18.75.2", {"start": v(88.23, -40.3) * mm, "end": v(89.48, -37.57) * mm});
            skLineSegment(sketch, "E18.75.3", {"start": v(92.2, -38.81) * mm, "end": v(89.48, -37.57) * mm});
            skLineSegment(sketch, "E18.76.0", {"start": v(93.19, -36.28) * mm, "end": v(90.4, -35.2) * mm});
            skLineSegment(sketch, "E18.76.1", {"start": v(93.19, -36.28) * mm, "end": v(94.27, -33.49) * mm});
            skLineSegment(sketch, "E18.76.2", {"start": v(90.4, -35.2) * mm, "end": v(91.48, -32.4) * mm});
            skLineSegment(sketch, "E18.76.3", {"start": v(94.27, -33.49) * mm, "end": v(91.48, -32.4) * mm});
            skLineSegment(sketch, "E18.77.0", {"start": v(95.1, -30.9) * mm, "end": v(92.25, -29.97) * mm});
            skLineSegment(sketch, "E18.77.1", {"start": v(95.1, -30.9) * mm, "end": v(96.03, -28.05) * mm});
            skLineSegment(sketch, "E18.77.2", {"start": v(92.25, -29.97) * mm, "end": v(93.18, -27.12) * mm});
            skLineSegment(sketch, "E18.77.3", {"start": v(96.03, -28.05) * mm, "end": v(93.18, -27.12) * mm});
            skLineSegment(sketch, "E18.78.0", {"start": v(96.71, -25.42) * mm, "end": v(93.81, -24.66) * mm});
            skLineSegment(sketch, "E18.78.1", {"start": v(96.71, -25.42) * mm, "end": v(97.48, -22.52) * mm});
            skLineSegment(sketch, "E18.78.2", {"start": v(93.81, -24.66) * mm, "end": v(94.58, -21.76) * mm});
            skLineSegment(sketch, "E18.78.3", {"start": v(97.48, -22.52) * mm, "end": v(94.58, -21.76) * mm});
            skLineSegment(sketch, "E18.79.0", {"start": v(98, -19.86) * mm, "end": v(95.07, -19.26) * mm});
            skLineSegment(sketch, "E18.79.1", {"start": v(98, -19.86) * mm, "end": v(98.6, -16.92) * mm});
            skLineSegment(sketch, "E18.79.2", {"start": v(95.07, -19.26) * mm, "end": v(95.66, -16.32) * mm});
            skLineSegment(sketch, "E18.79.3", {"start": v(98.6, -16.92) * mm, "end": v(95.66, -16.32) * mm});
            skLineSegment(sketch, "E18.80.0", {"start": v(98.98, -14.23) * mm, "end": v(96.01, -13.8) * mm});
            skLineSegment(sketch, "E18.80.1", {"start": v(98.98, -14.23) * mm, "end": v(99.4, -11.26) * mm});
            skLineSegment(sketch, "E18.80.2", {"start": v(96.01, -13.8) * mm, "end": v(96.44, -10.84) * mm});
            skLineSegment(sketch, "E18.80.3", {"start": v(99.4, -11.26) * mm, "end": v(96.44, -10.84) * mm});
            skLineSegment(sketch, "E18.81.0", {"start": v(99.63, -8.56) * mm, "end": v(96.64, -8.3) * mm});
            skLineSegment(sketch, "E18.81.1", {"start": v(99.63, -8.56) * mm, "end": v(99.89, -5.57) * mm});
            skLineSegment(sketch, "E18.81.2", {"start": v(96.64, -8.3) * mm, "end": v(96.9, -5.31) * mm});
            skLineSegment(sketch, "E18.81.3", {"start": v(99.89, -5.57) * mm, "end": v(96.9, -5.31) * mm});
            skLineSegment(sketch, "E18.82.0", {"start": v(99.96, -2.86) * mm, "end": v(96.96, -2.77) * mm});
            skLineSegment(sketch, "E18.82.1", {"start": v(99.96, -2.86) * mm, "end": v(100.04, 0.14) * mm});
            skLineSegment(sketch, "E18.82.2", {"start": v(96.96, -2.77) * mm, "end": v(97.05, 0.23) * mm});
            skLineSegment(sketch, "E18.82.3", {"start": v(100.04, 0.14) * mm, "end": v(97.05, 0.23) * mm});
            skLineSegment(sketch, "E18.83.0", {"start": v(99.96, 2.86) * mm, "end": v(96.96, 2.77) * mm});
            skLineSegment(sketch, "E18.83.1", {"start": v(99.96, 2.86) * mm, "end": v(99.87, 5.85) * mm});
            skLineSegment(sketch, "E18.83.2", {"start": v(96.96, 2.77) * mm, "end": v(96.87, 5.77) * mm});
            skLineSegment(sketch, "E18.83.3", {"start": v(99.87, 5.85) * mm, "end": v(96.87, 5.77) * mm});
            skLineSegment(sketch, "E18.84.0", {"start": v(99.63, 8.56) * mm, "end": v(96.64, 8.3) * mm});
            skLineSegment(sketch, "E18.84.1", {"start": v(99.63, 8.56) * mm, "end": v(99.38, 11.55) * mm});
            skLineSegment(sketch, "E18.84.2", {"start": v(96.64, 8.3) * mm, "end": v(96.39, 11.29) * mm});
            skLineSegment(sketch, "E18.84.3", {"start": v(99.38, 11.55) * mm, "end": v(96.39, 11.29) * mm});
            skLineSegment(sketch, "E18.85.0", {"start": v(98.98, 14.23) * mm, "end": v(96.01, 13.8) * mm});
            skLineSegment(sketch, "E18.85.1", {"start": v(98.98, 14.23) * mm, "end": v(98.56, 17.2) * mm});
            skLineSegment(sketch, "E18.85.2", {"start": v(96.01, 13.8) * mm, "end": v(95.59, 16.77) * mm});
            skLineSegment(sketch, "E18.85.3", {"start": v(98.56, 17.2) * mm, "end": v(95.59, 16.77) * mm});
            skLineSegment(sketch, "E18.86.0", {"start": v(98, 19.86) * mm, "end": v(95.07, 19.26) * mm});
            skLineSegment(sketch, "E18.86.1", {"start": v(98, 19.86) * mm, "end": v(97.41, 22.8) * mm});
            skLineSegment(sketch, "E18.86.2", {"start": v(95.07, 19.26) * mm, "end": v(94.47, 22.2) * mm});
            skLineSegment(sketch, "E18.86.3", {"start": v(97.41, 22.8) * mm, "end": v(94.47, 22.2) * mm});
            skLineSegment(sketch, "E18.87.0", {"start": v(96.71, 25.42) * mm, "end": v(93.81, 24.66) * mm});
            skLineSegment(sketch, "E18.87.1", {"start": v(96.71, 25.42) * mm, "end": v(95.95, 28.32) * mm});
            skLineSegment(sketch, "E18.87.2", {"start": v(93.81, 24.66) * mm, "end": v(93.05, 27.56) * mm});
            skLineSegment(sketch, "E18.87.3", {"start": v(95.95, 28.32) * mm, "end": v(93.05, 27.56) * mm});
            skLineSegment(sketch, "E18.88.0", {"start": v(95.1, 30.9) * mm, "end": v(92.25, 29.97) * mm});
            skLineSegment(sketch, "E18.88.1", {"start": v(95.1, 30.9) * mm, "end": v(94.18, 33.75) * mm});
            skLineSegment(sketch, "E18.88.2", {"start": v(92.25, 29.97) * mm, "end": v(91.33, 32.83) * mm});
            skLineSegment(sketch, "E18.88.3", {"start": v(94.18, 33.75) * mm, "end": v(91.33, 32.83) * mm});
            skLineSegment(sketch, "E18.89.0", {"start": v(93.19, 36.28) * mm, "end": v(90.4, 35.2) * mm});
            skLineSegment(sketch, "E18.89.1", {"start": v(93.19, 36.28) * mm, "end": v(92.1, 39.08) * mm});
            skLineSegment(sketch, "E18.89.2", {"start": v(90.4, 35.2) * mm, "end": v(89.3, 37.99) * mm});
            skLineSegment(sketch, "E18.89.3", {"start": v(92.1, 39.08) * mm, "end": v(89.3, 37.99) * mm});
            skLineSegment(sketch, "E18.90.0", {"start": v(90.96, 41.54) * mm, "end": v(88.23, 40.3) * mm});
            skLineSegment(sketch, "E18.90.1", {"start": v(90.96, 41.54) * mm, "end": v(89.72, 44.27) * mm});
            skLineSegment(sketch, "E18.90.2", {"start": v(88.23, 40.3) * mm, "end": v(86.99, 43.02) * mm});
            skLineSegment(sketch, "E18.90.3", {"start": v(89.72, 44.27) * mm, "end": v(86.99, 43.02) * mm});
            skLineSegment(sketch, "E18.91.0", {"start": v(88.44, 46.67) * mm, "end": v(85.79, 45.27) * mm});
            skLineSegment(sketch, "E18.91.1", {"start": v(88.44, 46.67) * mm, "end": v(87.04, 49.32) * mm});
            skLineSegment(sketch, "E18.91.2", {"start": v(85.79, 45.27) * mm, "end": v(84.39, 47.92) * mm});
            skLineSegment(sketch, "E18.91.3", {"start": v(87.04, 49.32) * mm, "end": v(84.39, 47.92) * mm});
            skLineSegment(sketch, "E18.92.0", {"start": v(85.63, 51.64) * mm, "end": v(83.07, 50.1) * mm});
            skLineSegment(sketch, "E18.92.1", {"start": v(85.63, 51.64) * mm, "end": v(84.09, 54.2) * mm});
            skLineSegment(sketch, "E18.92.2", {"start": v(83.07, 50.1) * mm, "end": v(81.52, 52.66) * mm});
            skLineSegment(sketch, "E18.92.3", {"start": v(84.09, 54.2) * mm, "end": v(81.52, 52.66) * mm});
            skLineSegment(sketch, "E18.93.0", {"start": v(82.55, 56.44) * mm, "end": v(80.07, 54.75) * mm});
            skLineSegment(sketch, "E18.93.1", {"start": v(82.55, 56.44) * mm, "end": v(80.85, 58.92) * mm});
            skLineSegment(sketch, "E18.93.2", {"start": v(80.07, 54.75) * mm, "end": v(78.38, 57.23) * mm});
            skLineSegment(sketch, "E18.93.3", {"start": v(80.85, 58.92) * mm, "end": v(78.38, 57.23) * mm});
            skLineSegment(sketch, "E18.94.0", {"start": v(79.2, 61.06) * mm, "end": v(76.81, 59.23) * mm});
            skLineSegment(sketch, "E18.94.1", {"start": v(79.2, 61.06) * mm, "end": v(77.36, 63.44) * mm});
            skLineSegment(sketch, "E18.94.2", {"start": v(76.81, 59.23) * mm, "end": v(74.98, 61.6) * mm});
            skLineSegment(sketch, "E18.94.3", {"start": v(77.36, 63.44) * mm, "end": v(74.98, 61.6) * mm});
            skLineSegment(sketch, "E18.95.0", {"start": v(75.57, 65.49) * mm, "end": v(73.3, 63.52) * mm});
            skLineSegment(sketch, "E18.95.1", {"start": v(75.57, 65.49) * mm, "end": v(73.61, 67.75) * mm});
            skLineSegment(sketch, "E18.95.2", {"start": v(73.3, 63.52) * mm, "end": v(71.34, 65.79) * mm});
            skLineSegment(sketch, "E18.95.3", {"start": v(73.61, 67.75) * mm, "end": v(71.34, 65.79) * mm});
            skLineSegment(sketch, "E18.96.0", {"start": v(71.71, 69.7) * mm, "end": v(69.56, 67.6) * mm});
            skLineSegment(sketch, "E18.96.1", {"start": v(71.71, 69.7) * mm, "end": v(69.62, 71.85) * mm});
            skLineSegment(sketch, "E18.96.2", {"start": v(69.56, 67.6) * mm, "end": v(67.47, 69.75) * mm});
            skLineSegment(sketch, "E18.96.3", {"start": v(69.62, 71.85) * mm, "end": v(67.47, 69.75) * mm});
            skLineSegment(sketch, "E18.97.0", {"start": v(67.62, 73.67) * mm, "end": v(65.59, 71.46) * mm});
            skLineSegment(sketch, "E18.97.1", {"start": v(67.62, 73.67) * mm, "end": v(65.4, 75.7) * mm});
            skLineSegment(sketch, "E18.97.2", {"start": v(65.59, 71.46) * mm, "end": v(63.38, 73.5) * mm});
            skLineSegment(sketch, "E18.97.3", {"start": v(65.4, 75.7) * mm, "end": v(63.38, 73.5) * mm});
            skLineSegment(sketch, "E18.98.0", {"start": v(63.3, 77.41) * mm, "end": v(61.4, 75.1) * mm});
            skLineSegment(sketch, "E18.98.1", {"start": v(63.3, 77.41) * mm, "end": v(60.98, 79.31) * mm});
            skLineSegment(sketch, "E18.98.2", {"start": v(61.4, 75.1) * mm, "end": v(59.08, 77) * mm});
            skLineSegment(sketch, "E18.98.3", {"start": v(60.98, 79.31) * mm, "end": v(59.08, 77) * mm});
            skLineSegment(sketch, "E18.99.0", {"start": v(58.78, 80.9) * mm, "end": v(57.02, 78.47) * mm});
            skLineSegment(sketch, "E18.99.1", {"start": v(58.78, 80.9) * mm, "end": v(56.35, 82.67) * mm});
            skLineSegment(sketch, "E18.99.2", {"start": v(57.02, 78.47) * mm, "end": v(54.59, 80.24) * mm});
            skLineSegment(sketch, "E18.99.3", {"start": v(56.35, 82.67) * mm, "end": v(54.59, 80.24) * mm});
            skPoint(sketch, "E18.center", {"position": v(0, 0) * mm});
            skLineSegment(sketch, "E19.3.100.0", {"start": v(54.06, 84.13) * mm, "end": v(51.54, 85.75) * mm});
            skLineSegment(sketch, "E19.5.100.0", {"start": v(54.06, 84.13) * mm, "end": v(52.44, 81.6) * mm});
            skLineSegment(sketch, "E19.6.100.0", {"start": v(52.44, 81.6) * mm, "end": v(49.92, 83.22) * mm});
            skLineSegment(sketch, "E19.9.100.0", {"start": v(51.54, 85.75) * mm, "end": v(49.92, 83.22) * mm});
            skLineSegment(sketch, "E19.3.101.0", {"start": v(49.17, 87.07) * mm, "end": v(46.56, 88.55) * mm});
            skLineSegment(sketch, "E19.5.101.0", {"start": v(49.17, 87.07) * mm, "end": v(47.7, 84.46) * mm});
            skLineSegment(sketch, "E19.6.101.0", {"start": v(47.7, 84.46) * mm, "end": v(45.09, 85.94) * mm});
            skLineSegment(sketch, "E19.9.101.0", {"start": v(46.56, 88.55) * mm, "end": v(45.09, 85.94) * mm});
            skLineSegment(sketch, "E19.3.102.0", {"start": v(44.12, 89.74) * mm, "end": v(41.43, 91.06) * mm});
            skLineSegment(sketch, "E19.5.102.0", {"start": v(44.12, 89.74) * mm, "end": v(42.8, 87.05) * mm});
            skLineSegment(sketch, "E19.6.102.0", {"start": v(42.8, 87.05) * mm, "end": v(40.1, 88.37) * mm});
            skLineSegment(sketch, "E19.9.102.0", {"start": v(41.43, 91.06) * mm, "end": v(40.1, 88.37) * mm});
            skLineSegment(sketch, "E19.3.103.0", {"start": v(38.93, 92.11) * mm, "end": v(36.16, 93.28) * mm});
            skLineSegment(sketch, "E19.5.103.0", {"start": v(38.93, 92.11) * mm, "end": v(37.76, 89.35) * mm});
            skLineSegment(sketch, "E19.6.103.0", {"start": v(37.76, 89.35) * mm, "end": v(35, 90.52) * mm});
            skLineSegment(sketch, "E19.9.103.0", {"start": v(36.16, 93.28) * mm, "end": v(35, 90.52) * mm});
            skLineSegment(sketch, "E19.3.104.0", {"start": v(33.6, 94.18) * mm, "end": v(30.78, 95.2) * mm});
            skLineSegment(sketch, "E19.5.104.0", {"start": v(33.6, 94.18) * mm, "end": v(32.6, 91.36) * mm});
            skLineSegment(sketch, "E19.6.104.0", {"start": v(32.6, 91.36) * mm, "end": v(29.77, 92.37) * mm});
            skLineSegment(sketch, "E19.9.104.0", {"start": v(30.78, 95.2) * mm, "end": v(29.77, 92.37) * mm});
            skLineSegment(sketch, "E19.3.105.0", {"start": v(28.17, 95.95) * mm, "end": v(25.3, 96.8) * mm});
            skLineSegment(sketch, "E19.5.105.0", {"start": v(28.17, 95.95) * mm, "end": v(27.33, 93.07) * mm});
            skLineSegment(sketch, "E19.6.105.0", {"start": v(27.33, 93.07) * mm, "end": v(24.45, 93.92) * mm});
            skLineSegment(sketch, "E19.9.105.0", {"start": v(25.3, 96.8) * mm, "end": v(24.45, 93.92) * mm});
            skLineSegment(sketch, "E19.3.106.0", {"start": v(22.65, 97.4) * mm, "end": v(19.73, 98.08) * mm});
            skLineSegment(sketch, "E19.5.106.0", {"start": v(22.65, 97.4) * mm, "end": v(21.97, 94.48) * mm});
            skLineSegment(sketch, "E19.6.106.0", {"start": v(21.97, 94.48) * mm, "end": v(19.05, 95.16) * mm});
            skLineSegment(sketch, "E19.9.106.0", {"start": v(19.73, 98.08) * mm, "end": v(19.05, 95.16) * mm});
            skLineSegment(sketch, "E19.3.107.0", {"start": v(17.05, 98.54) * mm, "end": v(14.1, 99.05) * mm});
            skLineSegment(sketch, "E19.5.107.0", {"start": v(17.05, 98.54) * mm, "end": v(16.54, 95.58) * mm});
            skLineSegment(sketch, "E19.6.107.0", {"start": v(16.54, 95.58) * mm, "end": v(13.58, 96.1) * mm});
            skLineSegment(sketch, "E19.9.107.0", {"start": v(14.1, 99.05) * mm, "end": v(13.58, 96.1) * mm});
            skLineSegment(sketch, "E19.3.108.0", {"start": v(11.4, 99.35) * mm, "end": v(8.42, 99.7) * mm});
            skLineSegment(sketch, "E19.5.108.0", {"start": v(11.4, 99.35) * mm, "end": v(11.06, 96.37) * mm});
            skLineSegment(sketch, "E19.6.108.0", {"start": v(11.06, 96.37) * mm, "end": v(8.08, 96.7) * mm});
            skLineSegment(sketch, "E19.9.108.0", {"start": v(8.42, 99.7) * mm, "end": v(8.08, 96.7) * mm});
            skLineSegment(sketch, "E19.3.109.0", {"start": v(5.7, 99.84) * mm, "end": v(2.71, 100) * mm});
            skLineSegment(sketch, "E19.5.109.0", {"start": v(5.7, 99.84) * mm, "end": v(5.54, 96.84) * mm});
            skLineSegment(sketch, "E19.6.109.0", {"start": v(5.54, 96.84) * mm, "end": v(2.54, 97.01) * mm});
            skLineSegment(sketch, "E19.9.109.0", {"start": v(2.71, 100) * mm, "end": v(2.54, 97.01) * mm});
            skSolve(sketch);
        }
        {
            var Q0;
            Q0 = qSketchRegion(id + "F13", true);
            extrude(context, id + "F14", {"entities" : qUnion([Q0]), "operationType" : NewBodyOperationType.ADD, "oppositeDirection" : true, "depth" : 30 * mm});
        }
        {
            var Q0;
            Q0=qCreatedBy(id+"F3.planeOp",FACE);
            cPlane(context, id + "F15", {"entities" : qUnion([Q0]), "cplaneType" : CPlaneType.OFFSET, "offset" : 73 * mm, "oppositeDirection" : true, "width" : 150 * mm, "height" : 150 * mm});
        }
        {
            var Q0;
            Q0=qCreatedBy(id+"F15.planeOp",FACE);
            var sketch = newSketch(context, id + "F16", { "sketchPlane" : qUnion([Q0])});
            skLineSegment(sketch, "E20", {"start": v(0, 0) * mm, "end": v(100, 0) * mm, "construction": true});
            skCircle(sketch, "E21", {"center": v(0, 0) * mm, "radius": 100 * mm});
            skCircle(sketch, "E22", {"center": v(0, 0) * mm, "radius": 97 * mm});
            skSolve(sketch);
        }
        {
            var Q0;
            Q0 = qSketchRegion(id + "F16", true);
            extrude(context, id + "F17", {"entities" : qUnion([Q0]), "operationType" : NewBodyOperationType.ADD, "oppositeDirection" : true, "depth" : 3 * mm});
        }
    });
